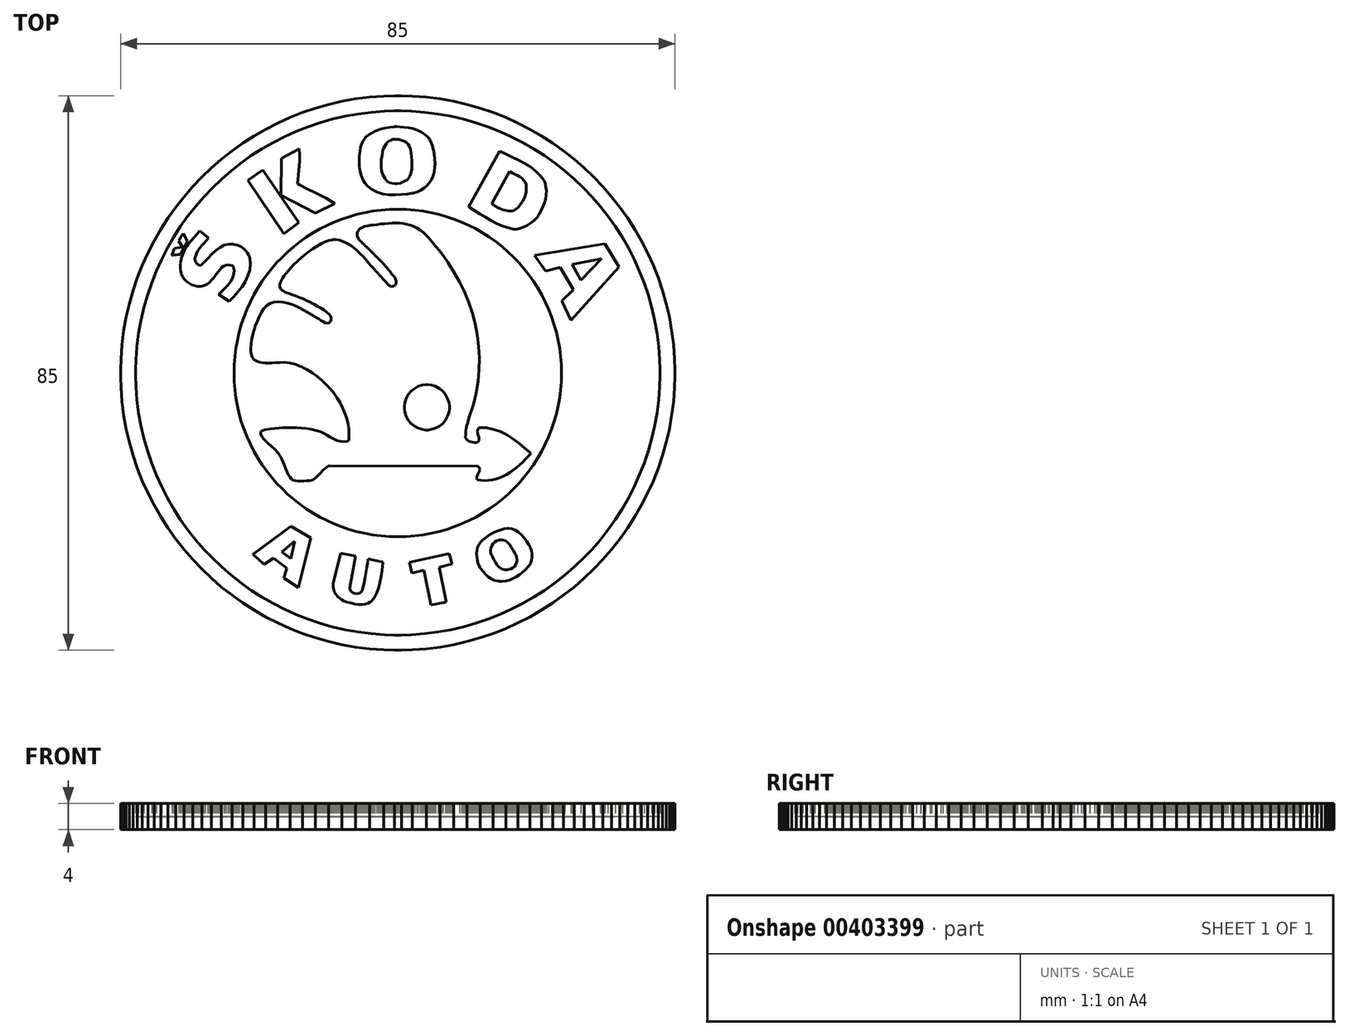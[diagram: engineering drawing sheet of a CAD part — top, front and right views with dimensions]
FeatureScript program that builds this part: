
annotation { "Feature Type Name" : "Feature", "Feature Type Description" : "" }
export const myFeature = defineFeature(function(context is Context, id is Id, definition is map)
    precondition{}
    {
        {
            var Q0;
            Q0=qCreatedBy(makeId("Top.planeOp"),FACE);
            var sketch = newSketch(context, id + "F0", { "sketchPlane" : qUnion([Q0])});
            skLineSegment(sketch, "E0", {"start": v(0.02, -42.5) * mm, "end": v(0.57, -42.5) * mm});
            skLineSegment(sketch, "E1", {"start": v(0.57, -42.5) * mm, "end": v(2.2, -42.44) * mm});
            skLineSegment(sketch, "E2", {"start": v(2.2, -42.44) * mm, "end": v(4.36, -42.28) * mm});
            skLineSegment(sketch, "E3", {"start": v(4.36, -42.28) * mm, "end": v(6.49, -42) * mm});
            skLineSegment(sketch, "E4", {"start": v(6.49, -42) * mm, "end": v(8.58, -41.63) * mm});
            skLineSegment(sketch, "E5", {"start": v(8.58, -41.63) * mm, "end": v(10.64, -41.16) * mm});
            skLineSegment(sketch, "E6", {"start": v(10.64, -41.16) * mm, "end": v(12.65, -40.59) * mm});
            skLineSegment(sketch, "E7", {"start": v(12.65, -40.59) * mm, "end": v(14.63, -39.92) * mm});
            skLineSegment(sketch, "E8", {"start": v(14.63, -39.92) * mm, "end": v(16.55, -39.16) * mm});
            skLineSegment(sketch, "E9", {"start": v(16.55, -39.16) * mm, "end": v(18.44, -38.3) * mm});
            skLineSegment(sketch, "E10", {"start": v(18.44, -38.3) * mm, "end": v(20.27, -37.37) * mm});
            skLineSegment(sketch, "E11", {"start": v(20.27, -37.37) * mm, "end": v(22.05, -36.35) * mm});
            skLineSegment(sketch, "E12", {"start": v(22.05, -36.35) * mm, "end": v(23.77, -35.24) * mm});
            skLineSegment(sketch, "E13", {"start": v(23.77, -35.24) * mm, "end": v(25.44, -34.06) * mm});
            skLineSegment(sketch, "E14", {"start": v(25.44, -34.06) * mm, "end": v(27.04, -32.8) * mm});
            skLineSegment(sketch, "E15", {"start": v(27.04, -32.8) * mm, "end": v(28.58, -31.46) * mm});
            skLineSegment(sketch, "E16", {"start": v(28.58, -31.46) * mm, "end": v(30.06, -30.06) * mm});
            skLineSegment(sketch, "E17", {"start": v(30.06, -30.06) * mm, "end": v(31.46, -28.58) * mm});
            skLineSegment(sketch, "E18", {"start": v(31.46, -28.58) * mm, "end": v(32.8, -27.04) * mm});
            skLineSegment(sketch, "E19", {"start": v(32.8, -27.04) * mm, "end": v(34.06, -25.44) * mm});
            skLineSegment(sketch, "E20", {"start": v(34.06, -25.44) * mm, "end": v(35.24, -23.77) * mm});
            skLineSegment(sketch, "E21", {"start": v(35.24, -23.77) * mm, "end": v(36.35, -22.05) * mm});
            skLineSegment(sketch, "E22", {"start": v(36.35, -22.05) * mm, "end": v(37.37, -20.27) * mm});
            skLineSegment(sketch, "E23", {"start": v(37.37, -20.27) * mm, "end": v(38.3, -18.44) * mm});
            skLineSegment(sketch, "E24", {"start": v(38.3, -18.44) * mm, "end": v(39.16, -16.55) * mm});
            skLineSegment(sketch, "E25", {"start": v(39.16, -16.55) * mm, "end": v(39.92, -14.63) * mm});
            skLineSegment(sketch, "E26", {"start": v(39.92, -14.63) * mm, "end": v(40.59, -12.65) * mm});
            skLineSegment(sketch, "E27", {"start": v(40.59, -12.65) * mm, "end": v(41.16, -10.64) * mm});
            skLineSegment(sketch, "E28", {"start": v(41.16, -10.64) * mm, "end": v(41.63, -8.58) * mm});
            skLineSegment(sketch, "E29", {"start": v(41.63, -8.58) * mm, "end": v(42, -6.49) * mm});
            skLineSegment(sketch, "E30", {"start": v(42, -6.49) * mm, "end": v(42.28, -4.36) * mm});
            skLineSegment(sketch, "E31", {"start": v(42.28, -4.36) * mm, "end": v(42.44, -2.2) * mm});
            skLineSegment(sketch, "E32", {"start": v(42.44, -2.2) * mm, "end": v(42.5, -0.57) * mm});
            skLineSegment(sketch, "E33", {"start": v(42.5, -0.57) * mm, "end": v(42.5, -0.02) * mm});
            skLineSegment(sketch, "E34", {"start": v(42.5, -0.02) * mm, "end": v(42.5, 0.53) * mm});
            skLineSegment(sketch, "E35", {"start": v(42.5, 0.53) * mm, "end": v(42.44, 2.17) * mm});
            skLineSegment(sketch, "E36", {"start": v(42.44, 2.17) * mm, "end": v(42.28, 4.33) * mm});
            skLineSegment(sketch, "E37", {"start": v(42.28, 4.33) * mm, "end": v(42, 6.45) * mm});
            skLineSegment(sketch, "E38", {"start": v(42, 6.45) * mm, "end": v(41.63, 8.55) * mm});
            skLineSegment(sketch, "E39", {"start": v(41.63, 8.55) * mm, "end": v(41.16, 10.6) * mm});
            skLineSegment(sketch, "E40", {"start": v(41.16, 10.6) * mm, "end": v(40.59, 12.62) * mm});
            skLineSegment(sketch, "E41", {"start": v(40.59, 12.62) * mm, "end": v(39.92, 14.6) * mm});
            skLineSegment(sketch, "E42", {"start": v(39.92, 14.6) * mm, "end": v(39.16, 16.52) * mm});
            skLineSegment(sketch, "E43", {"start": v(39.16, 16.52) * mm, "end": v(38.3, 18.4) * mm});
            skLineSegment(sketch, "E44", {"start": v(38.3, 18.4) * mm, "end": v(37.37, 20.24) * mm});
            skLineSegment(sketch, "E45", {"start": v(37.37, 20.24) * mm, "end": v(36.35, 22.02) * mm});
            skLineSegment(sketch, "E46", {"start": v(36.35, 22.02) * mm, "end": v(35.24, 23.75) * mm});
            skLineSegment(sketch, "E47", {"start": v(35.24, 23.75) * mm, "end": v(34.06, 25.41) * mm});
            skLineSegment(sketch, "E48", {"start": v(34.06, 25.41) * mm, "end": v(32.8, 27.02) * mm});
            skLineSegment(sketch, "E49", {"start": v(32.8, 27.02) * mm, "end": v(31.46, 28.56) * mm});
            skLineSegment(sketch, "E50", {"start": v(31.46, 28.56) * mm, "end": v(30.06, 30.04) * mm});
            skLineSegment(sketch, "E51", {"start": v(30.06, 30.04) * mm, "end": v(28.58, 31.45) * mm});
            skLineSegment(sketch, "E52", {"start": v(28.58, 31.45) * mm, "end": v(27.04, 32.78) * mm});
            skLineSegment(sketch, "E53", {"start": v(27.04, 32.78) * mm, "end": v(25.44, 34.05) * mm});
            skLineSegment(sketch, "E54", {"start": v(25.44, 34.05) * mm, "end": v(23.77, 35.23) * mm});
            skLineSegment(sketch, "E55", {"start": v(23.77, 35.23) * mm, "end": v(22.05, 36.34) * mm});
            skLineSegment(sketch, "E56", {"start": v(22.05, 36.34) * mm, "end": v(20.27, 37.36) * mm});
            skLineSegment(sketch, "E57", {"start": v(20.27, 37.36) * mm, "end": v(18.44, 38.3) * mm});
            skLineSegment(sketch, "E58", {"start": v(18.44, 38.3) * mm, "end": v(16.55, 39.15) * mm});
            skLineSegment(sketch, "E59", {"start": v(16.55, 39.15) * mm, "end": v(14.63, 39.92) * mm});
            skLineSegment(sketch, "E60", {"start": v(14.63, 39.92) * mm, "end": v(12.65, 40.58) * mm});
            skLineSegment(sketch, "E61", {"start": v(12.65, 40.58) * mm, "end": v(10.64, 41.16) * mm});
            skLineSegment(sketch, "E62", {"start": v(10.64, 41.16) * mm, "end": v(8.58, 41.63) * mm});
            skLineSegment(sketch, "E63", {"start": v(8.58, 41.63) * mm, "end": v(6.49, 42) * mm});
            skLineSegment(sketch, "E64", {"start": v(6.49, 42) * mm, "end": v(4.36, 42.28) * mm});
            skLineSegment(sketch, "E65", {"start": v(4.36, 42.28) * mm, "end": v(2.2, 42.44) * mm});
            skLineSegment(sketch, "E66", {"start": v(2.2, 42.44) * mm, "end": v(0.57, 42.5) * mm});
            skLineSegment(sketch, "E67", {"start": v(0.57, 42.5) * mm, "end": v(0.02, 42.5) * mm});
            skLineSegment(sketch, "E68", {"start": v(0.02, 42.5) * mm, "end": v(-0.53, 42.5) * mm});
            skLineSegment(sketch, "E69", {"start": v(-0.53, 42.5) * mm, "end": v(-2.17, 42.44) * mm});
            skLineSegment(sketch, "E70", {"start": v(-2.17, 42.44) * mm, "end": v(-4.33, 42.28) * mm});
            skLineSegment(sketch, "E71", {"start": v(-4.33, 42.28) * mm, "end": v(-6.45, 42) * mm});
            skLineSegment(sketch, "E72", {"start": v(-6.45, 42) * mm, "end": v(-8.55, 41.63) * mm});
            skLineSegment(sketch, "E73", {"start": v(-8.55, 41.63) * mm, "end": v(-10.6, 41.16) * mm});
            skLineSegment(sketch, "E74", {"start": v(-10.6, 41.16) * mm, "end": v(-12.62, 40.58) * mm});
            skLineSegment(sketch, "E75", {"start": v(-12.62, 40.58) * mm, "end": v(-14.6, 39.92) * mm});
            skLineSegment(sketch, "E76", {"start": v(-14.6, 39.92) * mm, "end": v(-16.52, 39.15) * mm});
            skLineSegment(sketch, "E77", {"start": v(-16.52, 39.15) * mm, "end": v(-18.4, 38.3) * mm});
            skLineSegment(sketch, "E78", {"start": v(-18.4, 38.3) * mm, "end": v(-20.24, 37.36) * mm});
            skLineSegment(sketch, "E79", {"start": v(-20.24, 37.36) * mm, "end": v(-22.02, 36.34) * mm});
            skLineSegment(sketch, "E80", {"start": v(-22.02, 36.34) * mm, "end": v(-23.74, 35.23) * mm});
            skLineSegment(sketch, "E81", {"start": v(-23.74, 35.23) * mm, "end": v(-25.41, 34.05) * mm});
            skLineSegment(sketch, "E82", {"start": v(-25.41, 34.05) * mm, "end": v(-27.02, 32.78) * mm});
            skLineSegment(sketch, "E83", {"start": v(-27.02, 32.78) * mm, "end": v(-28.56, 31.45) * mm});
            skLineSegment(sketch, "E84", {"start": v(-28.56, 31.45) * mm, "end": v(-30.04, 30.04) * mm});
            skLineSegment(sketch, "E85", {"start": v(-30.04, 30.04) * mm, "end": v(-31.45, 28.56) * mm});
            skLineSegment(sketch, "E86", {"start": v(-31.45, 28.56) * mm, "end": v(-32.78, 27.02) * mm});
            skLineSegment(sketch, "E87", {"start": v(-32.78, 27.02) * mm, "end": v(-34.05, 25.41) * mm});
            skLineSegment(sketch, "E88", {"start": v(-34.05, 25.41) * mm, "end": v(-35.23, 23.75) * mm});
            skLineSegment(sketch, "E89", {"start": v(-35.23, 23.75) * mm, "end": v(-36.34, 22.02) * mm});
            skLineSegment(sketch, "E90", {"start": v(-36.34, 22.02) * mm, "end": v(-37.36, 20.24) * mm});
            skLineSegment(sketch, "E91", {"start": v(-37.36, 20.24) * mm, "end": v(-38.3, 18.4) * mm});
            skLineSegment(sketch, "E92", {"start": v(-38.3, 18.4) * mm, "end": v(-39.15, 16.52) * mm});
            skLineSegment(sketch, "E93", {"start": v(-39.15, 16.52) * mm, "end": v(-39.91, 14.6) * mm});
            skLineSegment(sketch, "E94", {"start": v(-39.91, 14.6) * mm, "end": v(-40.58, 12.62) * mm});
            skLineSegment(sketch, "E95", {"start": v(-40.58, 12.62) * mm, "end": v(-41.16, 10.6) * mm});
            skLineSegment(sketch, "E96", {"start": v(-41.16, 10.6) * mm, "end": v(-41.63, 8.55) * mm});
            skLineSegment(sketch, "E97", {"start": v(-41.63, 8.55) * mm, "end": v(-42, 6.45) * mm});
            skLineSegment(sketch, "E98", {"start": v(-42, 6.45) * mm, "end": v(-42.28, 4.33) * mm});
            skLineSegment(sketch, "E99", {"start": v(-42.28, 4.33) * mm, "end": v(-42.44, 2.17) * mm});
            skLineSegment(sketch, "E100", {"start": v(-42.44, 2.17) * mm, "end": v(-42.5, 0.53) * mm});
            skLineSegment(sketch, "E101", {"start": v(-42.5, 0.53) * mm, "end": v(-42.5, -0.02) * mm});
            skLineSegment(sketch, "E102", {"start": v(-42.5, -0.02) * mm, "end": v(-42.5, -0.56) * mm});
            skLineSegment(sketch, "E103", {"start": v(-42.5, -0.56) * mm, "end": v(-42.44, -2.2) * mm});
            skLineSegment(sketch, "E104", {"start": v(-42.44, -2.2) * mm, "end": v(-42.28, -4.36) * mm});
            skLineSegment(sketch, "E105", {"start": v(-42.28, -4.36) * mm, "end": v(-42, -6.49) * mm});
            skLineSegment(sketch, "E106", {"start": v(-42, -6.49) * mm, "end": v(-41.63, -8.58) * mm});
            skLineSegment(sketch, "E107", {"start": v(-41.63, -8.58) * mm, "end": v(-41.16, -10.64) * mm});
            skLineSegment(sketch, "E108", {"start": v(-41.16, -10.64) * mm, "end": v(-40.58, -12.65) * mm});
            skLineSegment(sketch, "E109", {"start": v(-40.58, -12.65) * mm, "end": v(-39.91, -14.63) * mm});
            skLineSegment(sketch, "E110", {"start": v(-39.91, -14.63) * mm, "end": v(-39.15, -16.55) * mm});
            skLineSegment(sketch, "E111", {"start": v(-39.15, -16.55) * mm, "end": v(-38.3, -18.44) * mm});
            skLineSegment(sketch, "E112", {"start": v(-38.3, -18.44) * mm, "end": v(-37.36, -20.27) * mm});
            skLineSegment(sketch, "E113", {"start": v(-37.36, -20.27) * mm, "end": v(-36.34, -22.05) * mm});
            skLineSegment(sketch, "E114", {"start": v(-36.34, -22.05) * mm, "end": v(-35.23, -23.77) * mm});
            skLineSegment(sketch, "E115", {"start": v(-35.23, -23.77) * mm, "end": v(-34.05, -25.44) * mm});
            skLineSegment(sketch, "E116", {"start": v(-34.05, -25.44) * mm, "end": v(-32.78, -27.04) * mm});
            skLineSegment(sketch, "E117", {"start": v(-32.78, -27.04) * mm, "end": v(-31.45, -28.58) * mm});
            skLineSegment(sketch, "E118", {"start": v(-31.45, -28.58) * mm, "end": v(-30.04, -30.06) * mm});
            skLineSegment(sketch, "E119", {"start": v(-30.04, -30.06) * mm, "end": v(-28.56, -31.46) * mm});
            skLineSegment(sketch, "E120", {"start": v(-28.56, -31.46) * mm, "end": v(-27.02, -32.8) * mm});
            skLineSegment(sketch, "E121", {"start": v(-27.02, -32.8) * mm, "end": v(-25.41, -34.06) * mm});
            skLineSegment(sketch, "E122", {"start": v(-25.41, -34.06) * mm, "end": v(-23.74, -35.24) * mm});
            skLineSegment(sketch, "E123", {"start": v(-23.74, -35.24) * mm, "end": v(-22.02, -36.35) * mm});
            skLineSegment(sketch, "E124", {"start": v(-22.02, -36.35) * mm, "end": v(-20.24, -37.37) * mm});
            skLineSegment(sketch, "E125", {"start": v(-20.24, -37.37) * mm, "end": v(-18.4, -38.3) * mm});
            skLineSegment(sketch, "E126", {"start": v(-18.4, -38.3) * mm, "end": v(-16.52, -39.16) * mm});
            skLineSegment(sketch, "E127", {"start": v(-16.52, -39.16) * mm, "end": v(-14.6, -39.92) * mm});
            skLineSegment(sketch, "E128", {"start": v(-14.6, -39.92) * mm, "end": v(-12.62, -40.59) * mm});
            skLineSegment(sketch, "E129", {"start": v(-12.62, -40.59) * mm, "end": v(-10.6, -41.16) * mm});
            skLineSegment(sketch, "E130", {"start": v(-10.6, -41.16) * mm, "end": v(-8.55, -41.63) * mm});
            skLineSegment(sketch, "E131", {"start": v(-8.55, -41.63) * mm, "end": v(-6.45, -42) * mm});
            skLineSegment(sketch, "E132", {"start": v(-6.45, -42) * mm, "end": v(-4.33, -42.28) * mm});
            skLineSegment(sketch, "E133", {"start": v(-4.33, -42.28) * mm, "end": v(-2.17, -42.44) * mm});
            skLineSegment(sketch, "E134", {"start": v(-2.17, -42.44) * mm, "end": v(-0.53, -42.5) * mm});
            skLineSegment(sketch, "E135", {"start": v(-0.53, -42.5) * mm, "end": v(0.02, -42.5) * mm});
            skLineSegment(sketch, "E136", {"start": v(0.02, -41.43) * mm, "end": v(0.55, -41.43) * mm});
            skLineSegment(sketch, "E137", {"start": v(0.55, -41.43) * mm, "end": v(2.15, -41.38) * mm});
            skLineSegment(sketch, "E138", {"start": v(2.15, -41.38) * mm, "end": v(4.25, -41.22) * mm});
            skLineSegment(sketch, "E139", {"start": v(4.25, -41.22) * mm, "end": v(6.33, -40.95) * mm});
            skLineSegment(sketch, "E140", {"start": v(6.33, -40.95) * mm, "end": v(8.37, -40.59) * mm});
            skLineSegment(sketch, "E141", {"start": v(8.37, -40.59) * mm, "end": v(10.37, -40.13) * mm});
            skLineSegment(sketch, "E142", {"start": v(10.37, -40.13) * mm, "end": v(12.33, -39.57) * mm});
            skLineSegment(sketch, "E143", {"start": v(12.33, -39.57) * mm, "end": v(14.26, -38.92) * mm});
            skLineSegment(sketch, "E144", {"start": v(14.26, -38.92) * mm, "end": v(16.14, -38.18) * mm});
            skLineSegment(sketch, "E145", {"start": v(16.14, -38.18) * mm, "end": v(17.97, -37.35) * mm});
            skLineSegment(sketch, "E146", {"start": v(17.97, -37.35) * mm, "end": v(19.76, -36.43) * mm});
            skLineSegment(sketch, "E147", {"start": v(19.76, -36.43) * mm, "end": v(21.5, -35.44) * mm});
            skLineSegment(sketch, "E148", {"start": v(21.5, -35.44) * mm, "end": v(23.17, -34.36) * mm});
            skLineSegment(sketch, "E149", {"start": v(23.17, -34.36) * mm, "end": v(24.8, -33.2) * mm});
            skLineSegment(sketch, "E150", {"start": v(24.8, -33.2) * mm, "end": v(26.36, -31.98) * mm});
            skLineSegment(sketch, "E151", {"start": v(26.36, -31.98) * mm, "end": v(27.86, -30.67) * mm});
            skLineSegment(sketch, "E152", {"start": v(27.86, -30.67) * mm, "end": v(29.3, -29.3) * mm});
            skLineSegment(sketch, "E153", {"start": v(29.3, -29.3) * mm, "end": v(30.67, -27.86) * mm});
            skLineSegment(sketch, "E154", {"start": v(30.67, -27.86) * mm, "end": v(31.98, -26.36) * mm});
            skLineSegment(sketch, "E155", {"start": v(31.98, -26.36) * mm, "end": v(33.2, -24.8) * mm});
            skLineSegment(sketch, "E156", {"start": v(33.2, -24.8) * mm, "end": v(34.36, -23.17) * mm});
            skLineSegment(sketch, "E157", {"start": v(34.36, -23.17) * mm, "end": v(35.44, -21.5) * mm});
            skLineSegment(sketch, "E158", {"start": v(35.44, -21.5) * mm, "end": v(36.43, -19.76) * mm});
            skLineSegment(sketch, "E159", {"start": v(36.43, -19.76) * mm, "end": v(37.35, -17.97) * mm});
            skLineSegment(sketch, "E160", {"start": v(37.35, -17.97) * mm, "end": v(38.18, -16.14) * mm});
            skLineSegment(sketch, "E161", {"start": v(38.18, -16.14) * mm, "end": v(38.92, -14.26) * mm});
            skLineSegment(sketch, "E162", {"start": v(38.92, -14.26) * mm, "end": v(39.57, -12.33) * mm});
            skLineSegment(sketch, "E163", {"start": v(39.57, -12.33) * mm, "end": v(40.13, -10.37) * mm});
            skLineSegment(sketch, "E164", {"start": v(40.13, -10.37) * mm, "end": v(40.59, -8.37) * mm});
            skLineSegment(sketch, "E165", {"start": v(40.59, -8.37) * mm, "end": v(40.95, -6.33) * mm});
            skLineSegment(sketch, "E166", {"start": v(40.95, -6.33) * mm, "end": v(41.22, -4.25) * mm});
            skLineSegment(sketch, "E167", {"start": v(41.22, -4.25) * mm, "end": v(41.38, -2.15) * mm});
            skLineSegment(sketch, "E168", {"start": v(41.38, -2.15) * mm, "end": v(41.43, -0.55) * mm});
            skLineSegment(sketch, "E169", {"start": v(41.43, -0.55) * mm, "end": v(41.43, -0.02) * mm});
            skLineSegment(sketch, "E170", {"start": v(41.43, -0.02) * mm, "end": v(41.43, 0.51) * mm});
            skLineSegment(sketch, "E171", {"start": v(41.43, 0.51) * mm, "end": v(41.38, 2.11) * mm});
            skLineSegment(sketch, "E172", {"start": v(41.38, 2.11) * mm, "end": v(41.22, 4.22) * mm});
            skLineSegment(sketch, "E173", {"start": v(41.22, 4.22) * mm, "end": v(40.95, 6.3) * mm});
            skLineSegment(sketch, "E174", {"start": v(40.95, 6.3) * mm, "end": v(40.59, 8.33) * mm});
            skLineSegment(sketch, "E175", {"start": v(40.59, 8.33) * mm, "end": v(40.13, 10.34) * mm});
            skLineSegment(sketch, "E176", {"start": v(40.13, 10.34) * mm, "end": v(39.57, 12.3) * mm});
            skLineSegment(sketch, "E177", {"start": v(39.57, 12.3) * mm, "end": v(38.92, 14.23) * mm});
            skLineSegment(sketch, "E178", {"start": v(38.92, 14.23) * mm, "end": v(38.18, 16.1) * mm});
            skLineSegment(sketch, "E179", {"start": v(38.18, 16.1) * mm, "end": v(37.35, 17.94) * mm});
            skLineSegment(sketch, "E180", {"start": v(37.35, 17.94) * mm, "end": v(36.43, 19.73) * mm});
            skLineSegment(sketch, "E181", {"start": v(36.43, 19.73) * mm, "end": v(35.44, 21.47) * mm});
            skLineSegment(sketch, "E182", {"start": v(35.44, 21.47) * mm, "end": v(34.36, 23.15) * mm});
            skLineSegment(sketch, "E183", {"start": v(34.36, 23.15) * mm, "end": v(33.2, 24.77) * mm});
            skLineSegment(sketch, "E184", {"start": v(33.2, 24.77) * mm, "end": v(31.98, 26.34) * mm});
            skLineSegment(sketch, "E185", {"start": v(31.98, 26.34) * mm, "end": v(30.67, 27.84) * mm});
            skLineSegment(sketch, "E186", {"start": v(30.67, 27.84) * mm, "end": v(29.3, 29.28) * mm});
            skLineSegment(sketch, "E187", {"start": v(29.3, 29.28) * mm, "end": v(27.86, 30.66) * mm});
            skLineSegment(sketch, "E188", {"start": v(27.86, 30.66) * mm, "end": v(26.36, 31.96) * mm});
            skLineSegment(sketch, "E189", {"start": v(26.36, 31.96) * mm, "end": v(24.8, 33.2) * mm});
            skLineSegment(sketch, "E190", {"start": v(24.8, 33.2) * mm, "end": v(23.17, 34.35) * mm});
            skLineSegment(sketch, "E191", {"start": v(23.17, 34.35) * mm, "end": v(21.5, 35.43) * mm});
            skLineSegment(sketch, "E192", {"start": v(21.5, 35.43) * mm, "end": v(19.76, 36.42) * mm});
            skLineSegment(sketch, "E193", {"start": v(19.76, 36.42) * mm, "end": v(17.97, 37.34) * mm});
            skLineSegment(sketch, "E194", {"start": v(17.97, 37.34) * mm, "end": v(16.14, 38.17) * mm});
            skLineSegment(sketch, "E195", {"start": v(16.14, 38.17) * mm, "end": v(14.26, 38.91) * mm});
            skLineSegment(sketch, "E196", {"start": v(14.26, 38.91) * mm, "end": v(12.34, 39.57) * mm});
            skLineSegment(sketch, "E197", {"start": v(12.34, 39.57) * mm, "end": v(10.37, 40.12) * mm});
            skLineSegment(sketch, "E198", {"start": v(10.37, 40.12) * mm, "end": v(8.37, 40.59) * mm});
            skLineSegment(sketch, "E199", {"start": v(8.37, 40.59) * mm, "end": v(6.33, 40.95) * mm});
            skLineSegment(sketch, "E200", {"start": v(6.33, 40.95) * mm, "end": v(4.25, 41.22) * mm});
            skLineSegment(sketch, "E201", {"start": v(4.25, 41.22) * mm, "end": v(2.15, 41.38) * mm});
            skLineSegment(sketch, "E202", {"start": v(2.15, 41.38) * mm, "end": v(0.55, 41.43) * mm});
            skLineSegment(sketch, "E203", {"start": v(0.55, 41.43) * mm, "end": v(0.02, 41.43) * mm});
            skLineSegment(sketch, "E204", {"start": v(0.02, 41.43) * mm, "end": v(-0.51, 41.43) * mm});
            skLineSegment(sketch, "E205", {"start": v(-0.51, 41.43) * mm, "end": v(-2.11, 41.38) * mm});
            skLineSegment(sketch, "E206", {"start": v(-2.11, 41.38) * mm, "end": v(-4.22, 41.22) * mm});
            skLineSegment(sketch, "E207", {"start": v(-4.22, 41.22) * mm, "end": v(-6.29, 40.95) * mm});
            skLineSegment(sketch, "E208", {"start": v(-6.29, 40.95) * mm, "end": v(-8.33, 40.59) * mm});
            skLineSegment(sketch, "E209", {"start": v(-8.33, 40.59) * mm, "end": v(-10.33, 40.12) * mm});
            skLineSegment(sketch, "E210", {"start": v(-10.33, 40.12) * mm, "end": v(-12.3, 39.57) * mm});
            skLineSegment(sketch, "E211", {"start": v(-12.3, 39.57) * mm, "end": v(-14.22, 38.91) * mm});
            skLineSegment(sketch, "E212", {"start": v(-14.22, 38.91) * mm, "end": v(-16.1, 38.17) * mm});
            skLineSegment(sketch, "E213", {"start": v(-16.1, 38.17) * mm, "end": v(-17.94, 37.34) * mm});
            skLineSegment(sketch, "E214", {"start": v(-17.94, 37.34) * mm, "end": v(-19.72, 36.42) * mm});
            skLineSegment(sketch, "E215", {"start": v(-19.72, 36.42) * mm, "end": v(-21.46, 35.43) * mm});
            skLineSegment(sketch, "E216", {"start": v(-21.46, 35.43) * mm, "end": v(-23.14, 34.35) * mm});
            skLineSegment(sketch, "E217", {"start": v(-23.14, 34.35) * mm, "end": v(-24.76, 33.2) * mm});
            skLineSegment(sketch, "E218", {"start": v(-24.76, 33.2) * mm, "end": v(-26.33, 31.96) * mm});
            skLineSegment(sketch, "E219", {"start": v(-26.33, 31.96) * mm, "end": v(-27.83, 30.66) * mm});
            skLineSegment(sketch, "E220", {"start": v(-27.83, 30.66) * mm, "end": v(-29.27, 29.28) * mm});
            skLineSegment(sketch, "E221", {"start": v(-29.27, 29.28) * mm, "end": v(-30.64, 27.84) * mm});
            skLineSegment(sketch, "E222", {"start": v(-30.64, 27.84) * mm, "end": v(-31.94, 26.34) * mm});
            skLineSegment(sketch, "E223", {"start": v(-31.94, 26.34) * mm, "end": v(-33.17, 24.77) * mm});
            skLineSegment(sketch, "E224", {"start": v(-33.17, 24.77) * mm, "end": v(-34.32, 23.15) * mm});
            skLineSegment(sketch, "E225", {"start": v(-34.32, 23.15) * mm, "end": v(-35.4, 21.47) * mm});
            skLineSegment(sketch, "E226", {"start": v(-35.4, 21.47) * mm, "end": v(-36.4, 19.73) * mm});
            skLineSegment(sketch, "E227", {"start": v(-36.4, 19.73) * mm, "end": v(-37.31, 17.94) * mm});
            skLineSegment(sketch, "E228", {"start": v(-37.31, 17.94) * mm, "end": v(-38.14, 16.1) * mm});
            skLineSegment(sketch, "E229", {"start": v(-38.14, 16.1) * mm, "end": v(-38.88, 14.23) * mm});
            skLineSegment(sketch, "E230", {"start": v(-38.88, 14.23) * mm, "end": v(-39.53, 12.3) * mm});
            skLineSegment(sketch, "E231", {"start": v(-39.53, 12.3) * mm, "end": v(-40.09, 10.34) * mm});
            skLineSegment(sketch, "E232", {"start": v(-40.09, 10.34) * mm, "end": v(-40.55, 8.33) * mm});
            skLineSegment(sketch, "E233", {"start": v(-40.55, 8.33) * mm, "end": v(-40.92, 6.3) * mm});
            skLineSegment(sketch, "E234", {"start": v(-40.92, 6.3) * mm, "end": v(-41.18, 4.22) * mm});
            skLineSegment(sketch, "E235", {"start": v(-41.18, 4.22) * mm, "end": v(-41.34, 2.11) * mm});
            skLineSegment(sketch, "E236", {"start": v(-41.34, 2.11) * mm, "end": v(-41.4, 0.51) * mm});
            skLineSegment(sketch, "E237", {"start": v(-41.4, 0.51) * mm, "end": v(-41.4, -0.02) * mm});
            skLineSegment(sketch, "E238", {"start": v(-41.4, -0.02) * mm, "end": v(-41.4, -0.55) * mm});
            skLineSegment(sketch, "E239", {"start": v(-41.4, -0.55) * mm, "end": v(-41.34, -2.15) * mm});
            skLineSegment(sketch, "E240", {"start": v(-41.34, -2.15) * mm, "end": v(-41.18, -4.25) * mm});
            skLineSegment(sketch, "E241", {"start": v(-41.18, -4.25) * mm, "end": v(-40.92, -6.33) * mm});
            skLineSegment(sketch, "E242", {"start": v(-40.92, -6.33) * mm, "end": v(-40.55, -8.37) * mm});
            skLineSegment(sketch, "E243", {"start": v(-40.55, -8.37) * mm, "end": v(-40.09, -10.37) * mm});
            skLineSegment(sketch, "E244", {"start": v(-40.09, -10.37) * mm, "end": v(-39.53, -12.33) * mm});
            skLineSegment(sketch, "E245", {"start": v(-39.53, -12.33) * mm, "end": v(-38.88, -14.26) * mm});
            skLineSegment(sketch, "E246", {"start": v(-38.88, -14.26) * mm, "end": v(-38.14, -16.14) * mm});
            skLineSegment(sketch, "E247", {"start": v(-38.14, -16.14) * mm, "end": v(-37.31, -17.97) * mm});
            skLineSegment(sketch, "E248", {"start": v(-37.31, -17.97) * mm, "end": v(-36.4, -19.76) * mm});
            skLineSegment(sketch, "E249", {"start": v(-36.4, -19.76) * mm, "end": v(-35.4, -21.5) * mm});
            skLineSegment(sketch, "E250", {"start": v(-35.4, -21.5) * mm, "end": v(-34.32, -23.17) * mm});
            skLineSegment(sketch, "E251", {"start": v(-34.32, -23.17) * mm, "end": v(-33.17, -24.8) * mm});
            skLineSegment(sketch, "E252", {"start": v(-33.17, -24.8) * mm, "end": v(-31.94, -26.36) * mm});
            skLineSegment(sketch, "E253", {"start": v(-31.94, -26.36) * mm, "end": v(-30.64, -27.86) * mm});
            skLineSegment(sketch, "E254", {"start": v(-30.64, -27.86) * mm, "end": v(-29.27, -29.3) * mm});
            skLineSegment(sketch, "E255", {"start": v(-29.27, -29.3) * mm, "end": v(-27.83, -30.67) * mm});
            skLineSegment(sketch, "E256", {"start": v(-27.83, -30.67) * mm, "end": v(-26.33, -31.98) * mm});
            skLineSegment(sketch, "E257", {"start": v(-26.33, -31.98) * mm, "end": v(-24.76, -33.2) * mm});
            skLineSegment(sketch, "E258", {"start": v(-24.76, -33.2) * mm, "end": v(-23.14, -34.36) * mm});
            skLineSegment(sketch, "E259", {"start": v(-23.14, -34.36) * mm, "end": v(-21.46, -35.44) * mm});
            skLineSegment(sketch, "E260", {"start": v(-21.46, -35.44) * mm, "end": v(-19.72, -36.43) * mm});
            skLineSegment(sketch, "E261", {"start": v(-19.72, -36.43) * mm, "end": v(-17.94, -37.35) * mm});
            skLineSegment(sketch, "E262", {"start": v(-17.94, -37.35) * mm, "end": v(-16.1, -38.18) * mm});
            skLineSegment(sketch, "E263", {"start": v(-16.1, -38.18) * mm, "end": v(-14.22, -38.92) * mm});
            skLineSegment(sketch, "E264", {"start": v(-14.22, -38.92) * mm, "end": v(-12.3, -39.57) * mm});
            skLineSegment(sketch, "E265", {"start": v(-12.3, -39.57) * mm, "end": v(-10.33, -40.13) * mm});
            skLineSegment(sketch, "E266", {"start": v(-10.33, -40.13) * mm, "end": v(-8.33, -40.59) * mm});
            skLineSegment(sketch, "E267", {"start": v(-8.33, -40.59) * mm, "end": v(-6.29, -40.95) * mm});
            skLineSegment(sketch, "E268", {"start": v(-6.29, -40.95) * mm, "end": v(-4.22, -41.22) * mm});
            skLineSegment(sketch, "E269", {"start": v(-4.22, -41.22) * mm, "end": v(-2.11, -41.38) * mm});
            skLineSegment(sketch, "E270", {"start": v(-2.11, -41.38) * mm, "end": v(-0.51, -41.43) * mm});
            skLineSegment(sketch, "E271", {"start": v(-0.51, -41.43) * mm, "end": v(0.02, -41.43) * mm});
            skLineSegment(sketch, "E272", {"start": v(0.02, -40.18) * mm, "end": v(0.54, -40.18) * mm});
            skLineSegment(sketch, "E273", {"start": v(0.54, -40.18) * mm, "end": v(2.09, -40.13) * mm});
            skLineSegment(sketch, "E274", {"start": v(2.09, -40.13) * mm, "end": v(4.12, -39.97) * mm});
            skLineSegment(sketch, "E275", {"start": v(4.12, -39.97) * mm, "end": v(6.13, -39.72) * mm});
            skLineSegment(sketch, "E276", {"start": v(6.13, -39.72) * mm, "end": v(8.11, -39.36) * mm});
            skLineSegment(sketch, "E277", {"start": v(8.11, -39.36) * mm, "end": v(10.06, -38.91) * mm});
            skLineSegment(sketch, "E278", {"start": v(10.06, -38.91) * mm, "end": v(11.96, -38.37) * mm});
            skLineSegment(sketch, "E279", {"start": v(11.96, -38.37) * mm, "end": v(13.83, -37.74) * mm});
            skLineSegment(sketch, "E280", {"start": v(13.83, -37.74) * mm, "end": v(15.66, -37.02) * mm});
            skLineSegment(sketch, "E281", {"start": v(15.66, -37.02) * mm, "end": v(17.44, -36.22) * mm});
            skLineSegment(sketch, "E282", {"start": v(17.44, -36.22) * mm, "end": v(19.17, -35.33) * mm});
            skLineSegment(sketch, "E283", {"start": v(19.17, -35.33) * mm, "end": v(20.85, -34.36) * mm});
            skLineSegment(sketch, "E284", {"start": v(20.85, -34.36) * mm, "end": v(22.48, -33.32) * mm});
            skLineSegment(sketch, "E285", {"start": v(22.48, -33.32) * mm, "end": v(24.06, -32.2) * mm});
            skLineSegment(sketch, "E286", {"start": v(24.06, -32.2) * mm, "end": v(25.58, -31) * mm});
            skLineSegment(sketch, "E287", {"start": v(25.58, -31) * mm, "end": v(27.04, -29.74) * mm});
            skLineSegment(sketch, "E288", {"start": v(27.04, -29.74) * mm, "end": v(28.43, -28.42) * mm});
            skLineSegment(sketch, "E289", {"start": v(28.43, -28.42) * mm, "end": v(29.77, -27.02) * mm});
            skLineSegment(sketch, "E290", {"start": v(29.77, -27.02) * mm, "end": v(31.03, -25.56) * mm});
            skLineSegment(sketch, "E291", {"start": v(31.03, -25.56) * mm, "end": v(32.22, -24.05) * mm});
            skLineSegment(sketch, "E292", {"start": v(32.22, -24.05) * mm, "end": v(33.35, -22.47) * mm});
            skLineSegment(sketch, "E293", {"start": v(33.35, -22.47) * mm, "end": v(34.4, -20.84) * mm});
            skLineSegment(sketch, "E294", {"start": v(34.4, -20.84) * mm, "end": v(35.36, -19.16) * mm});
            skLineSegment(sketch, "E295", {"start": v(35.36, -19.16) * mm, "end": v(36.25, -17.43) * mm});
            skLineSegment(sketch, "E296", {"start": v(36.25, -17.43) * mm, "end": v(37.05, -15.65) * mm});
            skLineSegment(sketch, "E297", {"start": v(37.05, -15.65) * mm, "end": v(37.77, -13.83) * mm});
            skLineSegment(sketch, "E298", {"start": v(37.77, -13.83) * mm, "end": v(38.4, -11.96) * mm});
            skLineSegment(sketch, "E299", {"start": v(38.4, -11.96) * mm, "end": v(38.95, -10.05) * mm});
            skLineSegment(sketch, "E300", {"start": v(38.95, -10.05) * mm, "end": v(39.4, -8.11) * mm});
            skLineSegment(sketch, "E301", {"start": v(39.4, -8.11) * mm, "end": v(39.75, -6.13) * mm});
            skLineSegment(sketch, "E302", {"start": v(39.75, -6.13) * mm, "end": v(40, -4.12) * mm});
            skLineSegment(sketch, "E303", {"start": v(40, -4.12) * mm, "end": v(40.16, -2.08) * mm});
            skLineSegment(sketch, "E304", {"start": v(40.16, -2.08) * mm, "end": v(40.22, -0.54) * mm});
            skLineSegment(sketch, "E305", {"start": v(40.22, -0.54) * mm, "end": v(40.22, -0.02) * mm});
            skLineSegment(sketch, "E306", {"start": v(40.22, -0.02) * mm, "end": v(40.22, 0.5) * mm});
            skLineSegment(sketch, "E307", {"start": v(40.22, 0.5) * mm, "end": v(40.16, 2.05) * mm});
            skLineSegment(sketch, "E308", {"start": v(40.16, 2.05) * mm, "end": v(40, 4.1) * mm});
            skLineSegment(sketch, "E309", {"start": v(40, 4.1) * mm, "end": v(39.75, 6.1) * mm});
            skLineSegment(sketch, "E310", {"start": v(39.75, 6.1) * mm, "end": v(39.4, 8.09) * mm});
            skLineSegment(sketch, "E311", {"start": v(39.4, 8.09) * mm, "end": v(38.95, 10.03) * mm});
            skLineSegment(sketch, "E312", {"start": v(38.95, 10.03) * mm, "end": v(38.4, 11.94) * mm});
            skLineSegment(sketch, "E313", {"start": v(38.4, 11.94) * mm, "end": v(37.77, 13.8) * mm});
            skLineSegment(sketch, "E314", {"start": v(37.77, 13.8) * mm, "end": v(37.05, 15.63) * mm});
            skLineSegment(sketch, "E315", {"start": v(37.05, 15.63) * mm, "end": v(36.25, 17.41) * mm});
            skLineSegment(sketch, "E316", {"start": v(36.25, 17.41) * mm, "end": v(35.36, 19.15) * mm});
            skLineSegment(sketch, "E317", {"start": v(35.36, 19.15) * mm, "end": v(34.4, 20.83) * mm});
            skLineSegment(sketch, "E318", {"start": v(34.4, 20.83) * mm, "end": v(33.35, 22.46) * mm});
            skLineSegment(sketch, "E319", {"start": v(33.35, 22.46) * mm, "end": v(32.22, 24.04) * mm});
            skLineSegment(sketch, "E320", {"start": v(32.22, 24.04) * mm, "end": v(31.03, 25.56) * mm});
            skLineSegment(sketch, "E321", {"start": v(31.03, 25.56) * mm, "end": v(29.77, 27.02) * mm});
            skLineSegment(sketch, "E322", {"start": v(29.77, 27.02) * mm, "end": v(28.43, 28.41) * mm});
            skLineSegment(sketch, "E323", {"start": v(28.43, 28.41) * mm, "end": v(27.04, 29.74) * mm});
            skLineSegment(sketch, "E324", {"start": v(27.04, 29.74) * mm, "end": v(25.58, 31) * mm});
            skLineSegment(sketch, "E325", {"start": v(25.58, 31) * mm, "end": v(24.06, 32.2) * mm});
            skLineSegment(sketch, "E326", {"start": v(24.06, 32.2) * mm, "end": v(22.48, 33.32) * mm});
            skLineSegment(sketch, "E327", {"start": v(22.48, 33.32) * mm, "end": v(20.85, 34.36) * mm});
            skLineSegment(sketch, "E328", {"start": v(20.85, 34.36) * mm, "end": v(19.17, 35.33) * mm});
            skLineSegment(sketch, "E329", {"start": v(19.17, 35.33) * mm, "end": v(17.44, 36.22) * mm});
            skLineSegment(sketch, "E330", {"start": v(17.44, 36.22) * mm, "end": v(15.66, 37.02) * mm});
            skLineSegment(sketch, "E331", {"start": v(15.66, 37.02) * mm, "end": v(13.83, 37.74) * mm});
            skLineSegment(sketch, "E332", {"start": v(13.83, 37.74) * mm, "end": v(11.96, 38.37) * mm});
            skLineSegment(sketch, "E333", {"start": v(11.96, 38.37) * mm, "end": v(10.06, 38.92) * mm});
            skLineSegment(sketch, "E334", {"start": v(10.06, 38.92) * mm, "end": v(8.11, 39.36) * mm});
            skLineSegment(sketch, "E335", {"start": v(8.11, 39.36) * mm, "end": v(6.13, 39.72) * mm});
            skLineSegment(sketch, "E336", {"start": v(6.13, 39.72) * mm, "end": v(4.12, 39.97) * mm});
            skLineSegment(sketch, "E337", {"start": v(4.12, 39.97) * mm, "end": v(2.09, 40.13) * mm});
            skLineSegment(sketch, "E338", {"start": v(2.09, 40.13) * mm, "end": v(0.54, 40.18) * mm});
            skLineSegment(sketch, "E339", {"start": v(0.54, 40.18) * mm, "end": v(0.02, 40.18) * mm});
            skLineSegment(sketch, "E340", {"start": v(0.02, 40.18) * mm, "end": v(-0.5, 40.18) * mm});
            skLineSegment(sketch, "E341", {"start": v(-0.5, 40.18) * mm, "end": v(-2.05, 40.13) * mm});
            skLineSegment(sketch, "E342", {"start": v(-2.05, 40.13) * mm, "end": v(-4.09, 39.97) * mm});
            skLineSegment(sketch, "E343", {"start": v(-4.09, 39.97) * mm, "end": v(-6.1, 39.72) * mm});
            skLineSegment(sketch, "E344", {"start": v(-6.1, 39.72) * mm, "end": v(-8.08, 39.36) * mm});
            skLineSegment(sketch, "E345", {"start": v(-8.08, 39.36) * mm, "end": v(-10.02, 38.92) * mm});
            skLineSegment(sketch, "E346", {"start": v(-10.02, 38.92) * mm, "end": v(-11.93, 38.37) * mm});
            skLineSegment(sketch, "E347", {"start": v(-11.93, 38.37) * mm, "end": v(-13.8, 37.74) * mm});
            skLineSegment(sketch, "E348", {"start": v(-13.8, 37.74) * mm, "end": v(-15.62, 37.02) * mm});
            skLineSegment(sketch, "E349", {"start": v(-15.62, 37.02) * mm, "end": v(-17.4, 36.22) * mm});
            skLineSegment(sketch, "E350", {"start": v(-17.4, 36.22) * mm, "end": v(-19.13, 35.33) * mm});
            skLineSegment(sketch, "E351", {"start": v(-19.13, 35.33) * mm, "end": v(-20.82, 34.36) * mm});
            skLineSegment(sketch, "E352", {"start": v(-20.82, 34.36) * mm, "end": v(-22.45, 33.32) * mm});
            skLineSegment(sketch, "E353", {"start": v(-22.45, 33.32) * mm, "end": v(-24.02, 32.2) * mm});
            skLineSegment(sketch, "E354", {"start": v(-24.02, 32.2) * mm, "end": v(-25.54, 31) * mm});
            skLineSegment(sketch, "E355", {"start": v(-25.54, 31) * mm, "end": v(-27, 29.74) * mm});
            skLineSegment(sketch, "E356", {"start": v(-27, 29.74) * mm, "end": v(-28.4, 28.41) * mm});
            skLineSegment(sketch, "E357", {"start": v(-28.4, 28.41) * mm, "end": v(-29.73, 27.02) * mm});
            skLineSegment(sketch, "E358", {"start": v(-29.73, 27.02) * mm, "end": v(-31, 25.56) * mm});
            skLineSegment(sketch, "E359", {"start": v(-31, 25.56) * mm, "end": v(-32.19, 24.04) * mm});
            skLineSegment(sketch, "E360", {"start": v(-32.19, 24.04) * mm, "end": v(-33.3, 22.46) * mm});
            skLineSegment(sketch, "E361", {"start": v(-33.3, 22.46) * mm, "end": v(-34.35, 20.83) * mm});
            skLineSegment(sketch, "E362", {"start": v(-34.35, 20.83) * mm, "end": v(-35.32, 19.15) * mm});
            skLineSegment(sketch, "E363", {"start": v(-35.32, 19.15) * mm, "end": v(-36.21, 17.41) * mm});
            skLineSegment(sketch, "E364", {"start": v(-36.21, 17.41) * mm, "end": v(-37.02, 15.63) * mm});
            skLineSegment(sketch, "E365", {"start": v(-37.02, 15.63) * mm, "end": v(-37.74, 13.8) * mm});
            skLineSegment(sketch, "E366", {"start": v(-37.74, 13.8) * mm, "end": v(-38.37, 11.94) * mm});
            skLineSegment(sketch, "E367", {"start": v(-38.37, 11.94) * mm, "end": v(-38.91, 10.03) * mm});
            skLineSegment(sketch, "E368", {"start": v(-38.91, 10.03) * mm, "end": v(-39.36, 8.09) * mm});
            skLineSegment(sketch, "E369", {"start": v(-39.36, 8.09) * mm, "end": v(-39.72, 6.1) * mm});
            skLineSegment(sketch, "E370", {"start": v(-39.72, 6.1) * mm, "end": v(-39.97, 4.1) * mm});
            skLineSegment(sketch, "E371", {"start": v(-39.97, 4.1) * mm, "end": v(-40.13, 2.05) * mm});
            skLineSegment(sketch, "E372", {"start": v(-40.13, 2.05) * mm, "end": v(-40.18, 0.5) * mm});
            skLineSegment(sketch, "E373", {"start": v(-40.18, 0.5) * mm, "end": v(-40.18, -0.02) * mm});
            skLineSegment(sketch, "E374", {"start": v(-40.18, -0.02) * mm, "end": v(-40.18, -0.54) * mm});
            skLineSegment(sketch, "E375", {"start": v(-40.18, -0.54) * mm, "end": v(-40.13, -2.08) * mm});
            skLineSegment(sketch, "E376", {"start": v(-40.13, -2.08) * mm, "end": v(-39.97, -4.12) * mm});
            skLineSegment(sketch, "E377", {"start": v(-39.97, -4.12) * mm, "end": v(-39.72, -6.13) * mm});
            skLineSegment(sketch, "E378", {"start": v(-39.72, -6.13) * mm, "end": v(-39.36, -8.11) * mm});
            skLineSegment(sketch, "E379", {"start": v(-39.36, -8.11) * mm, "end": v(-38.91, -10.05) * mm});
            skLineSegment(sketch, "E380", {"start": v(-38.91, -10.05) * mm, "end": v(-38.37, -11.96) * mm});
            skLineSegment(sketch, "E381", {"start": v(-38.37, -11.96) * mm, "end": v(-37.74, -13.83) * mm});
            skLineSegment(sketch, "E382", {"start": v(-37.74, -13.83) * mm, "end": v(-37.02, -15.65) * mm});
            skLineSegment(sketch, "E383", {"start": v(-37.02, -15.65) * mm, "end": v(-36.21, -17.43) * mm});
            skLineSegment(sketch, "E384", {"start": v(-36.21, -17.43) * mm, "end": v(-35.32, -19.16) * mm});
            skLineSegment(sketch, "E385", {"start": v(-35.32, -19.16) * mm, "end": v(-34.35, -20.84) * mm});
            skLineSegment(sketch, "E386", {"start": v(-34.35, -20.84) * mm, "end": v(-33.3, -22.47) * mm});
            skLineSegment(sketch, "E387", {"start": v(-33.3, -22.47) * mm, "end": v(-32.19, -24.05) * mm});
            skLineSegment(sketch, "E388", {"start": v(-32.19, -24.05) * mm, "end": v(-31, -25.56) * mm});
            skLineSegment(sketch, "E389", {"start": v(-31, -25.56) * mm, "end": v(-29.73, -27.02) * mm});
            skLineSegment(sketch, "E390", {"start": v(-29.73, -27.02) * mm, "end": v(-28.4, -28.42) * mm});
            skLineSegment(sketch, "E391", {"start": v(-28.4, -28.42) * mm, "end": v(-27, -29.74) * mm});
            skLineSegment(sketch, "E392", {"start": v(-27, -29.74) * mm, "end": v(-25.54, -31) * mm});
            skLineSegment(sketch, "E393", {"start": v(-25.54, -31) * mm, "end": v(-24.02, -32.2) * mm});
            skLineSegment(sketch, "E394", {"start": v(-24.02, -32.2) * mm, "end": v(-22.45, -33.32) * mm});
            skLineSegment(sketch, "E395", {"start": v(-22.45, -33.32) * mm, "end": v(-20.82, -34.36) * mm});
            skLineSegment(sketch, "E396", {"start": v(-20.82, -34.36) * mm, "end": v(-19.13, -35.33) * mm});
            skLineSegment(sketch, "E397", {"start": v(-19.13, -35.33) * mm, "end": v(-17.4, -36.22) * mm});
            skLineSegment(sketch, "E398", {"start": v(-17.4, -36.22) * mm, "end": v(-15.62, -37.02) * mm});
            skLineSegment(sketch, "E399", {"start": v(-15.62, -37.02) * mm, "end": v(-13.8, -37.74) * mm});
            skLineSegment(sketch, "E400", {"start": v(-13.8, -37.74) * mm, "end": v(-11.93, -38.37) * mm});
            skLineSegment(sketch, "E401", {"start": v(-11.93, -38.37) * mm, "end": v(-10.02, -38.91) * mm});
            skLineSegment(sketch, "E402", {"start": v(-10.02, -38.91) * mm, "end": v(-8.08, -39.36) * mm});
            skLineSegment(sketch, "E403", {"start": v(-8.08, -39.36) * mm, "end": v(-6.1, -39.72) * mm});
            skLineSegment(sketch, "E404", {"start": v(-6.1, -39.72) * mm, "end": v(-4.09, -39.97) * mm});
            skLineSegment(sketch, "E405", {"start": v(-4.09, -39.97) * mm, "end": v(-2.05, -40.13) * mm});
            skLineSegment(sketch, "E406", {"start": v(-2.05, -40.13) * mm, "end": v(-0.5, -40.18) * mm});
            skLineSegment(sketch, "E407", {"start": v(-0.5, -40.18) * mm, "end": v(0.02, -40.18) * mm});
            skLineSegment(sketch, "E408", {"start": v(0.02, -25.1) * mm, "end": v(0.34, -25.1) * mm});
            skLineSegment(sketch, "E409", {"start": v(0.34, -25.1) * mm, "end": v(1.31, -25.07) * mm});
            skLineSegment(sketch, "E410", {"start": v(1.31, -25.07) * mm, "end": v(2.59, -24.97) * mm});
            skLineSegment(sketch, "E411", {"start": v(2.59, -24.97) * mm, "end": v(3.84, -24.81) * mm});
            skLineSegment(sketch, "E412", {"start": v(3.84, -24.81) * mm, "end": v(5.08, -24.59) * mm});
            skLineSegment(sketch, "E413", {"start": v(5.08, -24.59) * mm, "end": v(6.3, -24.3) * mm});
            skLineSegment(sketch, "E414", {"start": v(6.3, -24.3) * mm, "end": v(7.48, -23.97) * mm});
            skLineSegment(sketch, "E415", {"start": v(7.48, -23.97) * mm, "end": v(8.65, -23.58) * mm});
            skLineSegment(sketch, "E416", {"start": v(8.65, -23.58) * mm, "end": v(9.79, -23.13) * mm});
            skLineSegment(sketch, "E417", {"start": v(9.79, -23.13) * mm, "end": v(10.9, -22.62) * mm});
            skLineSegment(sketch, "E418", {"start": v(10.9, -22.62) * mm, "end": v(11.98, -22.07) * mm});
            skLineSegment(sketch, "E419", {"start": v(11.98, -22.07) * mm, "end": v(13.03, -21.46) * mm});
            skLineSegment(sketch, "E420", {"start": v(13.03, -21.46) * mm, "end": v(14.05, -20.81) * mm});
            skLineSegment(sketch, "E421", {"start": v(14.05, -20.81) * mm, "end": v(15.03, -20.11) * mm});
            skLineSegment(sketch, "E422", {"start": v(15.03, -20.11) * mm, "end": v(15.98, -19.37) * mm});
            skLineSegment(sketch, "E423", {"start": v(15.98, -19.37) * mm, "end": v(16.89, -18.58) * mm});
            skLineSegment(sketch, "E424", {"start": v(16.89, -18.58) * mm, "end": v(17.76, -17.75) * mm});
            skLineSegment(sketch, "E425", {"start": v(17.76, -17.75) * mm, "end": v(18.59, -16.87) * mm});
            skLineSegment(sketch, "E426", {"start": v(18.59, -16.87) * mm, "end": v(19.38, -15.96) * mm});
            skLineSegment(sketch, "E427", {"start": v(19.38, -15.96) * mm, "end": v(20.12, -15.02) * mm});
            skLineSegment(sketch, "E428", {"start": v(20.12, -15.02) * mm, "end": v(20.82, -14.03) * mm});
            skLineSegment(sketch, "E429", {"start": v(20.82, -14.03) * mm, "end": v(21.47, -13.01) * mm});
            skLineSegment(sketch, "E430", {"start": v(21.47, -13.01) * mm, "end": v(22.08, -11.96) * mm});
            skLineSegment(sketch, "E431", {"start": v(22.08, -11.96) * mm, "end": v(22.63, -10.88) * mm});
            skLineSegment(sketch, "E432", {"start": v(22.63, -10.88) * mm, "end": v(23.13, -9.77) * mm});
            skLineSegment(sketch, "E433", {"start": v(23.13, -9.77) * mm, "end": v(23.58, -8.63) * mm});
            skLineSegment(sketch, "E434", {"start": v(23.58, -8.63) * mm, "end": v(23.97, -7.47) * mm});
            skLineSegment(sketch, "E435", {"start": v(23.97, -7.47) * mm, "end": v(24.31, -6.28) * mm});
            skLineSegment(sketch, "E436", {"start": v(24.31, -6.28) * mm, "end": v(24.6, -5.07) * mm});
            skLineSegment(sketch, "E437", {"start": v(24.6, -5.07) * mm, "end": v(24.81, -3.83) * mm});
            skLineSegment(sketch, "E438", {"start": v(24.81, -3.83) * mm, "end": v(24.97, -2.58) * mm});
            skLineSegment(sketch, "E439", {"start": v(24.97, -2.58) * mm, "end": v(25.07, -1.3) * mm});
            skLineSegment(sketch, "E440", {"start": v(25.07, -1.3) * mm, "end": v(25.1, -0.34) * mm});
            skLineSegment(sketch, "E441", {"start": v(25.1, -0.34) * mm, "end": v(25.1, -0.02) * mm});
            skLineSegment(sketch, "E442", {"start": v(25.1, -0.02) * mm, "end": v(25.1, 0.3) * mm});
            skLineSegment(sketch, "E443", {"start": v(25.1, 0.3) * mm, "end": v(25.07, 1.27) * mm});
            skLineSegment(sketch, "E444", {"start": v(25.07, 1.27) * mm, "end": v(24.97, 2.55) * mm});
            skLineSegment(sketch, "E445", {"start": v(24.97, 2.55) * mm, "end": v(24.81, 3.8) * mm});
            skLineSegment(sketch, "E446", {"start": v(24.81, 3.8) * mm, "end": v(24.6, 5.04) * mm});
            skLineSegment(sketch, "E447", {"start": v(24.6, 5.04) * mm, "end": v(24.31, 6.26) * mm});
            skLineSegment(sketch, "E448", {"start": v(24.31, 6.26) * mm, "end": v(23.97, 7.45) * mm});
            skLineSegment(sketch, "E449", {"start": v(23.97, 7.45) * mm, "end": v(23.58, 8.62) * mm});
            skLineSegment(sketch, "E450", {"start": v(23.58, 8.62) * mm, "end": v(23.13, 9.76) * mm});
            skLineSegment(sketch, "E451", {"start": v(23.13, 9.76) * mm, "end": v(22.63, 10.87) * mm});
            skLineSegment(sketch, "E452", {"start": v(22.63, 10.87) * mm, "end": v(22.08, 11.95) * mm});
            skLineSegment(sketch, "E453", {"start": v(22.08, 11.95) * mm, "end": v(21.47, 13) * mm});
            skLineSegment(sketch, "E454", {"start": v(21.47, 13) * mm, "end": v(20.82, 14.02) * mm});
            skLineSegment(sketch, "E455", {"start": v(20.82, 14.02) * mm, "end": v(20.12, 15) * mm});
            skLineSegment(sketch, "E456", {"start": v(20.12, 15) * mm, "end": v(19.38, 15.96) * mm});
            skLineSegment(sketch, "E457", {"start": v(19.38, 15.96) * mm, "end": v(18.59, 16.87) * mm});
            skLineSegment(sketch, "E458", {"start": v(18.59, 16.87) * mm, "end": v(17.76, 17.74) * mm});
            skLineSegment(sketch, "E459", {"start": v(17.76, 17.74) * mm, "end": v(16.89, 18.57) * mm});
            skLineSegment(sketch, "E460", {"start": v(16.89, 18.57) * mm, "end": v(15.98, 19.36) * mm});
            skLineSegment(sketch, "E461", {"start": v(15.98, 19.36) * mm, "end": v(15.03, 20.1) * mm});
            skLineSegment(sketch, "E462", {"start": v(15.03, 20.1) * mm, "end": v(14.05, 20.8) * mm});
            skLineSegment(sketch, "E463", {"start": v(14.05, 20.8) * mm, "end": v(13.03, 21.46) * mm});
            skLineSegment(sketch, "E464", {"start": v(13.03, 21.46) * mm, "end": v(11.98, 22.07) * mm});
            skLineSegment(sketch, "E465", {"start": v(11.98, 22.07) * mm, "end": v(10.9, 22.62) * mm});
            skLineSegment(sketch, "E466", {"start": v(10.9, 22.62) * mm, "end": v(9.79, 23.13) * mm});
            skLineSegment(sketch, "E467", {"start": v(9.79, 23.13) * mm, "end": v(8.65, 23.58) * mm});
            skLineSegment(sketch, "E468", {"start": v(8.65, 23.58) * mm, "end": v(7.48, 23.97) * mm});
            skLineSegment(sketch, "E469", {"start": v(7.48, 23.97) * mm, "end": v(6.3, 24.3) * mm});
            skLineSegment(sketch, "E470", {"start": v(6.3, 24.3) * mm, "end": v(5.08, 24.6) * mm});
            skLineSegment(sketch, "E471", {"start": v(5.08, 24.6) * mm, "end": v(3.84, 24.81) * mm});
            skLineSegment(sketch, "E472", {"start": v(3.84, 24.81) * mm, "end": v(2.59, 24.97) * mm});
            skLineSegment(sketch, "E473", {"start": v(2.59, 24.97) * mm, "end": v(1.31, 25.07) * mm});
            skLineSegment(sketch, "E474", {"start": v(1.31, 25.07) * mm, "end": v(0.34, 25.1) * mm});
            skLineSegment(sketch, "E475", {"start": v(0.34, 25.1) * mm, "end": v(0.02, 25.1) * mm});
            skLineSegment(sketch, "E476", {"start": v(0.02, 25.1) * mm, "end": v(-0.3, 25.1) * mm});
            skLineSegment(sketch, "E477", {"start": v(-0.3, 25.1) * mm, "end": v(-1.27, 25.07) * mm});
            skLineSegment(sketch, "E478", {"start": v(-1.27, 25.07) * mm, "end": v(-2.55, 24.97) * mm});
            skLineSegment(sketch, "E479", {"start": v(-2.55, 24.97) * mm, "end": v(-3.8, 24.81) * mm});
            skLineSegment(sketch, "E480", {"start": v(-3.8, 24.81) * mm, "end": v(-5.04, 24.6) * mm});
            skLineSegment(sketch, "E481", {"start": v(-5.04, 24.6) * mm, "end": v(-6.26, 24.3) * mm});
            skLineSegment(sketch, "E482", {"start": v(-6.26, 24.3) * mm, "end": v(-7.45, 23.97) * mm});
            skLineSegment(sketch, "E483", {"start": v(-7.45, 23.97) * mm, "end": v(-8.62, 23.58) * mm});
            skLineSegment(sketch, "E484", {"start": v(-8.62, 23.58) * mm, "end": v(-9.76, 23.13) * mm});
            skLineSegment(sketch, "E485", {"start": v(-9.76, 23.13) * mm, "end": v(-10.87, 22.62) * mm});
            skLineSegment(sketch, "E486", {"start": v(-10.87, 22.62) * mm, "end": v(-11.95, 22.07) * mm});
            skLineSegment(sketch, "E487", {"start": v(-11.95, 22.07) * mm, "end": v(-13, 21.46) * mm});
            skLineSegment(sketch, "E488", {"start": v(-13, 21.46) * mm, "end": v(-14.02, 20.8) * mm});
            skLineSegment(sketch, "E489", {"start": v(-14.02, 20.8) * mm, "end": v(-15, 20.1) * mm});
            skLineSegment(sketch, "E490", {"start": v(-15, 20.1) * mm, "end": v(-15.96, 19.36) * mm});
            skLineSegment(sketch, "E491", {"start": v(-15.96, 19.36) * mm, "end": v(-16.87, 18.57) * mm});
            skLineSegment(sketch, "E492", {"start": v(-16.87, 18.57) * mm, "end": v(-17.74, 17.74) * mm});
            skLineSegment(sketch, "E493", {"start": v(-17.74, 17.74) * mm, "end": v(-18.57, 16.87) * mm});
            skLineSegment(sketch, "E494", {"start": v(-18.57, 16.87) * mm, "end": v(-19.36, 15.96) * mm});
            skLineSegment(sketch, "E495", {"start": v(-19.36, 15.96) * mm, "end": v(-20.1, 15) * mm});
            skLineSegment(sketch, "E496", {"start": v(-20.1, 15) * mm, "end": v(-20.8, 14.02) * mm});
            skLineSegment(sketch, "E497", {"start": v(-20.8, 14.02) * mm, "end": v(-21.46, 13) * mm});
            skLineSegment(sketch, "E498", {"start": v(-21.46, 13) * mm, "end": v(-22.07, 11.95) * mm});
            skLineSegment(sketch, "E499", {"start": v(-22.07, 11.95) * mm, "end": v(-22.62, 10.87) * mm});
            skLineSegment(sketch, "E500", {"start": v(-22.62, 10.87) * mm, "end": v(-23.13, 9.76) * mm});
            skLineSegment(sketch, "E501", {"start": v(-23.13, 9.76) * mm, "end": v(-23.58, 8.62) * mm});
            skLineSegment(sketch, "E502", {"start": v(-23.58, 8.62) * mm, "end": v(-23.97, 7.45) * mm});
            skLineSegment(sketch, "E503", {"start": v(-23.97, 7.45) * mm, "end": v(-24.3, 6.26) * mm});
            skLineSegment(sketch, "E504", {"start": v(-24.3, 6.26) * mm, "end": v(-24.6, 5.04) * mm});
            skLineSegment(sketch, "E505", {"start": v(-24.6, 5.04) * mm, "end": v(-24.81, 3.8) * mm});
            skLineSegment(sketch, "E506", {"start": v(-24.81, 3.8) * mm, "end": v(-24.97, 2.55) * mm});
            skLineSegment(sketch, "E507", {"start": v(-24.97, 2.55) * mm, "end": v(-25.07, 1.27) * mm});
            skLineSegment(sketch, "E508", {"start": v(-25.07, 1.27) * mm, "end": v(-25.1, 0.3) * mm});
            skLineSegment(sketch, "E509", {"start": v(-25.1, 0.3) * mm, "end": v(-25.1, -0.02) * mm});
            skLineSegment(sketch, "E510", {"start": v(-25.1, -0.02) * mm, "end": v(-25.1, -0.34) * mm});
            skLineSegment(sketch, "E511", {"start": v(-25.1, -0.34) * mm, "end": v(-25.07, -1.3) * mm});
            skLineSegment(sketch, "E512", {"start": v(-25.07, -1.3) * mm, "end": v(-24.97, -2.58) * mm});
            skLineSegment(sketch, "E513", {"start": v(-24.97, -2.58) * mm, "end": v(-24.81, -3.83) * mm});
            skLineSegment(sketch, "E514", {"start": v(-24.81, -3.83) * mm, "end": v(-24.6, -5.07) * mm});
            skLineSegment(sketch, "E515", {"start": v(-24.6, -5.07) * mm, "end": v(-24.3, -6.28) * mm});
            skLineSegment(sketch, "E516", {"start": v(-24.3, -6.28) * mm, "end": v(-23.97, -7.47) * mm});
            skLineSegment(sketch, "E517", {"start": v(-23.97, -7.47) * mm, "end": v(-23.58, -8.63) * mm});
            skLineSegment(sketch, "E518", {"start": v(-23.58, -8.63) * mm, "end": v(-23.13, -9.77) * mm});
            skLineSegment(sketch, "E519", {"start": v(-23.13, -9.77) * mm, "end": v(-22.62, -10.88) * mm});
            skLineSegment(sketch, "E520", {"start": v(-22.62, -10.88) * mm, "end": v(-22.07, -11.96) * mm});
            skLineSegment(sketch, "E521", {"start": v(-22.07, -11.96) * mm, "end": v(-21.46, -13.01) * mm});
            skLineSegment(sketch, "E522", {"start": v(-21.46, -13.01) * mm, "end": v(-20.8, -14.03) * mm});
            skLineSegment(sketch, "E523", {"start": v(-20.8, -14.03) * mm, "end": v(-20.1, -15.02) * mm});
            skLineSegment(sketch, "E524", {"start": v(-20.1, -15.02) * mm, "end": v(-19.36, -15.96) * mm});
            skLineSegment(sketch, "E525", {"start": v(-19.36, -15.96) * mm, "end": v(-18.57, -16.87) * mm});
            skLineSegment(sketch, "E526", {"start": v(-18.57, -16.87) * mm, "end": v(-17.74, -17.75) * mm});
            skLineSegment(sketch, "E527", {"start": v(-17.74, -17.75) * mm, "end": v(-16.87, -18.58) * mm});
            skLineSegment(sketch, "E528", {"start": v(-16.87, -18.58) * mm, "end": v(-15.96, -19.37) * mm});
            skLineSegment(sketch, "E529", {"start": v(-15.96, -19.37) * mm, "end": v(-15, -20.11) * mm});
            skLineSegment(sketch, "E530", {"start": v(-15, -20.11) * mm, "end": v(-14.02, -20.81) * mm});
            skLineSegment(sketch, "E531", {"start": v(-14.02, -20.81) * mm, "end": v(-13, -21.46) * mm});
            skLineSegment(sketch, "E532", {"start": v(-13, -21.46) * mm, "end": v(-11.95, -22.07) * mm});
            skLineSegment(sketch, "E533", {"start": v(-11.95, -22.07) * mm, "end": v(-10.87, -22.62) * mm});
            skLineSegment(sketch, "E534", {"start": v(-10.87, -22.62) * mm, "end": v(-9.76, -23.13) * mm});
            skLineSegment(sketch, "E535", {"start": v(-9.76, -23.13) * mm, "end": v(-8.62, -23.58) * mm});
            skLineSegment(sketch, "E536", {"start": v(-8.62, -23.58) * mm, "end": v(-7.45, -23.97) * mm});
            skLineSegment(sketch, "E537", {"start": v(-7.45, -23.97) * mm, "end": v(-6.26, -24.3) * mm});
            skLineSegment(sketch, "E538", {"start": v(-6.26, -24.3) * mm, "end": v(-5.04, -24.59) * mm});
            skLineSegment(sketch, "E539", {"start": v(-5.04, -24.59) * mm, "end": v(-3.8, -24.81) * mm});
            skLineSegment(sketch, "E540", {"start": v(-3.8, -24.81) * mm, "end": v(-2.55, -24.97) * mm});
            skLineSegment(sketch, "E541", {"start": v(-2.55, -24.97) * mm, "end": v(-1.27, -25.07) * mm});
            skLineSegment(sketch, "E542", {"start": v(-1.27, -25.07) * mm, "end": v(-0.3, -25.1) * mm});
            skLineSegment(sketch, "E543", {"start": v(-0.3, -25.1) * mm, "end": v(0.02, -25.1) * mm});
            skLineSegment(sketch, "E544", {"start": v(4.65, 36.13) * mm, "end": v(4.75, 36) * mm});
            skLineSegment(sketch, "E545", {"start": v(4.75, 36) * mm, "end": v(5.01, 35.54) * mm});
            skLineSegment(sketch, "E546", {"start": v(5.01, 35.54) * mm, "end": v(5.29, 34.9) * mm});
            skLineSegment(sketch, "E547", {"start": v(5.29, 34.9) * mm, "end": v(5.49, 34.24) * mm});
            skLineSegment(sketch, "E548", {"start": v(5.49, 34.24) * mm, "end": v(5.62, 33.54) * mm});
            skLineSegment(sketch, "E549", {"start": v(5.62, 33.54) * mm, "end": v(5.7, 32.83) * mm});
            skLineSegment(sketch, "E550", {"start": v(5.7, 32.83) * mm, "end": v(5.7, 32.12) * mm});
            skLineSegment(sketch, "E551", {"start": v(5.7, 32.12) * mm, "end": v(5.66, 31.42) * mm});
            skLineSegment(sketch, "E552", {"start": v(5.66, 31.42) * mm, "end": v(5.6, 30.9) * mm});
            skLineSegment(sketch, "E553", {"start": v(5.6, 30.9) * mm, "end": v(5.57, 30.73) * mm});
            skLineSegment(sketch, "E554", {"start": v(5.57, 30.73) * mm, "end": v(5.54, 30.58) * mm});
            skLineSegment(sketch, "E555", {"start": v(5.54, 30.58) * mm, "end": v(5.4, 30.14) * mm});
            skLineSegment(sketch, "E556", {"start": v(5.4, 30.14) * mm, "end": v(5.15, 29.6) * mm});
            skLineSegment(sketch, "E557", {"start": v(5.15, 29.6) * mm, "end": v(4.82, 29.13) * mm});
            skLineSegment(sketch, "E558", {"start": v(4.82, 29.13) * mm, "end": v(4.43, 28.7) * mm});
            skLineSegment(sketch, "E559", {"start": v(4.43, 28.7) * mm, "end": v(3.99, 28.34) * mm});
            skLineSegment(sketch, "E560", {"start": v(3.99, 28.34) * mm, "end": v(3.5, 28.03) * mm});
            skLineSegment(sketch, "E561", {"start": v(3.5, 28.03) * mm, "end": v(2.96, 27.77) * mm});
            skLineSegment(sketch, "E562", {"start": v(2.96, 27.77) * mm, "end": v(2.55, 27.6) * mm});
            skLineSegment(sketch, "E563", {"start": v(2.55, 27.6) * mm, "end": v(2.4, 27.56) * mm});
            skLineSegment(sketch, "E564", {"start": v(2.4, 27.56) * mm, "end": v(2.18, 27.54) * mm});
            skLineSegment(sketch, "E565", {"start": v(2.18, 27.54) * mm, "end": v(1.5, 27.45) * mm});
            skLineSegment(sketch, "E566", {"start": v(1.5, 27.45) * mm, "end": v(0.57, 27.34) * mm});
            skLineSegment(sketch, "E567", {"start": v(0.57, 27.34) * mm, "end": v(-0.39, 27.27) * mm});
            skLineSegment(sketch, "E568", {"start": v(-0.39, 27.27) * mm, "end": v(-1.35, 27.3) * mm});
            skLineSegment(sketch, "E569", {"start": v(-1.35, 27.3) * mm, "end": v(-2.3, 27.43) * mm});
            skLineSegment(sketch, "E570", {"start": v(-2.3, 27.43) * mm, "end": v(-3.21, 27.73) * mm});
            skLineSegment(sketch, "E571", {"start": v(-3.21, 27.73) * mm, "end": v(-4.09, 28.21) * mm});
            skLineSegment(sketch, "E572", {"start": v(-4.09, 28.21) * mm, "end": v(-4.72, 28.73) * mm});
            skLineSegment(sketch, "E573", {"start": v(-4.72, 28.73) * mm, "end": v(-4.9, 28.93) * mm});
            skLineSegment(sketch, "E574", {"start": v(-4.9, 28.93) * mm, "end": v(-5.02, 29.08) * mm});
            skLineSegment(sketch, "E575", {"start": v(-5.02, 29.08) * mm, "end": v(-5.3, 29.57) * mm});
            skLineSegment(sketch, "E576", {"start": v(-5.3, 29.57) * mm, "end": v(-5.58, 30.24) * mm});
            skLineSegment(sketch, "E577", {"start": v(-5.58, 30.24) * mm, "end": v(-5.78, 30.95) * mm});
            skLineSegment(sketch, "E578", {"start": v(-5.78, 30.95) * mm, "end": v(-5.88, 31.68) * mm});
            skLineSegment(sketch, "E579", {"start": v(-5.88, 31.68) * mm, "end": v(-5.92, 32.44) * mm});
            skLineSegment(sketch, "E580", {"start": v(-5.92, 32.44) * mm, "end": v(-5.88, 33.2) * mm});
            skLineSegment(sketch, "E581", {"start": v(-5.88, 33.2) * mm, "end": v(-5.79, 33.99) * mm});
            skLineSegment(sketch, "E582", {"start": v(-5.79, 33.99) * mm, "end": v(-5.69, 34.58) * mm});
            skLineSegment(sketch, "E583", {"start": v(-5.69, 34.58) * mm, "end": v(-5.65, 34.77) * mm});
            skLineSegment(sketch, "E584", {"start": v(-5.65, 34.77) * mm, "end": v(-5.6, 34.97) * mm});
            skLineSegment(sketch, "E585", {"start": v(-5.6, 34.97) * mm, "end": v(-5.34, 35.54) * mm});
            skLineSegment(sketch, "E586", {"start": v(-5.34, 35.54) * mm, "end": v(-4.87, 36.16) * mm});
            skLineSegment(sketch, "E587", {"start": v(-4.87, 36.16) * mm, "end": v(-4.28, 36.66) * mm});
            skLineSegment(sketch, "E588", {"start": v(-4.28, 36.66) * mm, "end": v(-3.58, 37.05) * mm});
            skLineSegment(sketch, "E589", {"start": v(-3.58, 37.05) * mm, "end": v(-2.82, 37.34) * mm});
            skLineSegment(sketch, "E590", {"start": v(-2.82, 37.34) * mm, "end": v(-2, 37.54) * mm});
            skLineSegment(sketch, "E591", {"start": v(-2, 37.54) * mm, "end": v(-1.19, 37.67) * mm});
            skLineSegment(sketch, "E592", {"start": v(-1.19, 37.67) * mm, "end": v(-0.59, 37.74) * mm});
            skLineSegment(sketch, "E593", {"start": v(-0.59, 37.74) * mm, "end": v(-0.39, 37.75) * mm});
            skLineSegment(sketch, "E594", {"start": v(-0.39, 37.75) * mm, "end": v(-0.21, 37.75) * mm});
            skLineSegment(sketch, "E595", {"start": v(-0.21, 37.75) * mm, "end": v(0.3, 37.74) * mm});
            skLineSegment(sketch, "E596", {"start": v(0.3, 37.74) * mm, "end": v(1, 37.69) * mm});
            skLineSegment(sketch, "E597", {"start": v(1, 37.69) * mm, "end": v(1.67, 37.6) * mm});
            skLineSegment(sketch, "E598", {"start": v(1.67, 37.6) * mm, "end": v(2.33, 37.44) * mm});
            skLineSegment(sketch, "E599", {"start": v(2.33, 37.44) * mm, "end": v(2.96, 37.23) * mm});
            skLineSegment(sketch, "E600", {"start": v(2.96, 37.23) * mm, "end": v(3.57, 36.95) * mm});
            skLineSegment(sketch, "E601", {"start": v(3.57, 36.95) * mm, "end": v(4.13, 36.58) * mm});
            skLineSegment(sketch, "E602", {"start": v(4.13, 36.58) * mm, "end": v(4.53, 36.26) * mm});
            skLineSegment(sketch, "E603", {"start": v(4.53, 36.26) * mm, "end": v(4.65, 36.13) * mm});
            skLineSegment(sketch, "E604", {"start": v(1.97, 34.3) * mm, "end": v(1.98, 34.16) * mm});
            skLineSegment(sketch, "E605", {"start": v(1.98, 34.16) * mm, "end": v(2.03, 33.75) * mm});
            skLineSegment(sketch, "E606", {"start": v(2.03, 33.75) * mm, "end": v(2.1, 33.16) * mm});
            skLineSegment(sketch, "E607", {"start": v(2.1, 33.16) * mm, "end": v(2.16, 32.54) * mm});
            skLineSegment(sketch, "E608", {"start": v(2.16, 32.54) * mm, "end": v(2.19, 31.9) * mm});
            skLineSegment(sketch, "E609", {"start": v(2.19, 31.9) * mm, "end": v(2.16, 31.29) * mm});
            skLineSegment(sketch, "E610", {"start": v(2.16, 31.29) * mm, "end": v(2.05, 30.7) * mm});
            skLineSegment(sketch, "E611", {"start": v(2.05, 30.7) * mm, "end": v(1.85, 30.14) * mm});
            skLineSegment(sketch, "E612", {"start": v(1.85, 30.14) * mm, "end": v(1.62, 29.77) * mm});
            skLineSegment(sketch, "E613", {"start": v(1.62, 29.77) * mm, "end": v(1.53, 29.66) * mm});
            skLineSegment(sketch, "E614", {"start": v(1.53, 29.66) * mm, "end": v(1.44, 29.6) * mm});
            skLineSegment(sketch, "E615", {"start": v(1.44, 29.6) * mm, "end": v(1.17, 29.43) * mm});
            skLineSegment(sketch, "E616", {"start": v(1.17, 29.43) * mm, "end": v(0.78, 29.25) * mm});
            skLineSegment(sketch, "E617", {"start": v(0.78, 29.25) * mm, "end": v(0.38, 29.11) * mm});
            skLineSegment(sketch, "E618", {"start": v(0.38, 29.11) * mm, "end": v(-0.04, 29.03) * mm});
            skLineSegment(sketch, "E619", {"start": v(-0.04, 29.03) * mm, "end": v(-0.45, 29.01) * mm});
            skLineSegment(sketch, "E620", {"start": v(-0.45, 29.01) * mm, "end": v(-0.85, 29.06) * mm});
            skLineSegment(sketch, "E621", {"start": v(-0.85, 29.06) * mm, "end": v(-1.24, 29.17) * mm});
            skLineSegment(sketch, "E622", {"start": v(-1.24, 29.17) * mm, "end": v(-1.52, 29.3) * mm});
            skLineSegment(sketch, "E623", {"start": v(-1.52, 29.3) * mm, "end": v(-1.6, 29.37) * mm});
            skLineSegment(sketch, "E624", {"start": v(-1.6, 29.37) * mm, "end": v(-1.7, 29.47) * mm});
            skLineSegment(sketch, "E625", {"start": v(-1.7, 29.47) * mm, "end": v(-2, 29.84) * mm});
            skLineSegment(sketch, "E626", {"start": v(-2, 29.84) * mm, "end": v(-2.27, 30.35) * mm});
            skLineSegment(sketch, "E627", {"start": v(-2.27, 30.35) * mm, "end": v(-2.44, 30.9) * mm});
            skLineSegment(sketch, "E628", {"start": v(-2.44, 30.9) * mm, "end": v(-2.53, 31.49) * mm});
            skLineSegment(sketch, "E629", {"start": v(-2.53, 31.49) * mm, "end": v(-2.55, 32.08) * mm});
            skLineSegment(sketch, "E630", {"start": v(-2.55, 32.08) * mm, "end": v(-2.51, 32.68) * mm});
            skLineSegment(sketch, "E631", {"start": v(-2.51, 32.68) * mm, "end": v(-2.44, 33.28) * mm});
            skLineSegment(sketch, "E632", {"start": v(-2.44, 33.28) * mm, "end": v(-2.36, 33.71) * mm});
            skLineSegment(sketch, "E633", {"start": v(-2.36, 33.71) * mm, "end": v(-2.34, 33.85) * mm});
            skLineSegment(sketch, "E634", {"start": v(-2.34, 33.85) * mm, "end": v(-2.32, 33.94) * mm});
            skLineSegment(sketch, "E635", {"start": v(-2.32, 33.94) * mm, "end": v(-2.26, 34.19) * mm});
            skLineSegment(sketch, "E636", {"start": v(-2.26, 34.19) * mm, "end": v(-2.14, 34.51) * mm});
            skLineSegment(sketch, "E637", {"start": v(-2.14, 34.51) * mm, "end": v(-1.99, 34.82) * mm});
            skLineSegment(sketch, "E638", {"start": v(-1.99, 34.82) * mm, "end": v(-1.8, 35.1) * mm});
            skLineSegment(sketch, "E639", {"start": v(-1.8, 35.1) * mm, "end": v(-1.57, 35.35) * mm});
            skLineSegment(sketch, "E640", {"start": v(-1.57, 35.35) * mm, "end": v(-1.3, 35.56) * mm});
            skLineSegment(sketch, "E641", {"start": v(-1.3, 35.56) * mm, "end": v(-1, 35.71) * mm});
            skLineSegment(sketch, "E642", {"start": v(-1, 35.71) * mm, "end": v(-0.76, 35.79) * mm});
            skLineSegment(sketch, "E643", {"start": v(-0.76, 35.79) * mm, "end": v(-0.68, 35.8) * mm});
            skLineSegment(sketch, "E644", {"start": v(-0.68, 35.8) * mm, "end": v(-0.58, 35.82) * mm});
            skLineSegment(sketch, "E645", {"start": v(-0.58, 35.82) * mm, "end": v(-0.3, 35.83) * mm});
            skLineSegment(sketch, "E646", {"start": v(-0.3, 35.83) * mm, "end": v(0.11, 35.8) * mm});
            skLineSegment(sketch, "E647", {"start": v(0.11, 35.8) * mm, "end": v(0.52, 35.71) * mm});
            skLineSegment(sketch, "E648", {"start": v(0.52, 35.71) * mm, "end": v(0.9, 35.56) * mm});
            skLineSegment(sketch, "E649", {"start": v(0.9, 35.56) * mm, "end": v(1.26, 35.35) * mm});
            skLineSegment(sketch, "E650", {"start": v(1.26, 35.35) * mm, "end": v(1.57, 35.06) * mm});
            skLineSegment(sketch, "E651", {"start": v(1.57, 35.06) * mm, "end": v(1.81, 34.72) * mm});
            skLineSegment(sketch, "E652", {"start": v(1.81, 34.72) * mm, "end": v(1.94, 34.4) * mm});
            skLineSegment(sketch, "E653", {"start": v(1.94, 34.4) * mm, "end": v(1.97, 34.3) * mm});
            skLineSegment(sketch, "E654", {"start": v(22.53, 29.26) * mm, "end": v(22.58, 29.1) * mm});
            skLineSegment(sketch, "E655", {"start": v(22.58, 29.1) * mm, "end": v(22.7, 28.59) * mm});
            skLineSegment(sketch, "E656", {"start": v(22.7, 28.59) * mm, "end": v(22.78, 27.93) * mm});
            skLineSegment(sketch, "E657", {"start": v(22.78, 27.93) * mm, "end": v(22.76, 27.3) * mm});
            skLineSegment(sketch, "E658", {"start": v(22.76, 27.3) * mm, "end": v(22.65, 26.67) * mm});
            skLineSegment(sketch, "E659", {"start": v(22.65, 26.67) * mm, "end": v(22.48, 26.06) * mm});
            skLineSegment(sketch, "E660", {"start": v(22.48, 26.06) * mm, "end": v(22.24, 25.47) * mm});
            skLineSegment(sketch, "E661", {"start": v(22.24, 25.47) * mm, "end": v(21.96, 24.89) * mm});
            skLineSegment(sketch, "E662", {"start": v(21.96, 24.89) * mm, "end": v(21.73, 24.47) * mm});
            skLineSegment(sketch, "E663", {"start": v(21.73, 24.47) * mm, "end": v(21.64, 24.33) * mm});
            skLineSegment(sketch, "E664", {"start": v(21.64, 24.33) * mm, "end": v(21.57, 24.2) * mm});
            skLineSegment(sketch, "E665", {"start": v(21.57, 24.2) * mm, "end": v(21.31, 23.83) * mm});
            skLineSegment(sketch, "E666", {"start": v(21.31, 23.83) * mm, "end": v(20.88, 23.37) * mm});
            skLineSegment(sketch, "E667", {"start": v(20.88, 23.37) * mm, "end": v(20.38, 22.96) * mm});
            skLineSegment(sketch, "E668", {"start": v(20.38, 22.96) * mm, "end": v(19.83, 22.6) * mm});
            skLineSegment(sketch, "E669", {"start": v(19.83, 22.6) * mm, "end": v(19.27, 22.33) * mm});
            skLineSegment(sketch, "E670", {"start": v(19.27, 22.33) * mm, "end": v(18.72, 22.14) * mm});
            skLineSegment(sketch, "E671", {"start": v(18.72, 22.14) * mm, "end": v(18.2, 22.04) * mm});
            skLineSegment(sketch, "E672", {"start": v(18.2, 22.04) * mm, "end": v(17.86, 22.03) * mm});
            skLineSegment(sketch, "E673", {"start": v(17.86, 22.03) * mm, "end": v(17.75, 22.05) * mm});
            skLineSegment(sketch, "E674", {"start": v(17.75, 22.05) * mm, "end": v(17.52, 22.09) * mm});
            skLineSegment(sketch, "E675", {"start": v(17.52, 22.09) * mm, "end": v(16.85, 22.26) * mm});
            skLineSegment(sketch, "E676", {"start": v(16.85, 22.26) * mm, "end": v(15.98, 22.56) * mm});
            skLineSegment(sketch, "E677", {"start": v(15.98, 22.56) * mm, "end": v(15.13, 22.94) * mm});
            skLineSegment(sketch, "E678", {"start": v(15.13, 22.94) * mm, "end": v(14.3, 23.37) * mm});
            skLineSegment(sketch, "E679", {"start": v(14.3, 23.37) * mm, "end": v(13.45, 23.86) * mm});
            skLineSegment(sketch, "E680", {"start": v(13.45, 23.86) * mm, "end": v(12.6, 24.38) * mm});
            skLineSegment(sketch, "E681", {"start": v(12.6, 24.38) * mm, "end": v(11.75, 24.92) * mm});
            skLineSegment(sketch, "E682", {"start": v(11.75, 24.92) * mm, "end": v(11.09, 25.33) * mm});
            skLineSegment(sketch, "E683", {"start": v(11.09, 25.33) * mm, "end": v(10.87, 25.47) * mm});
            skLineSegment(sketch, "E684", {"start": v(10.87, 25.47) * mm, "end": v(15.61, 34.04) * mm});
            skLineSegment(sketch, "E685", {"start": v(15.61, 34.04) * mm, "end": v(15.84, 33.91) * mm});
            skLineSegment(sketch, "E686", {"start": v(15.84, 33.91) * mm, "end": v(16.54, 33.56) * mm});
            skLineSegment(sketch, "E687", {"start": v(16.54, 33.56) * mm, "end": v(17.5, 33.11) * mm});
            skLineSegment(sketch, "E688", {"start": v(17.5, 33.11) * mm, "end": v(18.47, 32.65) * mm});
            skLineSegment(sketch, "E689", {"start": v(18.47, 32.65) * mm, "end": v(19.41, 32.16) * mm});
            skLineSegment(sketch, "E690", {"start": v(19.41, 32.16) * mm, "end": v(20.32, 31.6) * mm});
            skLineSegment(sketch, "E691", {"start": v(20.32, 31.6) * mm, "end": v(21.15, 30.95) * mm});
            skLineSegment(sketch, "E692", {"start": v(21.15, 30.95) * mm, "end": v(21.9, 30.18) * mm});
            skLineSegment(sketch, "E693", {"start": v(21.9, 30.18) * mm, "end": v(22.4, 29.5) * mm});
            skLineSegment(sketch, "E694", {"start": v(22.4, 29.5) * mm, "end": v(22.53, 29.26) * mm});
            skLineSegment(sketch, "E695", {"start": v(19.7, 28.82) * mm, "end": v(19.7, 28.69) * mm});
            skLineSegment(sketch, "E696", {"start": v(19.7, 28.69) * mm, "end": v(19.72, 28.3) * mm});
            skLineSegment(sketch, "E697", {"start": v(19.72, 28.3) * mm, "end": v(19.67, 27.78) * mm});
            skLineSegment(sketch, "E698", {"start": v(19.67, 27.78) * mm, "end": v(19.56, 27.26) * mm});
            skLineSegment(sketch, "E699", {"start": v(19.56, 27.26) * mm, "end": v(19.38, 26.76) * mm});
            skLineSegment(sketch, "E700", {"start": v(19.38, 26.76) * mm, "end": v(19.14, 26.28) * mm});
            skLineSegment(sketch, "E701", {"start": v(19.14, 26.28) * mm, "end": v(18.83, 25.83) * mm});
            skLineSegment(sketch, "E702", {"start": v(18.83, 25.83) * mm, "end": v(18.47, 25.42) * mm});
            skLineSegment(sketch, "E703", {"start": v(18.47, 25.42) * mm, "end": v(18.15, 25.15) * mm});
            skLineSegment(sketch, "E704", {"start": v(18.15, 25.15) * mm, "end": v(18.04, 25.06) * mm});
            skLineSegment(sketch, "E705", {"start": v(18.04, 25.06) * mm, "end": v(17.99, 25.02) * mm});
            skLineSegment(sketch, "E706", {"start": v(17.99, 25.02) * mm, "end": v(17.8, 24.92) * mm});
            skLineSegment(sketch, "E707", {"start": v(17.8, 24.92) * mm, "end": v(17.55, 24.84) * mm});
            skLineSegment(sketch, "E708", {"start": v(17.55, 24.84) * mm, "end": v(17.27, 24.8) * mm});
            skLineSegment(sketch, "E709", {"start": v(17.27, 24.8) * mm, "end": v(16.98, 24.81) * mm});
            skLineSegment(sketch, "E710", {"start": v(16.98, 24.81) * mm, "end": v(16.68, 24.86) * mm});
            skLineSegment(sketch, "E711", {"start": v(16.68, 24.86) * mm, "end": v(16.38, 24.94) * mm});
            skLineSegment(sketch, "E712", {"start": v(16.38, 24.94) * mm, "end": v(16.08, 25.04) * mm});
            skLineSegment(sketch, "E713", {"start": v(16.08, 25.04) * mm, "end": v(15.8, 25.16) * mm});
            skLineSegment(sketch, "E714", {"start": v(15.8, 25.16) * mm, "end": v(15.52, 25.3) * mm});
            skLineSegment(sketch, "E715", {"start": v(15.52, 25.3) * mm, "end": v(15.27, 25.43) * mm});
            skLineSegment(sketch, "E716", {"start": v(15.27, 25.43) * mm, "end": v(15.03, 25.56) * mm});
            skLineSegment(sketch, "E717", {"start": v(15.03, 25.56) * mm, "end": v(14.83, 25.68) * mm});
            skLineSegment(sketch, "E718", {"start": v(14.83, 25.68) * mm, "end": v(14.67, 25.79) * mm});
            skLineSegment(sketch, "E719", {"start": v(14.67, 25.79) * mm, "end": v(14.54, 25.87) * mm});
            skLineSegment(sketch, "E720", {"start": v(14.54, 25.87) * mm, "end": v(14.46, 25.93) * mm});
            skLineSegment(sketch, "E721", {"start": v(14.46, 25.93) * mm, "end": v(14.44, 25.95) * mm});
            skLineSegment(sketch, "E722", {"start": v(14.44, 25.95) * mm, "end": v(17.12, 30.91) * mm});
            skLineSegment(sketch, "E723", {"start": v(17.12, 30.91) * mm, "end": v(17.22, 30.85) * mm});
            skLineSegment(sketch, "E724", {"start": v(17.22, 30.85) * mm, "end": v(17.52, 30.7) * mm});
            skLineSegment(sketch, "E725", {"start": v(17.52, 30.7) * mm, "end": v(17.93, 30.49) * mm});
            skLineSegment(sketch, "E726", {"start": v(17.93, 30.49) * mm, "end": v(18.33, 30.28) * mm});
            skLineSegment(sketch, "E727", {"start": v(18.33, 30.28) * mm, "end": v(18.7, 30.07) * mm});
            skLineSegment(sketch, "E728", {"start": v(18.7, 30.07) * mm, "end": v(19.03, 29.83) * mm});
            skLineSegment(sketch, "E729", {"start": v(19.03, 29.83) * mm, "end": v(19.32, 29.55) * mm});
            skLineSegment(sketch, "E730", {"start": v(19.32, 29.55) * mm, "end": v(19.54, 29.22) * mm});
            skLineSegment(sketch, "E731", {"start": v(19.54, 29.22) * mm, "end": v(19.67, 28.92) * mm});
            skLineSegment(sketch, "E732", {"start": v(19.67, 28.92) * mm, "end": v(19.7, 28.82) * mm});
            skLineSegment(sketch, "E733", {"start": v(-29, 20.72) * mm, "end": v(-29.08, 20.63) * mm});
            skLineSegment(sketch, "E734", {"start": v(-29.08, 20.63) * mm, "end": v(-29.34, 20.34) * mm});
            skLineSegment(sketch, "E735", {"start": v(-29.34, 20.34) * mm, "end": v(-29.68, 19.97) * mm});
            skLineSegment(sketch, "E736", {"start": v(-29.68, 19.97) * mm, "end": v(-30.01, 19.59) * mm});
            skLineSegment(sketch, "E737", {"start": v(-30.01, 19.59) * mm, "end": v(-30.32, 19.2) * mm});
            skLineSegment(sketch, "E738", {"start": v(-30.32, 19.2) * mm, "end": v(-30.6, 18.8) * mm});
            skLineSegment(sketch, "E739", {"start": v(-30.6, 18.8) * mm, "end": v(-30.83, 18.38) * mm});
            skLineSegment(sketch, "E740", {"start": v(-30.83, 18.38) * mm, "end": v(-31, 17.93) * mm});
            skLineSegment(sketch, "E741", {"start": v(-31, 17.93) * mm, "end": v(-31.08, 17.57) * mm});
            skLineSegment(sketch, "E742", {"start": v(-31.08, 17.57) * mm, "end": v(-31.1, 17.45) * mm});
            skLineSegment(sketch, "E743", {"start": v(-31.1, 17.45) * mm, "end": v(-31.1, 17.4) * mm});
            skLineSegment(sketch, "E744", {"start": v(-31.1, 17.4) * mm, "end": v(-31.08, 17.28) * mm});
            skLineSegment(sketch, "E745", {"start": v(-31.08, 17.28) * mm, "end": v(-31.02, 17.11) * mm});
            skLineSegment(sketch, "E746", {"start": v(-31.02, 17.11) * mm, "end": v(-30.94, 16.95) * mm});
            skLineSegment(sketch, "E747", {"start": v(-30.94, 16.95) * mm, "end": v(-30.83, 16.8) * mm});
            skLineSegment(sketch, "E748", {"start": v(-30.83, 16.8) * mm, "end": v(-30.7, 16.67) * mm});
            skLineSegment(sketch, "E749", {"start": v(-30.7, 16.67) * mm, "end": v(-30.54, 16.58) * mm});
            skLineSegment(sketch, "E750", {"start": v(-30.54, 16.58) * mm, "end": v(-30.36, 16.53) * mm});
            skLineSegment(sketch, "E751", {"start": v(-30.36, 16.53) * mm, "end": v(-30.22, 16.53) * mm});
            skLineSegment(sketch, "E752", {"start": v(-30.22, 16.53) * mm, "end": v(-30.18, 16.53) * mm});
            skLineSegment(sketch, "E753", {"start": v(-30.18, 16.53) * mm, "end": v(-30.03, 16.65) * mm});
            skLineSegment(sketch, "E754", {"start": v(-30.03, 16.65) * mm, "end": v(-29.62, 17.04) * mm});
            skLineSegment(sketch, "E755", {"start": v(-29.62, 17.04) * mm, "end": v(-29.06, 17.62) * mm});
            skLineSegment(sketch, "E756", {"start": v(-29.06, 17.62) * mm, "end": v(-28.48, 18.22) * mm});
            skLineSegment(sketch, "E757", {"start": v(-28.48, 18.22) * mm, "end": v(-27.87, 18.79) * mm});
            skLineSegment(sketch, "E758", {"start": v(-27.87, 18.79) * mm, "end": v(-27.24, 19.27) * mm});
            skLineSegment(sketch, "E759", {"start": v(-27.24, 19.27) * mm, "end": v(-26.57, 19.62) * mm});
            skLineSegment(sketch, "E760", {"start": v(-26.57, 19.62) * mm, "end": v(-25.86, 19.78) * mm});
            skLineSegment(sketch, "E761", {"start": v(-25.86, 19.78) * mm, "end": v(-25.28, 19.75) * mm});
            skLineSegment(sketch, "E762", {"start": v(-25.28, 19.75) * mm, "end": v(-25.1, 19.7) * mm});
            skLineSegment(sketch, "E763", {"start": v(-25.1, 19.7) * mm, "end": v(-25, 19.7) * mm});
            skLineSegment(sketch, "E764", {"start": v(-25, 19.7) * mm, "end": v(-24.7, 19.65) * mm});
            skLineSegment(sketch, "E765", {"start": v(-24.7, 19.65) * mm, "end": v(-24.32, 19.51) * mm});
            skLineSegment(sketch, "E766", {"start": v(-24.32, 19.51) * mm, "end": v(-23.95, 19.31) * mm});
            skLineSegment(sketch, "E767", {"start": v(-23.95, 19.31) * mm, "end": v(-23.62, 19.05) * mm});
            skLineSegment(sketch, "E768", {"start": v(-23.62, 19.05) * mm, "end": v(-23.31, 18.75) * mm});
            skLineSegment(sketch, "E769", {"start": v(-23.31, 18.75) * mm, "end": v(-23.06, 18.42) * mm});
            skLineSegment(sketch, "E770", {"start": v(-23.06, 18.42) * mm, "end": v(-22.85, 18.08) * mm});
            skLineSegment(sketch, "E771", {"start": v(-22.85, 18.08) * mm, "end": v(-22.74, 17.83) * mm});
            skLineSegment(sketch, "E772", {"start": v(-22.74, 17.83) * mm, "end": v(-22.71, 17.75) * mm});
            skLineSegment(sketch, "E773", {"start": v(-22.71, 17.75) * mm, "end": v(-22.65, 17.5) * mm});
            skLineSegment(sketch, "E774", {"start": v(-22.65, 17.5) * mm, "end": v(-22.6, 16.76) * mm});
            skLineSegment(sketch, "E775", {"start": v(-22.6, 16.76) * mm, "end": v(-22.68, 15.8) * mm});
            skLineSegment(sketch, "E776", {"start": v(-22.68, 15.8) * mm, "end": v(-22.95, 14.9) * mm});
            skLineSegment(sketch, "E777", {"start": v(-22.95, 14.9) * mm, "end": v(-23.36, 14.04) * mm});
            skLineSegment(sketch, "E778", {"start": v(-23.36, 14.04) * mm, "end": v(-23.9, 13.21) * mm});
            skLineSegment(sketch, "E779", {"start": v(-23.9, 13.21) * mm, "end": v(-24.5, 12.43) * mm});
            skLineSegment(sketch, "E780", {"start": v(-24.5, 12.43) * mm, "end": v(-25.16, 11.7) * mm});
            skLineSegment(sketch, "E781", {"start": v(-25.16, 11.7) * mm, "end": v(-25.66, 11.18) * mm});
            skLineSegment(sketch, "E782", {"start": v(-25.66, 11.18) * mm, "end": v(-25.84, 11.02) * mm});
            skLineSegment(sketch, "E783", {"start": v(-25.84, 11.02) * mm, "end": v(-27.5, 12.05) * mm});
            skLineSegment(sketch, "E784", {"start": v(-27.5, 12.05) * mm, "end": v(-27.37, 12.15) * mm});
            skLineSegment(sketch, "E785", {"start": v(-27.37, 12.15) * mm, "end": v(-27.02, 12.47) * mm});
            skLineSegment(sketch, "E786", {"start": v(-27.02, 12.47) * mm, "end": v(-26.53, 12.94) * mm});
            skLineSegment(sketch, "E787", {"start": v(-26.53, 12.94) * mm, "end": v(-26.05, 13.45) * mm});
            skLineSegment(sketch, "E788", {"start": v(-26.05, 13.45) * mm, "end": v(-25.64, 14) * mm});
            skLineSegment(sketch, "E789", {"start": v(-25.64, 14) * mm, "end": v(-25.31, 14.57) * mm});
            skLineSegment(sketch, "E790", {"start": v(-25.31, 14.57) * mm, "end": v(-25.12, 15.16) * mm});
            skLineSegment(sketch, "E791", {"start": v(-25.12, 15.16) * mm, "end": v(-25.08, 15.77) * mm});
            skLineSegment(sketch, "E792", {"start": v(-25.08, 15.77) * mm, "end": v(-25.18, 16.24) * mm});
            skLineSegment(sketch, "E793", {"start": v(-25.18, 16.24) * mm, "end": v(-25.25, 16.38) * mm});
            skLineSegment(sketch, "E794", {"start": v(-25.25, 16.38) * mm, "end": v(-25.35, 16.43) * mm});
            skLineSegment(sketch, "E795", {"start": v(-25.35, 16.43) * mm, "end": v(-25.66, 16.54) * mm});
            skLineSegment(sketch, "E796", {"start": v(-25.66, 16.54) * mm, "end": v(-26.03, 16.58) * mm});
            skLineSegment(sketch, "E797", {"start": v(-26.03, 16.58) * mm, "end": v(-26.37, 16.52) * mm});
            skLineSegment(sketch, "E798", {"start": v(-26.37, 16.52) * mm, "end": v(-26.68, 16.38) * mm});
            skLineSegment(sketch, "E799", {"start": v(-26.68, 16.38) * mm, "end": v(-26.97, 16.16) * mm});
            skLineSegment(sketch, "E800", {"start": v(-26.97, 16.16) * mm, "end": v(-27.24, 15.9) * mm});
            skLineSegment(sketch, "E801", {"start": v(-27.24, 15.9) * mm, "end": v(-27.5, 15.59) * mm});
            skLineSegment(sketch, "E802", {"start": v(-27.5, 15.59) * mm, "end": v(-27.76, 15.25) * mm});
            skLineSegment(sketch, "E803", {"start": v(-27.76, 15.25) * mm, "end": v(-28.01, 14.9) * mm});
            skLineSegment(sketch, "E804", {"start": v(-28.01, 14.9) * mm, "end": v(-28.28, 14.55) * mm});
            skLineSegment(sketch, "E805", {"start": v(-28.28, 14.55) * mm, "end": v(-28.55, 14.21) * mm});
            skLineSegment(sketch, "E806", {"start": v(-28.55, 14.21) * mm, "end": v(-28.85, 13.9) * mm});
            skLineSegment(sketch, "E807", {"start": v(-28.85, 13.9) * mm, "end": v(-29.17, 13.64) * mm});
            skLineSegment(sketch, "E808", {"start": v(-29.17, 13.64) * mm, "end": v(-29.51, 13.44) * mm});
            skLineSegment(sketch, "E809", {"start": v(-29.51, 13.44) * mm, "end": v(-29.9, 13.3) * mm});
            skLineSegment(sketch, "E810", {"start": v(-29.9, 13.3) * mm, "end": v(-30.22, 13.26) * mm});
            skLineSegment(sketch, "E811", {"start": v(-30.22, 13.26) * mm, "end": v(-30.32, 13.26) * mm});
            skLineSegment(sketch, "E812", {"start": v(-30.32, 13.26) * mm, "end": v(-30.43, 13.26) * mm});
            skLineSegment(sketch, "E813", {"start": v(-30.43, 13.26) * mm, "end": v(-30.74, 13.3) * mm});
            skLineSegment(sketch, "E814", {"start": v(-30.74, 13.3) * mm, "end": v(-31.17, 13.4) * mm});
            skLineSegment(sketch, "E815", {"start": v(-31.17, 13.4) * mm, "end": v(-31.6, 13.56) * mm});
            skLineSegment(sketch, "E816", {"start": v(-31.6, 13.56) * mm, "end": v(-32.02, 13.78) * mm});
            skLineSegment(sketch, "E817", {"start": v(-32.02, 13.78) * mm, "end": v(-32.4, 14.06) * mm});
            skLineSegment(sketch, "E818", {"start": v(-32.4, 14.06) * mm, "end": v(-32.74, 14.4) * mm});
            skLineSegment(sketch, "E819", {"start": v(-32.74, 14.4) * mm, "end": v(-33, 14.78) * mm});
            skLineSegment(sketch, "E820", {"start": v(-33, 14.78) * mm, "end": v(-33.16, 15.1) * mm});
            skLineSegment(sketch, "E821", {"start": v(-33.16, 15.1) * mm, "end": v(-33.2, 15.2) * mm});
            skLineSegment(sketch, "E822", {"start": v(-33.2, 15.2) * mm, "end": v(-33.21, 15.33) * mm});
            skLineSegment(sketch, "E823", {"start": v(-33.21, 15.33) * mm, "end": v(-33.27, 15.64) * mm});
            skLineSegment(sketch, "E824", {"start": v(-33.27, 15.64) * mm, "end": v(-33.32, 16.03) * mm});
            skLineSegment(sketch, "E825", {"start": v(-33.32, 16.03) * mm, "end": v(-33.34, 16.32) * mm});
            skLineSegment(sketch, "E826", {"start": v(-33.34, 16.32) * mm, "end": v(-33.34, 16.42) * mm});
            skLineSegment(sketch, "E827", {"start": v(-33.34, 16.42) * mm, "end": v(-33.35, 16.58) * mm});
            skLineSegment(sketch, "E828", {"start": v(-33.35, 16.58) * mm, "end": v(-33.3, 17.07) * mm});
            skLineSegment(sketch, "E829", {"start": v(-33.3, 17.07) * mm, "end": v(-33.14, 17.72) * mm});
            skLineSegment(sketch, "E830", {"start": v(-33.14, 17.72) * mm, "end": v(-32.9, 18.36) * mm});
            skLineSegment(sketch, "E831", {"start": v(-32.9, 18.36) * mm, "end": v(-32.68, 18.81) * mm});
            skLineSegment(sketch, "E832", {"start": v(-32.68, 18.81) * mm, "end": v(-32.6, 18.96) * mm});
            skLineSegment(sketch, "E833", {"start": v(-32.6, 18.96) * mm, "end": v(-32.56, 19.03) * mm});
            skLineSegment(sketch, "E834", {"start": v(-32.56, 19.03) * mm, "end": v(-32.44, 19.23) * mm});
            skLineSegment(sketch, "E835", {"start": v(-32.44, 19.23) * mm, "end": v(-32.27, 19.48) * mm});
            skLineSegment(sketch, "E836", {"start": v(-32.27, 19.48) * mm, "end": v(-32.12, 19.7) * mm});
            skLineSegment(sketch, "E837", {"start": v(-32.12, 19.7) * mm, "end": v(-31.98, 19.9) * mm});
            skLineSegment(sketch, "E838", {"start": v(-31.98, 19.9) * mm, "end": v(-31.86, 20.06) * mm});
            skLineSegment(sketch, "E839", {"start": v(-31.86, 20.06) * mm, "end": v(-31.77, 20.18) * mm});
            skLineSegment(sketch, "E840", {"start": v(-31.77, 20.18) * mm, "end": v(-31.7, 20.26) * mm});
            skLineSegment(sketch, "E841", {"start": v(-31.7, 20.26) * mm, "end": v(-31.68, 20.28) * mm});
            skLineSegment(sketch, "E842", {"start": v(-31.68, 20.28) * mm, "end": v(-30.32, 21.8) * mm});
            skLineSegment(sketch, "E843", {"start": v(-30.32, 21.8) * mm, "end": v(-29, 20.72) * mm});
            skLineSegment(sketch, "E844", {"start": v(-33.34, 18.19) * mm, "end": v(-33.41, 18.18) * mm});
            skLineSegment(sketch, "E845", {"start": v(-33.41, 18.18) * mm, "end": v(-33.63, 18.15) * mm});
            skLineSegment(sketch, "E846", {"start": v(-33.63, 18.15) * mm, "end": v(-33.97, 18.11) * mm});
            skLineSegment(sketch, "E847", {"start": v(-33.97, 18.11) * mm, "end": v(-34.32, 18.07) * mm});
            skLineSegment(sketch, "E848", {"start": v(-34.32, 18.07) * mm, "end": v(-34.55, 18.05) * mm});
            skLineSegment(sketch, "E849", {"start": v(-34.55, 18.05) * mm, "end": v(-34.63, 18.04) * mm});
            skLineSegment(sketch, "E850", {"start": v(-34.63, 18.04) * mm, "end": v(-34.62, 18.07) * mm});
            skLineSegment(sketch, "E851", {"start": v(-34.62, 18.07) * mm, "end": v(-34.59, 18.16) * mm});
            skLineSegment(sketch, "E852", {"start": v(-34.59, 18.16) * mm, "end": v(-34.53, 18.31) * mm});
            skLineSegment(sketch, "E853", {"start": v(-34.53, 18.31) * mm, "end": v(-34.47, 18.5) * mm});
            skLineSegment(sketch, "E854", {"start": v(-34.47, 18.5) * mm, "end": v(-34.4, 18.67) * mm});
            skLineSegment(sketch, "E855", {"start": v(-34.4, 18.67) * mm, "end": v(-34.33, 18.84) * mm});
            skLineSegment(sketch, "E856", {"start": v(-34.33, 18.84) * mm, "end": v(-34.27, 18.98) * mm});
            skLineSegment(sketch, "E857", {"start": v(-34.27, 18.98) * mm, "end": v(-34.24, 19.07) * mm});
            skLineSegment(sketch, "E858", {"start": v(-34.24, 19.07) * mm, "end": v(-34.22, 19.1) * mm});
            skLineSegment(sketch, "E859", {"start": v(-34.22, 19.1) * mm, "end": v(-33.04, 19.29) * mm});
            skLineSegment(sketch, "E860", {"start": v(-33.04, 19.29) * mm, "end": v(-33.6, 20.25) * mm});
            skLineSegment(sketch, "E861", {"start": v(-33.6, 20.25) * mm, "end": v(-33.53, 20.34) * mm});
            skLineSegment(sketch, "E862", {"start": v(-33.53, 20.34) * mm, "end": v(-33.25, 20.82) * mm});
            skLineSegment(sketch, "E863", {"start": v(-33.25, 20.82) * mm, "end": v(-32.96, 21.3) * mm});
            skLineSegment(sketch, "E864", {"start": v(-32.96, 21.3) * mm, "end": v(-32.9, 21.39) * mm});
            skLineSegment(sketch, "E865", {"start": v(-32.9, 21.39) * mm, "end": v(-32.24, 20.17) * mm});
            skLineSegment(sketch, "E866", {"start": v(-32.24, 20.17) * mm, "end": v(-33.34, 18.19) * mm});
            skLineSegment(sketch, "E867", {"start": v(33.9, 16.27) * mm, "end": v(26.54, 8.07) * mm});
            skLineSegment(sketch, "E868", {"start": v(26.54, 8.07) * mm, "end": v(25.14, 11.05) * mm});
            skLineSegment(sketch, "E869", {"start": v(25.14, 11.05) * mm, "end": v(26.9, 12.74) * mm});
            skLineSegment(sketch, "E870", {"start": v(26.9, 12.74) * mm, "end": v(24.92, 16.16) * mm});
            skLineSegment(sketch, "E871", {"start": v(24.92, 16.16) * mm, "end": v(22.67, 15.65) * mm});
            skLineSegment(sketch, "E872", {"start": v(22.67, 15.65) * mm, "end": v(20.98, 18.04) * mm});
            skLineSegment(sketch, "E873", {"start": v(20.98, 18.04) * mm, "end": v(31.76, 19.84) * mm});
            skLineSegment(sketch, "E874", {"start": v(31.76, 19.84) * mm, "end": v(33.9, 16.27) * mm});
            skLineSegment(sketch, "E875", {"start": v(28.08, 14.25) * mm, "end": v(26.76, 16.64) * mm});
            skLineSegment(sketch, "E876", {"start": v(26.76, 16.64) * mm, "end": v(31.28, 17.52) * mm});
            skLineSegment(sketch, "E877", {"start": v(31.28, 17.52) * mm, "end": v(28.08, 14.25) * mm});
            skLineSegment(sketch, "E878", {"start": v(-15.24, -32.9) * mm, "end": v(-17.49, -31.46) * mm});
            skLineSegment(sketch, "E879", {"start": v(-17.49, -31.46) * mm, "end": v(-17, -29.88) * mm});
            skLineSegment(sketch, "E880", {"start": v(-17, -29.88) * mm, "end": v(-19.03, -28.37) * mm});
            skLineSegment(sketch, "E881", {"start": v(-19.03, -28.37) * mm, "end": v(-20.5, -29.37) * mm});
            skLineSegment(sketch, "E882", {"start": v(-20.5, -29.37) * mm, "end": v(-20.65, -29.24) * mm});
            skLineSegment(sketch, "E883", {"start": v(-20.65, -29.24) * mm, "end": v(-22.06, -27.95) * mm});
            skLineSegment(sketch, "E884", {"start": v(-22.06, -27.95) * mm, "end": v(-22.2, -27.82) * mm});
            skLineSegment(sketch, "E885", {"start": v(-22.2, -27.82) * mm, "end": v(-16.35, -23.48) * mm});
            skLineSegment(sketch, "E886", {"start": v(-16.35, -23.48) * mm, "end": v(-13.33, -25.28) * mm});
            skLineSegment(sketch, "E887", {"start": v(-13.33, -25.28) * mm, "end": v(-15.24, -32.9) * mm});
            skLineSegment(sketch, "E888", {"start": v(20.36, -26.8) * mm, "end": v(20.4, -26.9) * mm});
            skLineSegment(sketch, "E889", {"start": v(20.4, -26.9) * mm, "end": v(20.52, -27.26) * mm});
            skLineSegment(sketch, "E890", {"start": v(20.52, -27.26) * mm, "end": v(20.6, -27.73) * mm});
            skLineSegment(sketch, "E891", {"start": v(20.6, -27.73) * mm, "end": v(20.6, -28.2) * mm});
            skLineSegment(sketch, "E892", {"start": v(20.6, -28.2) * mm, "end": v(20.52, -28.64) * mm});
            skLineSegment(sketch, "E893", {"start": v(20.52, -28.64) * mm, "end": v(20.38, -29.06) * mm});
            skLineSegment(sketch, "E894", {"start": v(20.38, -29.06) * mm, "end": v(20.17, -29.45) * mm});
            skLineSegment(sketch, "E895", {"start": v(20.17, -29.45) * mm, "end": v(19.9, -29.8) * mm});
            skLineSegment(sketch, "E896", {"start": v(19.9, -29.8) * mm, "end": v(19.67, -30.03) * mm});
            skLineSegment(sketch, "E897", {"start": v(19.67, -30.03) * mm, "end": v(19.58, -30.1) * mm});
            skLineSegment(sketch, "E898", {"start": v(19.58, -30.1) * mm, "end": v(19.48, -30.21) * mm});
            skLineSegment(sketch, "E899", {"start": v(19.48, -30.21) * mm, "end": v(19.13, -30.53) * mm});
            skLineSegment(sketch, "E900", {"start": v(19.13, -30.53) * mm, "end": v(18.67, -30.92) * mm});
            skLineSegment(sketch, "E901", {"start": v(18.67, -30.92) * mm, "end": v(18.18, -31.24) * mm});
            skLineSegment(sketch, "E902", {"start": v(18.18, -31.24) * mm, "end": v(17.67, -31.51) * mm});
            skLineSegment(sketch, "E903", {"start": v(17.67, -31.51) * mm, "end": v(17.14, -31.72) * mm});
            skLineSegment(sketch, "E904", {"start": v(17.14, -31.72) * mm, "end": v(16.58, -31.86) * mm});
            skLineSegment(sketch, "E905", {"start": v(16.58, -31.86) * mm, "end": v(16, -31.92) * mm});
            skLineSegment(sketch, "E906", {"start": v(16, -31.92) * mm, "end": v(15.54, -31.92) * mm});
            skLineSegment(sketch, "E907", {"start": v(15.54, -31.92) * mm, "end": v(15.4, -31.9) * mm});
            skLineSegment(sketch, "E908", {"start": v(15.4, -31.9) * mm, "end": v(15.26, -31.9) * mm});
            skLineSegment(sketch, "E909", {"start": v(15.26, -31.9) * mm, "end": v(14.85, -31.79) * mm});
            skLineSegment(sketch, "E910", {"start": v(14.85, -31.79) * mm, "end": v(14.34, -31.57) * mm});
            skLineSegment(sketch, "E911", {"start": v(14.34, -31.57) * mm, "end": v(13.87, -31.25) * mm});
            skLineSegment(sketch, "E912", {"start": v(13.87, -31.25) * mm, "end": v(13.44, -30.87) * mm});
            skLineSegment(sketch, "E913", {"start": v(13.44, -30.87) * mm, "end": v(13.06, -30.45) * mm});
            skLineSegment(sketch, "E914", {"start": v(13.06, -30.45) * mm, "end": v(12.73, -30) * mm});
            skLineSegment(sketch, "E915", {"start": v(12.73, -30) * mm, "end": v(12.47, -29.53) * mm});
            skLineSegment(sketch, "E916", {"start": v(12.47, -29.53) * mm, "end": v(12.3, -29.19) * mm});
            skLineSegment(sketch, "E917", {"start": v(12.3, -29.19) * mm, "end": v(12.27, -29.07) * mm});
            skLineSegment(sketch, "E918", {"start": v(12.27, -29.07) * mm, "end": v(12.24, -28.96) * mm});
            skLineSegment(sketch, "E919", {"start": v(12.24, -28.96) * mm, "end": v(12.17, -28.61) * mm});
            skLineSegment(sketch, "E920", {"start": v(12.17, -28.61) * mm, "end": v(12.1, -28.16) * mm});
            skLineSegment(sketch, "E921", {"start": v(12.1, -28.16) * mm, "end": v(12.09, -27.7) * mm});
            skLineSegment(sketch, "E922", {"start": v(12.09, -27.7) * mm, "end": v(12.12, -27.27) * mm});
            skLineSegment(sketch, "E923", {"start": v(12.12, -27.27) * mm, "end": v(12.2, -26.85) * mm});
            skLineSegment(sketch, "E924", {"start": v(12.2, -26.85) * mm, "end": v(12.35, -26.45) * mm});
            skLineSegment(sketch, "E925", {"start": v(12.35, -26.45) * mm, "end": v(12.56, -26.09) * mm});
            skLineSegment(sketch, "E926", {"start": v(12.56, -26.09) * mm, "end": v(12.77, -25.84) * mm});
            skLineSegment(sketch, "E927", {"start": v(12.77, -25.84) * mm, "end": v(12.85, -25.76) * mm});
            skLineSegment(sketch, "E928", {"start": v(12.85, -25.76) * mm, "end": v(12.97, -25.67) * mm});
            skLineSegment(sketch, "E929", {"start": v(12.97, -25.67) * mm, "end": v(13.3, -25.38) * mm});
            skLineSegment(sketch, "E930", {"start": v(13.3, -25.38) * mm, "end": v(13.76, -25.03) * mm});
            skLineSegment(sketch, "E931", {"start": v(13.76, -25.03) * mm, "end": v(14.23, -24.73) * mm});
            skLineSegment(sketch, "E932", {"start": v(14.23, -24.73) * mm, "end": v(14.71, -24.46) * mm});
            skLineSegment(sketch, "E933", {"start": v(14.71, -24.46) * mm, "end": v(15.21, -24.23) * mm});
            skLineSegment(sketch, "E934", {"start": v(15.21, -24.23) * mm, "end": v(15.74, -24.05) * mm});
            skLineSegment(sketch, "E935", {"start": v(15.74, -24.05) * mm, "end": v(16.3, -23.9) * mm});
            skLineSegment(sketch, "E936", {"start": v(16.3, -23.9) * mm, "end": v(16.75, -23.83) * mm});
            skLineSegment(sketch, "E937", {"start": v(16.75, -23.83) * mm, "end": v(16.9, -23.81) * mm});
            skLineSegment(sketch, "E938", {"start": v(16.9, -23.81) * mm, "end": v(17.04, -23.81) * mm});
            skLineSegment(sketch, "E939", {"start": v(17.04, -23.81) * mm, "end": v(17.46, -23.89) * mm});
            skLineSegment(sketch, "E940", {"start": v(17.46, -23.89) * mm, "end": v(18, -24.1) * mm});
            skLineSegment(sketch, "E941", {"start": v(18, -24.1) * mm, "end": v(18.5, -24.4) * mm});
            skLineSegment(sketch, "E942", {"start": v(18.5, -24.4) * mm, "end": v(18.97, -24.8) * mm});
            skLineSegment(sketch, "E943", {"start": v(18.97, -24.8) * mm, "end": v(19.4, -25.27) * mm});
            skLineSegment(sketch, "E944", {"start": v(19.4, -25.27) * mm, "end": v(19.78, -25.77) * mm});
            skLineSegment(sketch, "E945", {"start": v(19.78, -25.77) * mm, "end": v(20.1, -26.28) * mm});
            skLineSegment(sketch, "E946", {"start": v(20.1, -26.28) * mm, "end": v(20.3, -26.66) * mm});
            skLineSegment(sketch, "E947", {"start": v(20.3, -26.66) * mm, "end": v(20.36, -26.8) * mm});
            skLineSegment(sketch, "E948", {"start": v(-16.38, -28.45) * mm, "end": v(-17.78, -27.45) * mm});
            skLineSegment(sketch, "E949", {"start": v(-17.78, -27.45) * mm, "end": v(-15.8, -25.8) * mm});
            skLineSegment(sketch, "E950", {"start": v(-15.8, -25.8) * mm, "end": v(-16.38, -28.45) * mm});
            skLineSegment(sketch, "E951", {"start": v(18.11, -27.9) * mm, "end": v(18.16, -28) * mm});
            skLineSegment(sketch, "E952", {"start": v(18.16, -28) * mm, "end": v(18.25, -28.3) * mm});
            skLineSegment(sketch, "E953", {"start": v(18.25, -28.3) * mm, "end": v(18.3, -28.67) * mm});
            skLineSegment(sketch, "E954", {"start": v(18.3, -28.67) * mm, "end": v(18.25, -29.03) * mm});
            skLineSegment(sketch, "E955", {"start": v(18.25, -29.03) * mm, "end": v(18.13, -29.35) * mm});
            skLineSegment(sketch, "E956", {"start": v(18.13, -29.35) * mm, "end": v(17.94, -29.63) * mm});
            skLineSegment(sketch, "E957", {"start": v(17.94, -29.63) * mm, "end": v(17.67, -29.86) * mm});
            skLineSegment(sketch, "E958", {"start": v(17.67, -29.86) * mm, "end": v(17.33, -30.03) * mm});
            skLineSegment(sketch, "E959", {"start": v(17.33, -30.03) * mm, "end": v(17.04, -30.12) * mm});
            skLineSegment(sketch, "E960", {"start": v(17.04, -30.12) * mm, "end": v(16.94, -30.14) * mm});
            skLineSegment(sketch, "E961", {"start": v(16.94, -30.14) * mm, "end": v(16.8, -30.16) * mm});
            skLineSegment(sketch, "E962", {"start": v(16.8, -30.16) * mm, "end": v(16.4, -30.16) * mm});
            skLineSegment(sketch, "E963", {"start": v(16.4, -30.16) * mm, "end": v(15.95, -30.03) * mm});
            skLineSegment(sketch, "E964", {"start": v(15.95, -30.03) * mm, "end": v(15.58, -29.78) * mm});
            skLineSegment(sketch, "E965", {"start": v(15.58, -29.78) * mm, "end": v(15.26, -29.44) * mm});
            skLineSegment(sketch, "E966", {"start": v(15.26, -29.44) * mm, "end": v(15, -29.05) * mm});
            skLineSegment(sketch, "E967", {"start": v(15, -29.05) * mm, "end": v(14.76, -28.63) * mm});
            skLineSegment(sketch, "E968", {"start": v(14.76, -28.63) * mm, "end": v(14.56, -28.22) * mm});
            skLineSegment(sketch, "E969", {"start": v(14.56, -28.22) * mm, "end": v(14.41, -27.95) * mm});
            skLineSegment(sketch, "E970", {"start": v(14.41, -27.95) * mm, "end": v(14.36, -27.86) * mm});
            skLineSegment(sketch, "E971", {"start": v(14.36, -27.86) * mm, "end": v(14.32, -27.78) * mm});
            skLineSegment(sketch, "E972", {"start": v(14.32, -27.78) * mm, "end": v(14.24, -27.51) * mm});
            skLineSegment(sketch, "E973", {"start": v(14.24, -27.51) * mm, "end": v(14.21, -27.16) * mm});
            skLineSegment(sketch, "E974", {"start": v(14.21, -27.16) * mm, "end": v(14.27, -26.8) * mm});
            skLineSegment(sketch, "E975", {"start": v(14.27, -26.8) * mm, "end": v(14.4, -26.46) * mm});
            skLineSegment(sketch, "E976", {"start": v(14.4, -26.46) * mm, "end": v(14.6, -26.16) * mm});
            skLineSegment(sketch, "E977", {"start": v(14.6, -26.16) * mm, "end": v(14.86, -25.9) * mm});
            skLineSegment(sketch, "E978", {"start": v(14.86, -25.9) * mm, "end": v(15.17, -25.72) * mm});
            skLineSegment(sketch, "E979", {"start": v(15.17, -25.72) * mm, "end": v(15.45, -25.63) * mm});
            skLineSegment(sketch, "E980", {"start": v(15.45, -25.63) * mm, "end": v(15.54, -25.62) * mm});
            skLineSegment(sketch, "E981", {"start": v(15.54, -25.62) * mm, "end": v(15.67, -25.6) * mm});
            skLineSegment(sketch, "E982", {"start": v(15.67, -25.6) * mm, "end": v(16.06, -25.6) * mm});
            skLineSegment(sketch, "E983", {"start": v(16.06, -25.6) * mm, "end": v(16.5, -25.72) * mm});
            skLineSegment(sketch, "E984", {"start": v(16.5, -25.72) * mm, "end": v(16.86, -25.97) * mm});
            skLineSegment(sketch, "E985", {"start": v(16.86, -25.97) * mm, "end": v(17.17, -26.31) * mm});
            skLineSegment(sketch, "E986", {"start": v(17.17, -26.31) * mm, "end": v(17.44, -26.7) * mm});
            skLineSegment(sketch, "E987", {"start": v(17.44, -26.7) * mm, "end": v(17.67, -27.13) * mm});
            skLineSegment(sketch, "E988", {"start": v(17.67, -27.13) * mm, "end": v(17.9, -27.53) * mm});
            skLineSegment(sketch, "E989", {"start": v(17.9, -27.53) * mm, "end": v(18.05, -27.8) * mm});
            skLineSegment(sketch, "E990", {"start": v(18.05, -27.8) * mm, "end": v(18.11, -27.9) * mm});
            skLineSegment(sketch, "E991", {"start": v(-7.37, -32.93) * mm, "end": v(-7.38, -33) * mm});
            skLineSegment(sketch, "E992", {"start": v(-7.38, -33) * mm, "end": v(-7.32, -33.2) * mm});
            skLineSegment(sketch, "E993", {"start": v(-7.32, -33.2) * mm, "end": v(-7.16, -33.45) * mm});
            skLineSegment(sketch, "E994", {"start": v(-7.16, -33.45) * mm, "end": v(-6.92, -33.64) * mm});
            skLineSegment(sketch, "E995", {"start": v(-6.92, -33.64) * mm, "end": v(-6.62, -33.77) * mm});
            skLineSegment(sketch, "E996", {"start": v(-6.62, -33.77) * mm, "end": v(-6.3, -33.82) * mm});
            skLineSegment(sketch, "E997", {"start": v(-6.3, -33.82) * mm, "end": v(-5.98, -33.79) * mm});
            skLineSegment(sketch, "E998", {"start": v(-5.98, -33.79) * mm, "end": v(-5.7, -33.66) * mm});
            skLineSegment(sketch, "E999", {"start": v(-5.7, -33.66) * mm, "end": v(-5.5, -33.48) * mm});
            skLineSegment(sketch, "E1000", {"start": v(-5.5, -33.48) * mm, "end": v(-5.46, -33.41) * mm});
            skLineSegment(sketch, "E1001", {"start": v(-5.46, -33.41) * mm, "end": v(-5.44, -33.34) * mm});
            skLineSegment(sketch, "E1002", {"start": v(-5.44, -33.34) * mm, "end": v(-5.38, -33.1) * mm});
            skLineSegment(sketch, "E1003", {"start": v(-5.38, -33.1) * mm, "end": v(-5.28, -32.64) * mm});
            skLineSegment(sketch, "E1004", {"start": v(-5.28, -32.64) * mm, "end": v(-5.16, -32.05) * mm});
            skLineSegment(sketch, "E1005", {"start": v(-5.16, -32.05) * mm, "end": v(-5.02, -31.36) * mm});
            skLineSegment(sketch, "E1006", {"start": v(-5.02, -31.36) * mm, "end": v(-4.89, -30.62) * mm});
            skLineSegment(sketch, "E1007", {"start": v(-4.89, -30.62) * mm, "end": v(-4.75, -29.87) * mm});
            skLineSegment(sketch, "E1008", {"start": v(-4.75, -29.87) * mm, "end": v(-4.62, -29.15) * mm});
            skLineSegment(sketch, "E1009", {"start": v(-4.62, -29.15) * mm, "end": v(-4.53, -28.65) * mm});
            skLineSegment(sketch, "E1010", {"start": v(-4.53, -28.65) * mm, "end": v(-4.5, -28.48) * mm});
            skLineSegment(sketch, "E1011", {"start": v(-4.5, -28.48) * mm, "end": v(-4.36, -28.52) * mm});
            skLineSegment(sketch, "E1012", {"start": v(-4.36, -28.52) * mm, "end": v(-3.91, -28.62) * mm});
            skLineSegment(sketch, "E1013", {"start": v(-3.91, -28.62) * mm, "end": v(-3.31, -28.76) * mm});
            skLineSegment(sketch, "E1014", {"start": v(-3.31, -28.76) * mm, "end": v(-2.75, -28.88) * mm});
            skLineSegment(sketch, "E1015", {"start": v(-2.75, -28.88) * mm, "end": v(-2.38, -28.97) * mm});
            skLineSegment(sketch, "E1016", {"start": v(-2.38, -28.97) * mm, "end": v(-2.26, -29) * mm});
            skLineSegment(sketch, "E1017", {"start": v(-2.26, -29) * mm, "end": v(-2.28, -29.14) * mm});
            skLineSegment(sketch, "E1018", {"start": v(-2.28, -29.14) * mm, "end": v(-2.33, -29.56) * mm});
            skLineSegment(sketch, "E1019", {"start": v(-2.33, -29.56) * mm, "end": v(-2.42, -30.29) * mm});
            skLineSegment(sketch, "E1020", {"start": v(-2.42, -30.29) * mm, "end": v(-2.54, -31.12) * mm});
            skLineSegment(sketch, "E1021", {"start": v(-2.54, -31.12) * mm, "end": v(-2.7, -32) * mm});
            skLineSegment(sketch, "E1022", {"start": v(-2.7, -32) * mm, "end": v(-2.93, -32.9) * mm});
            skLineSegment(sketch, "E1023", {"start": v(-2.93, -32.9) * mm, "end": v(-3.23, -33.74) * mm});
            skLineSegment(sketch, "E1024", {"start": v(-3.23, -33.74) * mm, "end": v(-3.63, -34.48) * mm});
            skLineSegment(sketch, "E1025", {"start": v(-3.63, -34.48) * mm, "end": v(-4, -34.94) * mm});
            skLineSegment(sketch, "E1026", {"start": v(-4, -34.94) * mm, "end": v(-4.14, -35.07) * mm});
            skLineSegment(sketch, "E1027", {"start": v(-4.14, -35.07) * mm, "end": v(-4.23, -35.14) * mm});
            skLineSegment(sketch, "E1028", {"start": v(-4.23, -35.14) * mm, "end": v(-4.55, -35.3) * mm});
            skLineSegment(sketch, "E1029", {"start": v(-4.55, -35.3) * mm, "end": v(-5, -35.44) * mm});
            skLineSegment(sketch, "E1030", {"start": v(-5, -35.44) * mm, "end": v(-5.5, -35.5) * mm});
            skLineSegment(sketch, "E1031", {"start": v(-5.5, -35.5) * mm, "end": v(-6, -35.48) * mm});
            skLineSegment(sketch, "E1032", {"start": v(-6, -35.48) * mm, "end": v(-6.5, -35.42) * mm});
            skLineSegment(sketch, "E1033", {"start": v(-6.5, -35.42) * mm, "end": v(-7, -35.32) * mm});
            skLineSegment(sketch, "E1034", {"start": v(-7, -35.32) * mm, "end": v(-7.46, -35.2) * mm});
            skLineSegment(sketch, "E1035", {"start": v(-7.46, -35.2) * mm, "end": v(-7.78, -35.1) * mm});
            skLineSegment(sketch, "E1036", {"start": v(-7.78, -35.1) * mm, "end": v(-7.89, -35.07) * mm});
            skLineSegment(sketch, "E1037", {"start": v(-7.89, -35.07) * mm, "end": v(-8, -35.03) * mm});
            skLineSegment(sketch, "E1038", {"start": v(-8, -35.03) * mm, "end": v(-8.3, -34.9) * mm});
            skLineSegment(sketch, "E1039", {"start": v(-8.3, -34.9) * mm, "end": v(-8.66, -34.7) * mm});
            skLineSegment(sketch, "E1040", {"start": v(-8.66, -34.7) * mm, "end": v(-8.96, -34.5) * mm});
            skLineSegment(sketch, "E1041", {"start": v(-8.96, -34.5) * mm, "end": v(-9.2, -34.27) * mm});
            skLineSegment(sketch, "E1042", {"start": v(-9.2, -34.27) * mm, "end": v(-9.4, -34.04) * mm});
            skLineSegment(sketch, "E1043", {"start": v(-9.4, -34.04) * mm, "end": v(-9.57, -33.8) * mm});
            skLineSegment(sketch, "E1044", {"start": v(-9.57, -33.8) * mm, "end": v(-9.69, -33.56) * mm});
            skLineSegment(sketch, "E1045", {"start": v(-9.69, -33.56) * mm, "end": v(-9.78, -33.33) * mm});
            skLineSegment(sketch, "E1046", {"start": v(-9.78, -33.33) * mm, "end": v(-9.84, -33.11) * mm});
            skLineSegment(sketch, "E1047", {"start": v(-9.84, -33.11) * mm, "end": v(-9.88, -32.9) * mm});
            skLineSegment(sketch, "E1048", {"start": v(-9.88, -32.9) * mm, "end": v(-9.9, -32.72) * mm});
            skLineSegment(sketch, "E1049", {"start": v(-9.9, -32.72) * mm, "end": v(-9.9, -32.56) * mm});
            skLineSegment(sketch, "E1050", {"start": v(-9.9, -32.56) * mm, "end": v(-9.9, -32.42) * mm});
            skLineSegment(sketch, "E1051", {"start": v(-9.9, -32.42) * mm, "end": v(-9.89, -32.32) * mm});
            skLineSegment(sketch, "E1052", {"start": v(-9.89, -32.32) * mm, "end": v(-9.88, -32.26) * mm});
            skLineSegment(sketch, "E1053", {"start": v(-9.88, -32.26) * mm, "end": v(-9.87, -32.24) * mm});
            skLineSegment(sketch, "E1054", {"start": v(-9.87, -32.24) * mm, "end": v(-8.77, -27.6) * mm});
            skLineSegment(sketch, "E1055", {"start": v(-8.77, -27.6) * mm, "end": v(-6.5, -28.08) * mm});
            skLineSegment(sketch, "E1056", {"start": v(-6.5, -28.08) * mm, "end": v(-7.37, -32.93) * mm});
            skLineSegment(sketch, "E1057", {"start": v(6.34, -29.77) * mm, "end": v(7.41, -35.1) * mm});
            skLineSegment(sketch, "E1058", {"start": v(7.41, -35.1) * mm, "end": v(5.06, -35.58) * mm});
            skLineSegment(sketch, "E1059", {"start": v(5.06, -35.58) * mm, "end": v(4, -30.21) * mm});
            skLineSegment(sketch, "E1060", {"start": v(4, -30.21) * mm, "end": v(2.15, -30.65) * mm});
            skLineSegment(sketch, "E1061", {"start": v(2.15, -30.65) * mm, "end": v(1.78, -29.04) * mm});
            skLineSegment(sketch, "E1062", {"start": v(1.78, -29.04) * mm, "end": v(7.89, -27.67) * mm});
            skLineSegment(sketch, "E1063", {"start": v(7.89, -27.67) * mm, "end": v(8.33, -29.3) * mm});
            skLineSegment(sketch, "E1064", {"start": v(8.33, -29.3) * mm, "end": v(6.34, -29.77) * mm});
            skLineSegment(sketch, "E1065", {"start": v(4.4, 21.1) * mm, "end": v(4.7, 20.77) * mm});
            skLineSegment(sketch, "E1066", {"start": v(4.7, 20.77) * mm, "end": v(5.56, 19.77) * mm});
            skLineSegment(sketch, "E1067", {"start": v(5.56, 19.77) * mm, "end": v(6.65, 18.4) * mm});
            skLineSegment(sketch, "E1068", {"start": v(6.65, 18.4) * mm, "end": v(7.67, 16.98) * mm});
            skLineSegment(sketch, "E1069", {"start": v(7.67, 16.98) * mm, "end": v(8.6, 15.5) * mm});
            skLineSegment(sketch, "E1070", {"start": v(8.6, 15.5) * mm, "end": v(9.45, 14) * mm});
            skLineSegment(sketch, "E1071", {"start": v(9.45, 14) * mm, "end": v(10.2, 12.43) * mm});
            skLineSegment(sketch, "E1072", {"start": v(10.2, 12.43) * mm, "end": v(10.86, 10.83) * mm});
            skLineSegment(sketch, "E1073", {"start": v(10.86, 10.83) * mm, "end": v(11.42, 9.19) * mm});
            skLineSegment(sketch, "E1074", {"start": v(11.42, 9.19) * mm, "end": v(11.86, 7.52) * mm});
            skLineSegment(sketch, "E1075", {"start": v(11.86, 7.52) * mm, "end": v(12.2, 5.81) * mm});
            skLineSegment(sketch, "E1076", {"start": v(12.2, 5.81) * mm, "end": v(12.41, 4.08) * mm});
            skLineSegment(sketch, "E1077", {"start": v(12.41, 4.08) * mm, "end": v(12.51, 2.31) * mm});
            skLineSegment(sketch, "E1078", {"start": v(12.51, 2.31) * mm, "end": v(12.48, 0.53) * mm});
            skLineSegment(sketch, "E1079", {"start": v(12.48, 0.53) * mm, "end": v(12.31, -1.28) * mm});
            skLineSegment(sketch, "E1080", {"start": v(12.31, -1.28) * mm, "end": v(12.01, -3.1) * mm});
            skLineSegment(sketch, "E1081", {"start": v(12.01, -3.1) * mm, "end": v(11.7, -4.5) * mm});
            skLineSegment(sketch, "E1082", {"start": v(11.7, -4.5) * mm, "end": v(11.57, -4.95) * mm});
            skLineSegment(sketch, "E1083", {"start": v(11.57, -4.95) * mm, "end": v(11.53, -5.05) * mm});
            skLineSegment(sketch, "E1084", {"start": v(11.53, -5.05) * mm, "end": v(11.44, -5.33) * mm});
            skLineSegment(sketch, "E1085", {"start": v(11.44, -5.33) * mm, "end": v(11.3, -5.74) * mm});
            skLineSegment(sketch, "E1086", {"start": v(11.3, -5.74) * mm, "end": v(11.13, -6.24) * mm});
            skLineSegment(sketch, "E1087", {"start": v(11.13, -6.24) * mm, "end": v(10.96, -6.79) * mm});
            skLineSegment(sketch, "E1088", {"start": v(10.96, -6.79) * mm, "end": v(10.8, -7.34) * mm});
            skLineSegment(sketch, "E1089", {"start": v(10.8, -7.34) * mm, "end": v(10.64, -7.84) * mm});
            skLineSegment(sketch, "E1090", {"start": v(10.64, -7.84) * mm, "end": v(10.56, -8.15) * mm});
            skLineSegment(sketch, "E1091", {"start": v(10.56, -8.15) * mm, "end": v(10.54, -8.26) * mm});
            skLineSegment(sketch, "E1092", {"start": v(10.54, -8.26) * mm, "end": v(10.5, -8.42) * mm});
            skLineSegment(sketch, "E1093", {"start": v(10.5, -8.42) * mm, "end": v(10.44, -8.92) * mm});
            skLineSegment(sketch, "E1094", {"start": v(10.44, -8.92) * mm, "end": v(10.4, -9.46) * mm});
            skLineSegment(sketch, "E1095", {"start": v(10.4, -9.46) * mm, "end": v(10.39, -9.82) * mm});
            skLineSegment(sketch, "E1096", {"start": v(10.39, -9.82) * mm, "end": v(10.39, -9.95) * mm});
            skLineSegment(sketch, "E1097", {"start": v(10.39, -9.95) * mm, "end": v(10.42, -10) * mm});
            skLineSegment(sketch, "E1098", {"start": v(10.42, -10) * mm, "end": v(10.53, -10.16) * mm});
            skLineSegment(sketch, "E1099", {"start": v(10.53, -10.16) * mm, "end": v(10.72, -10.34) * mm});
            skLineSegment(sketch, "E1100", {"start": v(10.72, -10.34) * mm, "end": v(10.95, -10.47) * mm});
            skLineSegment(sketch, "E1101", {"start": v(10.95, -10.47) * mm, "end": v(11.2, -10.57) * mm});
            skLineSegment(sketch, "E1102", {"start": v(11.2, -10.57) * mm, "end": v(11.47, -10.63) * mm});
            skLineSegment(sketch, "E1103", {"start": v(11.47, -10.63) * mm, "end": v(11.75, -10.66) * mm});
            skLineSegment(sketch, "E1104", {"start": v(11.75, -10.66) * mm, "end": v(12.02, -10.65) * mm});
            skLineSegment(sketch, "E1105", {"start": v(12.02, -10.65) * mm, "end": v(12.2, -10.62) * mm});
            skLineSegment(sketch, "E1106", {"start": v(12.2, -10.62) * mm, "end": v(12.27, -10.61) * mm});
            skLineSegment(sketch, "E1107", {"start": v(12.27, -10.61) * mm, "end": v(12.32, -10.56) * mm});
            skLineSegment(sketch, "E1108", {"start": v(12.32, -10.56) * mm, "end": v(12.43, -10.37) * mm});
            skLineSegment(sketch, "E1109", {"start": v(12.43, -10.37) * mm, "end": v(12.46, -10.11) * mm});
            skLineSegment(sketch, "E1110", {"start": v(12.46, -10.11) * mm, "end": v(12.42, -9.84) * mm});
            skLineSegment(sketch, "E1111", {"start": v(12.42, -9.84) * mm, "end": v(12.34, -9.56) * mm});
            skLineSegment(sketch, "E1112", {"start": v(12.34, -9.56) * mm, "end": v(12.26, -9.28) * mm});
            skLineSegment(sketch, "E1113", {"start": v(12.26, -9.28) * mm, "end": v(12.21, -8.99) * mm});
            skLineSegment(sketch, "E1114", {"start": v(12.21, -8.99) * mm, "end": v(12.25, -8.7) * mm});
            skLineSegment(sketch, "E1115", {"start": v(12.25, -8.7) * mm, "end": v(12.36, -8.47) * mm});
            skLineSegment(sketch, "E1116", {"start": v(12.36, -8.47) * mm, "end": v(12.41, -8.4) * mm});
            skLineSegment(sketch, "E1117", {"start": v(12.41, -8.4) * mm, "end": v(12.7, -8.38) * mm});
            skLineSegment(sketch, "E1118", {"start": v(12.7, -8.38) * mm, "end": v(13.55, -8.4) * mm});
            skLineSegment(sketch, "E1119", {"start": v(13.55, -8.4) * mm, "end": v(14.64, -8.6) * mm});
            skLineSegment(sketch, "E1120", {"start": v(14.64, -8.6) * mm, "end": v(15.68, -8.97) * mm});
            skLineSegment(sketch, "E1121", {"start": v(15.68, -8.97) * mm, "end": v(16.7, -9.48) * mm});
            skLineSegment(sketch, "E1122", {"start": v(16.7, -9.48) * mm, "end": v(17.66, -10.1) * mm});
            skLineSegment(sketch, "E1123", {"start": v(17.66, -10.1) * mm, "end": v(18.6, -10.8) * mm});
            skLineSegment(sketch, "E1124", {"start": v(18.6, -10.8) * mm, "end": v(19.51, -11.54) * mm});
            skLineSegment(sketch, "E1125", {"start": v(19.51, -11.54) * mm, "end": v(20.17, -12.11) * mm});
            skLineSegment(sketch, "E1126", {"start": v(20.17, -12.11) * mm, "end": v(20.4, -12.3) * mm});
            skLineSegment(sketch, "E1127", {"start": v(20.4, -12.3) * mm, "end": v(20.3, -12.42) * mm});
            skLineSegment(sketch, "E1128", {"start": v(20.3, -12.42) * mm, "end": v(20, -12.76) * mm});
            skLineSegment(sketch, "E1129", {"start": v(20, -12.76) * mm, "end": v(19.59, -13.22) * mm});
            skLineSegment(sketch, "E1130", {"start": v(19.59, -13.22) * mm, "end": v(19.15, -13.66) * mm});
            skLineSegment(sketch, "E1131", {"start": v(19.15, -13.66) * mm, "end": v(18.7, -14.08) * mm});
            skLineSegment(sketch, "E1132", {"start": v(18.7, -14.08) * mm, "end": v(18.22, -14.49) * mm});
            skLineSegment(sketch, "E1133", {"start": v(18.22, -14.49) * mm, "end": v(17.73, -14.87) * mm});
            skLineSegment(sketch, "E1134", {"start": v(17.73, -14.87) * mm, "end": v(17.23, -15.22) * mm});
            skLineSegment(sketch, "E1135", {"start": v(17.23, -15.22) * mm, "end": v(16.7, -15.54) * mm});
            skLineSegment(sketch, "E1136", {"start": v(16.7, -15.54) * mm, "end": v(16.17, -15.82) * mm});
            skLineSegment(sketch, "E1137", {"start": v(16.17, -15.82) * mm, "end": v(15.63, -16.06) * mm});
            skLineSegment(sketch, "E1138", {"start": v(15.63, -16.06) * mm, "end": v(15.07, -16.25) * mm});
            skLineSegment(sketch, "E1139", {"start": v(15.07, -16.25) * mm, "end": v(14.5, -16.39) * mm});
            skLineSegment(sketch, "E1140", {"start": v(14.5, -16.39) * mm, "end": v(13.94, -16.47) * mm});
            skLineSegment(sketch, "E1141", {"start": v(13.94, -16.47) * mm, "end": v(13.36, -16.5) * mm});
            skLineSegment(sketch, "E1142", {"start": v(13.36, -16.5) * mm, "end": v(12.78, -16.46) * mm});
            skLineSegment(sketch, "E1143", {"start": v(12.78, -16.46) * mm, "end": v(12.34, -16.38) * mm});
            skLineSegment(sketch, "E1144", {"start": v(12.34, -16.38) * mm, "end": v(12.2, -16.35) * mm});
            skLineSegment(sketch, "E1145", {"start": v(12.2, -16.35) * mm, "end": v(12.16, -16.3) * mm});
            skLineSegment(sketch, "E1146", {"start": v(12.16, -16.3) * mm, "end": v(12.1, -16.1) * mm});
            skLineSegment(sketch, "E1147", {"start": v(12.1, -16.1) * mm, "end": v(12.15, -15.85) * mm});
            skLineSegment(sketch, "E1148", {"start": v(12.15, -15.85) * mm, "end": v(12.26, -15.59) * mm});
            skLineSegment(sketch, "E1149", {"start": v(12.26, -15.59) * mm, "end": v(12.4, -15.32) * mm});
            skLineSegment(sketch, "E1150", {"start": v(12.4, -15.32) * mm, "end": v(12.52, -15.05) * mm});
            skLineSegment(sketch, "E1151", {"start": v(12.52, -15.05) * mm, "end": v(12.56, -14.79) * mm});
            skLineSegment(sketch, "E1152", {"start": v(12.56, -14.79) * mm, "end": v(12.48, -14.53) * mm});
            skLineSegment(sketch, "E1153", {"start": v(12.48, -14.53) * mm, "end": v(12.3, -14.34) * mm});
            skLineSegment(sketch, "E1154", {"start": v(12.3, -14.34) * mm, "end": v(12.23, -14.29) * mm});
            skLineSegment(sketch, "E1155", {"start": v(12.23, -14.29) * mm, "end": v(-10.54, -14.25) * mm});
            skLineSegment(sketch, "E1156", {"start": v(-10.54, -14.25) * mm, "end": v(-10.6, -14.25) * mm});
            skLineSegment(sketch, "E1157", {"start": v(-10.6, -14.25) * mm, "end": v(-10.8, -14.35) * mm});
            skLineSegment(sketch, "E1158", {"start": v(-10.8, -14.35) * mm, "end": v(-11.12, -14.58) * mm});
            skLineSegment(sketch, "E1159", {"start": v(-11.12, -14.58) * mm, "end": v(-11.46, -14.9) * mm});
            skLineSegment(sketch, "E1160", {"start": v(-11.46, -14.9) * mm, "end": v(-11.8, -15.28) * mm});
            skLineSegment(sketch, "E1161", {"start": v(-11.8, -15.28) * mm, "end": v(-12.16, -15.66) * mm});
            skLineSegment(sketch, "E1162", {"start": v(-12.16, -15.66) * mm, "end": v(-12.5, -16.01) * mm});
            skLineSegment(sketch, "E1163", {"start": v(-12.5, -16.01) * mm, "end": v(-12.83, -16.28) * mm});
            skLineSegment(sketch, "E1164", {"start": v(-12.83, -16.28) * mm, "end": v(-13.04, -16.4) * mm});
            skLineSegment(sketch, "E1165", {"start": v(-13.04, -16.4) * mm, "end": v(-13.11, -16.42) * mm});
            skLineSegment(sketch, "E1166", {"start": v(-13.11, -16.42) * mm, "end": v(-13.2, -16.44) * mm});
            skLineSegment(sketch, "E1167", {"start": v(-13.2, -16.44) * mm, "end": v(-13.51, -16.5) * mm});
            skLineSegment(sketch, "E1168", {"start": v(-13.51, -16.5) * mm, "end": v(-13.95, -16.54) * mm});
            skLineSegment(sketch, "E1169", {"start": v(-13.95, -16.54) * mm, "end": v(-14.4, -16.56) * mm});
            skLineSegment(sketch, "E1170", {"start": v(-14.4, -16.56) * mm, "end": v(-14.86, -16.56) * mm});
            skLineSegment(sketch, "E1171", {"start": v(-14.86, -16.56) * mm, "end": v(-15.3, -16.54) * mm});
            skLineSegment(sketch, "E1172", {"start": v(-15.3, -16.54) * mm, "end": v(-15.67, -16.5) * mm});
            skLineSegment(sketch, "E1173", {"start": v(-15.67, -16.5) * mm, "end": v(-15.98, -16.43) * mm});
            skLineSegment(sketch, "E1174", {"start": v(-15.98, -16.43) * mm, "end": v(-16.15, -16.38) * mm});
            skLineSegment(sketch, "E1175", {"start": v(-16.15, -16.38) * mm, "end": v(-16.2, -16.35) * mm});
            skLineSegment(sketch, "E1176", {"start": v(-16.2, -16.35) * mm, "end": v(-16.29, -16.26) * mm});
            skLineSegment(sketch, "E1177", {"start": v(-16.29, -16.26) * mm, "end": v(-16.53, -15.96) * mm});
            skLineSegment(sketch, "E1178", {"start": v(-16.53, -15.96) * mm, "end": v(-16.8, -15.54) * mm});
            skLineSegment(sketch, "E1179", {"start": v(-16.8, -15.54) * mm, "end": v(-17.03, -15.08) * mm});
            skLineSegment(sketch, "E1180", {"start": v(-17.03, -15.08) * mm, "end": v(-17.23, -14.6) * mm});
            skLineSegment(sketch, "E1181", {"start": v(-17.23, -14.6) * mm, "end": v(-17.4, -14.12) * mm});
            skLineSegment(sketch, "E1182", {"start": v(-17.4, -14.12) * mm, "end": v(-17.6, -13.64) * mm});
            skLineSegment(sketch, "E1183", {"start": v(-17.6, -13.64) * mm, "end": v(-17.78, -13.18) * mm});
            skLineSegment(sketch, "E1184", {"start": v(-17.78, -13.18) * mm, "end": v(-17.94, -12.85) * mm});
            skLineSegment(sketch, "E1185", {"start": v(-17.94, -12.85) * mm, "end": v(-18, -12.74) * mm});
            skLineSegment(sketch, "E1186", {"start": v(-18, -12.74) * mm, "end": v(-18.07, -12.6) * mm});
            skLineSegment(sketch, "E1187", {"start": v(-18.07, -12.6) * mm, "end": v(-18.33, -12.23) * mm});
            skLineSegment(sketch, "E1188", {"start": v(-18.33, -12.23) * mm, "end": v(-18.8, -11.72) * mm});
            skLineSegment(sketch, "E1189", {"start": v(-18.8, -11.72) * mm, "end": v(-19.35, -11.22) * mm});
            skLineSegment(sketch, "E1190", {"start": v(-19.35, -11.22) * mm, "end": v(-19.9, -10.73) * mm});
            skLineSegment(sketch, "E1191", {"start": v(-19.9, -10.73) * mm, "end": v(-20.41, -10.25) * mm});
            skLineSegment(sketch, "E1192", {"start": v(-20.41, -10.25) * mm, "end": v(-20.8, -9.8) * mm});
            skLineSegment(sketch, "E1193", {"start": v(-20.8, -9.8) * mm, "end": v(-21.02, -9.36) * mm});
            skLineSegment(sketch, "E1194", {"start": v(-21.02, -9.36) * mm, "end": v(-21.02, -9.04) * mm});
            skLineSegment(sketch, "E1195", {"start": v(-21.02, -9.04) * mm, "end": v(-20.98, -8.96) * mm});
            skLineSegment(sketch, "E1196", {"start": v(-20.98, -8.96) * mm, "end": v(-20.97, -8.93) * mm});
            skLineSegment(sketch, "E1197", {"start": v(-20.97, -8.93) * mm, "end": v(-20.88, -8.88) * mm});
            skLineSegment(sketch, "E1198", {"start": v(-20.88, -8.88) * mm, "end": v(-20.67, -8.8) * mm});
            skLineSegment(sketch, "E1199", {"start": v(-20.67, -8.8) * mm, "end": v(-20.35, -8.72) * mm});
            skLineSegment(sketch, "E1200", {"start": v(-20.35, -8.72) * mm, "end": v(-19.95, -8.64) * mm});
            skLineSegment(sketch, "E1201", {"start": v(-19.95, -8.64) * mm, "end": v(-19.46, -8.56) * mm});
            skLineSegment(sketch, "E1202", {"start": v(-19.46, -8.56) * mm, "end": v(-18.9, -8.49) * mm});
            skLineSegment(sketch, "E1203", {"start": v(-18.9, -8.49) * mm, "end": v(-18.3, -8.43) * mm});
            skLineSegment(sketch, "E1204", {"start": v(-18.3, -8.43) * mm, "end": v(-17.63, -8.39) * mm});
            skLineSegment(sketch, "E1205", {"start": v(-17.63, -8.39) * mm, "end": v(-16.93, -8.36) * mm});
            skLineSegment(sketch, "E1206", {"start": v(-16.93, -8.36) * mm, "end": v(-16.2, -8.36) * mm});
            skLineSegment(sketch, "E1207", {"start": v(-16.2, -8.36) * mm, "end": v(-15.45, -8.38) * mm});
            skLineSegment(sketch, "E1208", {"start": v(-15.45, -8.38) * mm, "end": v(-14.7, -8.44) * mm});
            skLineSegment(sketch, "E1209", {"start": v(-14.7, -8.44) * mm, "end": v(-13.95, -8.53) * mm});
            skLineSegment(sketch, "E1210", {"start": v(-13.95, -8.53) * mm, "end": v(-13.21, -8.65) * mm});
            skLineSegment(sketch, "E1211", {"start": v(-13.21, -8.65) * mm, "end": v(-12.5, -8.82) * mm});
            skLineSegment(sketch, "E1212", {"start": v(-12.5, -8.82) * mm, "end": v(-12, -8.97) * mm});
            skLineSegment(sketch, "E1213", {"start": v(-12, -8.97) * mm, "end": v(-11.82, -9.03) * mm});
            skLineSegment(sketch, "E1214", {"start": v(-11.82, -9.03) * mm, "end": v(-11.7, -9.08) * mm});
            skLineSegment(sketch, "E1215", {"start": v(-11.7, -9.08) * mm, "end": v(-11.33, -9.27) * mm});
            skLineSegment(sketch, "E1216", {"start": v(-11.33, -9.27) * mm, "end": v(-10.82, -9.55) * mm});
            skLineSegment(sketch, "E1217", {"start": v(-10.82, -9.55) * mm, "end": v(-10.32, -9.84) * mm});
            skLineSegment(sketch, "E1218", {"start": v(-10.32, -9.84) * mm, "end": v(-9.81, -10.1) * mm});
            skLineSegment(sketch, "E1219", {"start": v(-9.81, -10.1) * mm, "end": v(-9.3, -10.33) * mm});
            skLineSegment(sketch, "E1220", {"start": v(-9.3, -10.33) * mm, "end": v(-8.78, -10.48) * mm});
            skLineSegment(sketch, "E1221", {"start": v(-8.78, -10.48) * mm, "end": v(-8.26, -10.53) * mm});
            skLineSegment(sketch, "E1222", {"start": v(-8.26, -10.53) * mm, "end": v(-7.87, -10.5) * mm});
            skLineSegment(sketch, "E1223", {"start": v(-7.87, -10.5) * mm, "end": v(-7.74, -10.46) * mm});
            skLineSegment(sketch, "E1224", {"start": v(-7.74, -10.46) * mm, "end": v(-7.73, -10.46) * mm});
            skLineSegment(sketch, "E1225", {"start": v(-7.73, -10.46) * mm, "end": v(-7.68, -10.43) * mm});
            skLineSegment(sketch, "E1226", {"start": v(-7.68, -10.43) * mm, "end": v(-7.61, -10.39) * mm});
            skLineSegment(sketch, "E1227", {"start": v(-7.61, -10.39) * mm, "end": v(-7.55, -10.32) * mm});
            skLineSegment(sketch, "E1228", {"start": v(-7.55, -10.32) * mm, "end": v(-7.5, -10.24) * mm});
            skLineSegment(sketch, "E1229", {"start": v(-7.5, -10.24) * mm, "end": v(-7.48, -10.2) * mm});
            skLineSegment(sketch, "E1230", {"start": v(-7.48, -10.2) * mm, "end": v(-7.47, -10) * mm});
            skLineSegment(sketch, "E1231", {"start": v(-7.47, -10) * mm, "end": v(-7.45, -9.4) * mm});
            skLineSegment(sketch, "E1232", {"start": v(-7.45, -9.4) * mm, "end": v(-7.5, -8.6) * mm});
            skLineSegment(sketch, "E1233", {"start": v(-7.5, -8.6) * mm, "end": v(-7.63, -7.78) * mm});
            skLineSegment(sketch, "E1234", {"start": v(-7.63, -7.78) * mm, "end": v(-7.83, -6.97) * mm});
            skLineSegment(sketch, "E1235", {"start": v(-7.83, -6.97) * mm, "end": v(-8.1, -6.17) * mm});
            skLineSegment(sketch, "E1236", {"start": v(-8.1, -6.17) * mm, "end": v(-8.42, -5.38) * mm});
            skLineSegment(sketch, "E1237", {"start": v(-8.42, -5.38) * mm, "end": v(-8.82, -4.6) * mm});
            skLineSegment(sketch, "E1238", {"start": v(-8.82, -4.6) * mm, "end": v(-9.27, -3.85) * mm});
            skLineSegment(sketch, "E1239", {"start": v(-9.27, -3.85) * mm, "end": v(-9.78, -3.12) * mm});
            skLineSegment(sketch, "E1240", {"start": v(-9.78, -3.12) * mm, "end": v(-10.35, -2.42) * mm});
            skLineSegment(sketch, "E1241", {"start": v(-10.35, -2.42) * mm, "end": v(-10.97, -1.75) * mm});
            skLineSegment(sketch, "E1242", {"start": v(-10.97, -1.75) * mm, "end": v(-11.64, -1.12) * mm});
            skLineSegment(sketch, "E1243", {"start": v(-11.64, -1.12) * mm, "end": v(-12.35, -0.53) * mm});
            skLineSegment(sketch, "E1244", {"start": v(-12.35, -0.53) * mm, "end": v(-13.1, 0.01) * mm});
            skLineSegment(sketch, "E1245", {"start": v(-13.1, 0.01) * mm, "end": v(-13.9, 0.5) * mm});
            skLineSegment(sketch, "E1246", {"start": v(-13.9, 0.5) * mm, "end": v(-14.52, 0.84) * mm});
            skLineSegment(sketch, "E1247", {"start": v(-14.52, 0.84) * mm, "end": v(-14.73, 0.94) * mm});
            skLineSegment(sketch, "E1248", {"start": v(-14.73, 0.94) * mm, "end": v(-14.96, 1.05) * mm});
            skLineSegment(sketch, "E1249", {"start": v(-14.96, 1.05) * mm, "end": v(-15.66, 1.32) * mm});
            skLineSegment(sketch, "E1250", {"start": v(-15.66, 1.32) * mm, "end": v(-16.53, 1.54) * mm});
            skLineSegment(sketch, "E1251", {"start": v(-16.53, 1.54) * mm, "end": v(-17.38, 1.63) * mm});
            skLineSegment(sketch, "E1252", {"start": v(-17.38, 1.63) * mm, "end": v(-18.07, 1.62) * mm});
            skLineSegment(sketch, "E1253", {"start": v(-18.07, 1.62) * mm, "end": v(-18.3, 1.6) * mm});
            skLineSegment(sketch, "E1254", {"start": v(-18.3, 1.6) * mm, "end": v(-18.42, 1.6) * mm});
            skLineSegment(sketch, "E1255", {"start": v(-18.42, 1.6) * mm, "end": v(-18.8, 1.57) * mm});
            skLineSegment(sketch, "E1256", {"start": v(-18.8, 1.57) * mm, "end": v(-19.32, 1.55) * mm});
            skLineSegment(sketch, "E1257", {"start": v(-19.32, 1.55) * mm, "end": v(-19.83, 1.53) * mm});
            skLineSegment(sketch, "E1258", {"start": v(-19.83, 1.53) * mm, "end": v(-20.32, 1.55) * mm});
            skLineSegment(sketch, "E1259", {"start": v(-20.32, 1.55) * mm, "end": v(-20.8, 1.6) * mm});
            skLineSegment(sketch, "E1260", {"start": v(-20.8, 1.6) * mm, "end": v(-21.23, 1.68) * mm});
            skLineSegment(sketch, "E1261", {"start": v(-21.23, 1.68) * mm, "end": v(-21.64, 1.83) * mm});
            skLineSegment(sketch, "E1262", {"start": v(-21.64, 1.83) * mm, "end": v(-21.93, 1.98) * mm});
            skLineSegment(sketch, "E1263", {"start": v(-21.93, 1.98) * mm, "end": v(-22.01, 2.04) * mm});
            skLineSegment(sketch, "E1264", {"start": v(-22.01, 2.04) * mm, "end": v(-22.08, 2.1) * mm});
            skLineSegment(sketch, "E1265", {"start": v(-22.08, 2.1) * mm, "end": v(-22.26, 2.32) * mm});
            skLineSegment(sketch, "E1266", {"start": v(-22.26, 2.32) * mm, "end": v(-22.43, 2.72) * mm});
            skLineSegment(sketch, "E1267", {"start": v(-22.43, 2.72) * mm, "end": v(-22.52, 3.22) * mm});
            skLineSegment(sketch, "E1268", {"start": v(-22.52, 3.22) * mm, "end": v(-22.54, 3.8) * mm});
            skLineSegment(sketch, "E1269", {"start": v(-22.54, 3.8) * mm, "end": v(-22.5, 4.43) * mm});
            skLineSegment(sketch, "E1270", {"start": v(-22.5, 4.43) * mm, "end": v(-22.4, 5.12) * mm});
            skLineSegment(sketch, "E1271", {"start": v(-22.4, 5.12) * mm, "end": v(-22.25, 5.84) * mm});
            skLineSegment(sketch, "E1272", {"start": v(-22.25, 5.84) * mm, "end": v(-22.1, 6.38) * mm});
            skLineSegment(sketch, "E1273", {"start": v(-22.1, 6.38) * mm, "end": v(-22.05, 6.56) * mm});
            skLineSegment(sketch, "E1274", {"start": v(-22.05, 6.56) * mm, "end": v(-22, 6.73) * mm});
            skLineSegment(sketch, "E1275", {"start": v(-22, 6.73) * mm, "end": v(-21.8, 7.24) * mm});
            skLineSegment(sketch, "E1276", {"start": v(-21.8, 7.24) * mm, "end": v(-21.54, 7.91) * mm});
            skLineSegment(sketch, "E1277", {"start": v(-21.54, 7.91) * mm, "end": v(-21.25, 8.57) * mm});
            skLineSegment(sketch, "E1278", {"start": v(-21.25, 8.57) * mm, "end": v(-21.02, 9.03) * mm});
            skLineSegment(sketch, "E1279", {"start": v(-21.02, 9.03) * mm, "end": v(-20.94, 9.18) * mm});
            skLineSegment(sketch, "E1280", {"start": v(-20.94, 9.18) * mm, "end": v(-20.87, 9.35) * mm});
            skLineSegment(sketch, "E1281", {"start": v(-20.87, 9.35) * mm, "end": v(-20.56, 9.84) * mm});
            skLineSegment(sketch, "E1282", {"start": v(-20.56, 9.84) * mm, "end": v(-20.09, 10.33) * mm});
            skLineSegment(sketch, "E1283", {"start": v(-20.09, 10.33) * mm, "end": v(-19.55, 10.65) * mm});
            skLineSegment(sketch, "E1284", {"start": v(-19.55, 10.65) * mm, "end": v(-18.96, 10.84) * mm});
            skLineSegment(sketch, "E1285", {"start": v(-18.96, 10.84) * mm, "end": v(-18.33, 10.9) * mm});
            skLineSegment(sketch, "E1286", {"start": v(-18.33, 10.9) * mm, "end": v(-17.68, 10.85) * mm});
            skLineSegment(sketch, "E1287", {"start": v(-17.68, 10.85) * mm, "end": v(-17, 10.72) * mm});
            skLineSegment(sketch, "E1288", {"start": v(-17, 10.72) * mm, "end": v(-16.33, 10.51) * mm});
            skLineSegment(sketch, "E1289", {"start": v(-16.33, 10.51) * mm, "end": v(-15.67, 10.26) * mm});
            skLineSegment(sketch, "E1290", {"start": v(-15.67, 10.26) * mm, "end": v(-15.04, 9.97) * mm});
            skLineSegment(sketch, "E1291", {"start": v(-15.04, 9.97) * mm, "end": v(-14.45, 9.66) * mm});
            skLineSegment(sketch, "E1292", {"start": v(-14.45, 9.66) * mm, "end": v(-13.9, 9.36) * mm});
            skLineSegment(sketch, "E1293", {"start": v(-13.9, 9.36) * mm, "end": v(-13.43, 9.07) * mm});
            skLineSegment(sketch, "E1294", {"start": v(-13.43, 9.07) * mm, "end": v(-13.03, 8.82) * mm});
            skLineSegment(sketch, "E1295", {"start": v(-13.03, 8.82) * mm, "end": v(-12.72, 8.63) * mm});
            skLineSegment(sketch, "E1296", {"start": v(-12.72, 8.63) * mm, "end": v(-12.57, 8.54) * mm});
            skLineSegment(sketch, "E1297", {"start": v(-12.57, 8.54) * mm, "end": v(-12.52, 8.51) * mm});
            skLineSegment(sketch, "E1298", {"start": v(-12.52, 8.51) * mm, "end": v(-12.43, 8.46) * mm});
            skLineSegment(sketch, "E1299", {"start": v(-12.43, 8.46) * mm, "end": v(-12.15, 8.3) * mm});
            skLineSegment(sketch, "E1300", {"start": v(-12.15, 8.3) * mm, "end": v(-11.78, 8.07) * mm});
            skLineSegment(sketch, "E1301", {"start": v(-11.78, 8.07) * mm, "end": v(-11.43, 7.85) * mm});
            skLineSegment(sketch, "E1302", {"start": v(-11.43, 7.85) * mm, "end": v(-11.1, 7.7) * mm});
            skLineSegment(sketch, "E1303", {"start": v(-11.1, 7.7) * mm, "end": v(-10.8, 7.62) * mm});
            skLineSegment(sketch, "E1304", {"start": v(-10.8, 7.62) * mm, "end": v(-10.55, 7.68) * mm});
            skLineSegment(sketch, "E1305", {"start": v(-10.55, 7.68) * mm, "end": v(-10.35, 7.9) * mm});
            skLineSegment(sketch, "E1306", {"start": v(-10.35, 7.9) * mm, "end": v(-10.23, 8.22) * mm});
            skLineSegment(sketch, "E1307", {"start": v(-10.23, 8.22) * mm, "end": v(-10.2, 8.33) * mm});
            skLineSegment(sketch, "E1308", {"start": v(-10.2, 8.33) * mm, "end": v(-10.21, 8.42) * mm});
            skLineSegment(sketch, "E1309", {"start": v(-10.21, 8.42) * mm, "end": v(-10.3, 8.67) * mm});
            skLineSegment(sketch, "E1310", {"start": v(-10.3, 8.67) * mm, "end": v(-10.55, 9) * mm});
            skLineSegment(sketch, "E1311", {"start": v(-10.55, 9) * mm, "end": v(-10.9, 9.34) * mm});
            skLineSegment(sketch, "E1312", {"start": v(-10.9, 9.34) * mm, "end": v(-11.32, 9.65) * mm});
            skLineSegment(sketch, "E1313", {"start": v(-11.32, 9.65) * mm, "end": v(-11.8, 9.96) * mm});
            skLineSegment(sketch, "E1314", {"start": v(-11.8, 9.96) * mm, "end": v(-12.3, 10.24) * mm});
            skLineSegment(sketch, "E1315", {"start": v(-12.3, 10.24) * mm, "end": v(-12.8, 10.51) * mm});
            skLineSegment(sketch, "E1316", {"start": v(-12.8, 10.51) * mm, "end": v(-13.14, 10.7) * mm});
            skLineSegment(sketch, "E1317", {"start": v(-13.14, 10.7) * mm, "end": v(-13.26, 10.76) * mm});
            skLineSegment(sketch, "E1318", {"start": v(-13.26, 10.76) * mm, "end": v(-13.41, 10.84) * mm});
            skLineSegment(sketch, "E1319", {"start": v(-13.41, 10.84) * mm, "end": v(-13.9, 11.08) * mm});
            skLineSegment(sketch, "E1320", {"start": v(-13.9, 11.08) * mm, "end": v(-14.5, 11.35) * mm});
            skLineSegment(sketch, "E1321", {"start": v(-14.5, 11.35) * mm, "end": v(-15.06, 11.58) * mm});
            skLineSegment(sketch, "E1322", {"start": v(-15.06, 11.58) * mm, "end": v(-15.58, 11.78) * mm});
            skLineSegment(sketch, "E1323", {"start": v(-15.58, 11.78) * mm, "end": v(-16.07, 11.96) * mm});
            skLineSegment(sketch, "E1324", {"start": v(-16.07, 11.96) * mm, "end": v(-16.51, 12.12) * mm});
            skLineSegment(sketch, "E1325", {"start": v(-16.51, 12.12) * mm, "end": v(-16.9, 12.26) * mm});
            skLineSegment(sketch, "E1326", {"start": v(-16.9, 12.26) * mm, "end": v(-17.25, 12.4) * mm});
            skLineSegment(sketch, "E1327", {"start": v(-17.25, 12.4) * mm, "end": v(-17.54, 12.55) * mm});
            skLineSegment(sketch, "E1328", {"start": v(-17.54, 12.55) * mm, "end": v(-17.77, 12.7) * mm});
            skLineSegment(sketch, "E1329", {"start": v(-17.77, 12.7) * mm, "end": v(-17.95, 12.88) * mm});
            skLineSegment(sketch, "E1330", {"start": v(-17.95, 12.88) * mm, "end": v(-18.06, 13.08) * mm});
            skLineSegment(sketch, "E1331", {"start": v(-18.06, 13.08) * mm, "end": v(-18.1, 13.3) * mm});
            skLineSegment(sketch, "E1332", {"start": v(-18.1, 13.3) * mm, "end": v(-18.08, 13.57) * mm});
            skLineSegment(sketch, "E1333", {"start": v(-18.08, 13.57) * mm, "end": v(-17.99, 13.89) * mm});
            skLineSegment(sketch, "E1334", {"start": v(-17.99, 13.89) * mm, "end": v(-17.87, 14.16) * mm});
            skLineSegment(sketch, "E1335", {"start": v(-17.87, 14.16) * mm, "end": v(-17.82, 14.25) * mm});
            skLineSegment(sketch, "E1336", {"start": v(-17.82, 14.25) * mm, "end": v(-17.78, 14.32) * mm});
            skLineSegment(sketch, "E1337", {"start": v(-17.78, 14.32) * mm, "end": v(-17.66, 14.52) * mm});
            skLineSegment(sketch, "E1338", {"start": v(-17.66, 14.52) * mm, "end": v(-17.43, 14.86) * mm});
            skLineSegment(sketch, "E1339", {"start": v(-17.43, 14.86) * mm, "end": v(-17.14, 15.25) * mm});
            skLineSegment(sketch, "E1340", {"start": v(-17.14, 15.25) * mm, "end": v(-16.79, 15.68) * mm});
            skLineSegment(sketch, "E1341", {"start": v(-16.79, 15.68) * mm, "end": v(-16.38, 16.14) * mm});
            skLineSegment(sketch, "E1342", {"start": v(-16.38, 16.14) * mm, "end": v(-15.93, 16.62) * mm});
            skLineSegment(sketch, "E1343", {"start": v(-15.93, 16.62) * mm, "end": v(-15.42, 17.11) * mm});
            skLineSegment(sketch, "E1344", {"start": v(-15.42, 17.11) * mm, "end": v(-15.02, 17.48) * mm});
            skLineSegment(sketch, "E1345", {"start": v(-15.02, 17.48) * mm, "end": v(-14.88, 17.6) * mm});
            skLineSegment(sketch, "E1346", {"start": v(-14.88, 17.6) * mm, "end": v(-14.73, 17.73) * mm});
            skLineSegment(sketch, "E1347", {"start": v(-14.73, 17.73) * mm, "end": v(-14.28, 18.1) * mm});
            skLineSegment(sketch, "E1348", {"start": v(-14.28, 18.1) * mm, "end": v(-13.66, 18.59) * mm});
            skLineSegment(sketch, "E1349", {"start": v(-13.66, 18.59) * mm, "end": v(-13.02, 19.04) * mm});
            skLineSegment(sketch, "E1350", {"start": v(-13.02, 19.04) * mm, "end": v(-12.37, 19.46) * mm});
            skLineSegment(sketch, "E1351", {"start": v(-12.37, 19.46) * mm, "end": v(-11.73, 19.81) * mm});
            skLineSegment(sketch, "E1352", {"start": v(-11.73, 19.81) * mm, "end": v(-11.1, 20.1) * mm});
            skLineSegment(sketch, "E1353", {"start": v(-11.1, 20.1) * mm, "end": v(-10.5, 20.31) * mm});
            skLineSegment(sketch, "E1354", {"start": v(-10.5, 20.31) * mm, "end": v(-10.09, 20.41) * mm});
            skLineSegment(sketch, "E1355", {"start": v(-10.09, 20.41) * mm, "end": v(-9.95, 20.43) * mm});
            skLineSegment(sketch, "E1356", {"start": v(-9.95, 20.43) * mm, "end": v(-9.83, 20.44) * mm});
            skLineSegment(sketch, "E1357", {"start": v(-9.83, 20.44) * mm, "end": v(-9.46, 20.43) * mm});
            skLineSegment(sketch, "E1358", {"start": v(-9.46, 20.43) * mm, "end": v(-8.98, 20.36) * mm});
            skLineSegment(sketch, "E1359", {"start": v(-8.98, 20.36) * mm, "end": v(-8.5, 20.21) * mm});
            skLineSegment(sketch, "E1360", {"start": v(-8.5, 20.21) * mm, "end": v(-8.03, 20.01) * mm});
            skLineSegment(sketch, "E1361", {"start": v(-8.03, 20.01) * mm, "end": v(-7.57, 19.76) * mm});
            skLineSegment(sketch, "E1362", {"start": v(-7.57, 19.76) * mm, "end": v(-7.13, 19.47) * mm});
            skLineSegment(sketch, "E1363", {"start": v(-7.13, 19.47) * mm, "end": v(-6.71, 19.16) * mm});
            skLineSegment(sketch, "E1364", {"start": v(-6.71, 19.16) * mm, "end": v(-6.32, 18.83) * mm});
            skLineSegment(sketch, "E1365", {"start": v(-6.32, 18.83) * mm, "end": v(-5.95, 18.5) * mm});
            skLineSegment(sketch, "E1366", {"start": v(-5.95, 18.5) * mm, "end": v(-5.62, 18.19) * mm});
            skLineSegment(sketch, "E1367", {"start": v(-5.62, 18.19) * mm, "end": v(-5.33, 17.88) * mm});
            skLineSegment(sketch, "E1368", {"start": v(-5.33, 17.88) * mm, "end": v(-5.09, 17.61) * mm});
            skLineSegment(sketch, "E1369", {"start": v(-5.09, 17.61) * mm, "end": v(-4.89, 17.38) * mm});
            skLineSegment(sketch, "E1370", {"start": v(-4.89, 17.38) * mm, "end": v(-4.74, 17.2) * mm});
            skLineSegment(sketch, "E1371", {"start": v(-4.74, 17.2) * mm, "end": v(-4.65, 17.09) * mm});
            skLineSegment(sketch, "E1372", {"start": v(-4.65, 17.09) * mm, "end": v(-4.62, 17.05) * mm});
            skLineSegment(sketch, "E1373", {"start": v(-4.62, 17.05) * mm, "end": v(-1.34, 13.4) * mm});
            skLineSegment(sketch, "E1374", {"start": v(-1.34, 13.4) * mm, "end": v(-1.29, 13.37) * mm});
            skLineSegment(sketch, "E1375", {"start": v(-1.29, 13.37) * mm, "end": v(-1.12, 13.3) * mm});
            skLineSegment(sketch, "E1376", {"start": v(-1.12, 13.3) * mm, "end": v(-0.92, 13.26) * mm});
            skLineSegment(sketch, "E1377", {"start": v(-0.92, 13.26) * mm, "end": v(-0.75, 13.27) * mm});
            skLineSegment(sketch, "E1378", {"start": v(-0.75, 13.27) * mm, "end": v(-0.6, 13.32) * mm});
            skLineSegment(sketch, "E1379", {"start": v(-0.6, 13.32) * mm, "end": v(-0.48, 13.4) * mm});
            skLineSegment(sketch, "E1380", {"start": v(-0.48, 13.4) * mm, "end": v(-0.39, 13.5) * mm});
            skLineSegment(sketch, "E1381", {"start": v(-0.39, 13.5) * mm, "end": v(-0.32, 13.6) * mm});
            skLineSegment(sketch, "E1382", {"start": v(-0.32, 13.6) * mm, "end": v(-0.28, 13.67) * mm});
            skLineSegment(sketch, "E1383", {"start": v(-0.28, 13.67) * mm, "end": v(-0.28, 13.7) * mm});
            skLineSegment(sketch, "E1384", {"start": v(-0.28, 13.7) * mm, "end": v(-0.26, 13.75) * mm});
            skLineSegment(sketch, "E1385", {"start": v(-0.26, 13.75) * mm, "end": v(-0.24, 13.9) * mm});
            skLineSegment(sketch, "E1386", {"start": v(-0.24, 13.9) * mm, "end": v(-0.25, 14.11) * mm});
            skLineSegment(sketch, "E1387", {"start": v(-0.25, 14.11) * mm, "end": v(-0.3, 14.3) * mm});
            skLineSegment(sketch, "E1388", {"start": v(-0.3, 14.3) * mm, "end": v(-0.37, 14.48) * mm});
            skLineSegment(sketch, "E1389", {"start": v(-0.37, 14.48) * mm, "end": v(-0.45, 14.62) * mm});
            skLineSegment(sketch, "E1390", {"start": v(-0.45, 14.62) * mm, "end": v(-0.53, 14.74) * mm});
            skLineSegment(sketch, "E1391", {"start": v(-0.53, 14.74) * mm, "end": v(-0.58, 14.81) * mm});
            skLineSegment(sketch, "E1392", {"start": v(-0.58, 14.81) * mm, "end": v(-0.6, 14.84) * mm});
            skLineSegment(sketch, "E1393", {"start": v(-0.6, 14.84) * mm, "end": v(-0.67, 14.92) * mm});
            skLineSegment(sketch, "E1394", {"start": v(-0.67, 14.92) * mm, "end": v(-0.85, 15.14) * mm});
            skLineSegment(sketch, "E1395", {"start": v(-0.85, 15.14) * mm, "end": v(-1.13, 15.46) * mm});
            skLineSegment(sketch, "E1396", {"start": v(-1.13, 15.46) * mm, "end": v(-1.46, 15.86) * mm});
            skLineSegment(sketch, "E1397", {"start": v(-1.46, 15.86) * mm, "end": v(-1.83, 16.3) * mm});
            skLineSegment(sketch, "E1398", {"start": v(-1.83, 16.3) * mm, "end": v(-2.22, 16.73) * mm});
            skLineSegment(sketch, "E1399", {"start": v(-2.22, 16.73) * mm, "end": v(-2.6, 17.14) * mm});
            skLineSegment(sketch, "E1400", {"start": v(-2.6, 17.14) * mm, "end": v(-2.84, 17.4) * mm});
            skLineSegment(sketch, "E1401", {"start": v(-2.84, 17.4) * mm, "end": v(-2.92, 17.49) * mm});
            skLineSegment(sketch, "E1402", {"start": v(-2.92, 17.49) * mm, "end": v(-2.96, 17.53) * mm});
            skLineSegment(sketch, "E1403", {"start": v(-2.96, 17.53) * mm, "end": v(-3.09, 17.65) * mm});
            skLineSegment(sketch, "E1404", {"start": v(-3.09, 17.65) * mm, "end": v(-3.28, 17.85) * mm});
            skLineSegment(sketch, "E1405", {"start": v(-3.28, 17.85) * mm, "end": v(-3.5, 18.06) * mm});
            skLineSegment(sketch, "E1406", {"start": v(-3.5, 18.06) * mm, "end": v(-3.73, 18.3) * mm});
            skLineSegment(sketch, "E1407", {"start": v(-3.73, 18.3) * mm, "end": v(-3.97, 18.54) * mm});
            skLineSegment(sketch, "E1408", {"start": v(-3.97, 18.54) * mm, "end": v(-4.23, 18.79) * mm});
            skLineSegment(sketch, "E1409", {"start": v(-4.23, 18.79) * mm, "end": v(-4.49, 19.04) * mm});
            skLineSegment(sketch, "E1410", {"start": v(-4.49, 19.04) * mm, "end": v(-4.74, 19.28) * mm});
            skLineSegment(sketch, "E1411", {"start": v(-4.74, 19.28) * mm, "end": v(-4.98, 19.52) * mm});
            skLineSegment(sketch, "E1412", {"start": v(-4.98, 19.52) * mm, "end": v(-5.21, 19.74) * mm});
            skLineSegment(sketch, "E1413", {"start": v(-5.21, 19.74) * mm, "end": v(-5.42, 19.94) * mm});
            skLineSegment(sketch, "E1414", {"start": v(-5.42, 19.94) * mm, "end": v(-5.6, 20.11) * mm});
            skLineSegment(sketch, "E1415", {"start": v(-5.6, 20.11) * mm, "end": v(-5.76, 20.26) * mm});
            skLineSegment(sketch, "E1416", {"start": v(-5.76, 20.26) * mm, "end": v(-5.88, 20.37) * mm});
            skLineSegment(sketch, "E1417", {"start": v(-5.88, 20.37) * mm, "end": v(-5.95, 20.44) * mm});
            skLineSegment(sketch, "E1418", {"start": v(-5.95, 20.44) * mm, "end": v(-5.98, 20.47) * mm});
            skLineSegment(sketch, "E1419", {"start": v(-5.98, 20.47) * mm, "end": v(-6.05, 20.6) * mm});
            skLineSegment(sketch, "E1420", {"start": v(-6.05, 20.6) * mm, "end": v(-6.2, 21) * mm});
            skLineSegment(sketch, "E1421", {"start": v(-6.2, 21) * mm, "end": v(-6.21, 21.44) * mm});
            skLineSegment(sketch, "E1422", {"start": v(-6.21, 21.44) * mm, "end": v(-6.07, 21.8) * mm});
            skLineSegment(sketch, "E1423", {"start": v(-6.07, 21.8) * mm, "end": v(-5.8, 22.08) * mm});
            skLineSegment(sketch, "E1424", {"start": v(-5.8, 22.08) * mm, "end": v(-5.46, 22.3) * mm});
            skLineSegment(sketch, "E1425", {"start": v(-5.46, 22.3) * mm, "end": v(-5.06, 22.45) * mm});
            skLineSegment(sketch, "E1426", {"start": v(-5.06, 22.45) * mm, "end": v(-4.66, 22.56) * mm});
            skLineSegment(sketch, "E1427", {"start": v(-4.66, 22.56) * mm, "end": v(-4.38, 22.62) * mm});
            skLineSegment(sketch, "E1428", {"start": v(-4.38, 22.62) * mm, "end": v(-4.28, 22.64) * mm});
            skLineSegment(sketch, "E1429", {"start": v(-4.28, 22.64) * mm, "end": v(-4.14, 22.65) * mm});
            skLineSegment(sketch, "E1430", {"start": v(-4.14, 22.65) * mm, "end": v(-3.72, 22.7) * mm});
            skLineSegment(sketch, "E1431", {"start": v(-3.72, 22.7) * mm, "end": v(-3.16, 22.76) * mm});
            skLineSegment(sketch, "E1432", {"start": v(-3.16, 22.76) * mm, "end": v(-2.59, 22.83) * mm});
            skLineSegment(sketch, "E1433", {"start": v(-2.59, 22.83) * mm, "end": v(-2.01, 22.9) * mm});
            skLineSegment(sketch, "E1434", {"start": v(-2.01, 22.9) * mm, "end": v(-1.44, 22.94) * mm});
            skLineSegment(sketch, "E1435", {"start": v(-1.44, 22.94) * mm, "end": v(-0.87, 22.98) * mm});
            skLineSegment(sketch, "E1436", {"start": v(-0.87, 22.98) * mm, "end": v(-0.3, 22.99) * mm});
            skLineSegment(sketch, "E1437", {"start": v(-0.3, 22.99) * mm, "end": v(0.26, 22.97) * mm});
            skLineSegment(sketch, "E1438", {"start": v(0.26, 22.97) * mm, "end": v(0.82, 22.92) * mm});
            skLineSegment(sketch, "E1439", {"start": v(0.82, 22.92) * mm, "end": v(1.37, 22.82) * mm});
            skLineSegment(sketch, "E1440", {"start": v(1.37, 22.82) * mm, "end": v(1.9, 22.68) * mm});
            skLineSegment(sketch, "E1441", {"start": v(1.9, 22.68) * mm, "end": v(2.43, 22.5) * mm});
            skLineSegment(sketch, "E1442", {"start": v(2.43, 22.5) * mm, "end": v(2.95, 22.24) * mm});
            skLineSegment(sketch, "E1443", {"start": v(2.95, 22.24) * mm, "end": v(3.45, 21.93) * mm});
            skLineSegment(sketch, "E1444", {"start": v(3.45, 21.93) * mm, "end": v(3.93, 21.55) * mm});
            skLineSegment(sketch, "E1445", {"start": v(3.93, 21.55) * mm, "end": v(4.29, 21.21) * mm});
            skLineSegment(sketch, "E1446", {"start": v(4.29, 21.21) * mm, "end": v(4.4, 21.1) * mm});
            skLineSegment(sketch, "E1447", {"start": v(4.47, -8.73) * mm, "end": v(4.64, -8.73) * mm});
            skLineSegment(sketch, "E1448", {"start": v(4.64, -8.73) * mm, "end": v(5.17, -8.66) * mm});
            skLineSegment(sketch, "E1449", {"start": v(5.17, -8.66) * mm, "end": v(5.82, -8.46) * mm});
            skLineSegment(sketch, "E1450", {"start": v(5.82, -8.46) * mm, "end": v(6.4, -8.14) * mm});
            skLineSegment(sketch, "E1451", {"start": v(6.4, -8.14) * mm, "end": v(6.91, -7.72) * mm});
            skLineSegment(sketch, "E1452", {"start": v(6.91, -7.72) * mm, "end": v(7.34, -7.21) * mm});
            skLineSegment(sketch, "E1453", {"start": v(7.34, -7.21) * mm, "end": v(7.65, -6.62) * mm});
            skLineSegment(sketch, "E1454", {"start": v(7.65, -6.62) * mm, "end": v(7.86, -5.97) * mm});
            skLineSegment(sketch, "E1455", {"start": v(7.86, -5.97) * mm, "end": v(7.93, -5.45) * mm});
            skLineSegment(sketch, "E1456", {"start": v(7.93, -5.45) * mm, "end": v(7.93, -5.28) * mm});
            skLineSegment(sketch, "E1457", {"start": v(7.93, -5.28) * mm, "end": v(7.93, -5.1) * mm});
            skLineSegment(sketch, "E1458", {"start": v(7.93, -5.1) * mm, "end": v(7.86, -4.58) * mm});
            skLineSegment(sketch, "E1459", {"start": v(7.86, -4.58) * mm, "end": v(7.65, -3.92) * mm});
            skLineSegment(sketch, "E1460", {"start": v(7.65, -3.92) * mm, "end": v(7.34, -3.33) * mm});
            skLineSegment(sketch, "E1461", {"start": v(7.34, -3.33) * mm, "end": v(6.91, -2.81) * mm});
            skLineSegment(sketch, "E1462", {"start": v(6.91, -2.81) * mm, "end": v(6.4, -2.38) * mm});
            skLineSegment(sketch, "E1463", {"start": v(6.4, -2.38) * mm, "end": v(5.82, -2.06) * mm});
            skLineSegment(sketch, "E1464", {"start": v(5.82, -2.06) * mm, "end": v(5.17, -1.86) * mm});
            skLineSegment(sketch, "E1465", {"start": v(5.17, -1.86) * mm, "end": v(4.64, -1.78) * mm});
            skLineSegment(sketch, "E1466", {"start": v(4.64, -1.78) * mm, "end": v(4.47, -1.78) * mm});
            skLineSegment(sketch, "E1467", {"start": v(4.47, -1.78) * mm, "end": v(4.3, -1.78) * mm});
            skLineSegment(sketch, "E1468", {"start": v(4.3, -1.78) * mm, "end": v(3.77, -1.86) * mm});
            skLineSegment(sketch, "E1469", {"start": v(3.77, -1.86) * mm, "end": v(3.12, -2.06) * mm});
            skLineSegment(sketch, "E1470", {"start": v(3.12, -2.06) * mm, "end": v(2.53, -2.38) * mm});
            skLineSegment(sketch, "E1471", {"start": v(2.53, -2.38) * mm, "end": v(2.02, -2.81) * mm});
            skLineSegment(sketch, "E1472", {"start": v(2.02, -2.81) * mm, "end": v(1.6, -3.33) * mm});
            skLineSegment(sketch, "E1473", {"start": v(1.6, -3.33) * mm, "end": v(1.28, -3.92) * mm});
            skLineSegment(sketch, "E1474", {"start": v(1.28, -3.92) * mm, "end": v(1.08, -4.58) * mm});
            skLineSegment(sketch, "E1475", {"start": v(1.08, -4.58) * mm, "end": v(1.01, -5.1) * mm});
            skLineSegment(sketch, "E1476", {"start": v(1.01, -5.1) * mm, "end": v(1.01, -5.28) * mm});
            skLineSegment(sketch, "E1477", {"start": v(1.01, -5.28) * mm, "end": v(1.01, -5.45) * mm});
            skLineSegment(sketch, "E1478", {"start": v(1.01, -5.45) * mm, "end": v(1.08, -5.97) * mm});
            skLineSegment(sketch, "E1479", {"start": v(1.08, -5.97) * mm, "end": v(1.28, -6.62) * mm});
            skLineSegment(sketch, "E1480", {"start": v(1.28, -6.62) * mm, "end": v(1.6, -7.21) * mm});
            skLineSegment(sketch, "E1481", {"start": v(1.6, -7.21) * mm, "end": v(2.02, -7.72) * mm});
            skLineSegment(sketch, "E1482", {"start": v(2.02, -7.72) * mm, "end": v(2.53, -8.14) * mm});
            skLineSegment(sketch, "E1483", {"start": v(2.53, -8.14) * mm, "end": v(3.12, -8.46) * mm});
            skLineSegment(sketch, "E1484", {"start": v(3.12, -8.46) * mm, "end": v(3.77, -8.66) * mm});
            skLineSegment(sketch, "E1485", {"start": v(3.77, -8.66) * mm, "end": v(4.3, -8.73) * mm});
            skLineSegment(sketch, "E1486", {"start": v(4.3, -8.73) * mm, "end": v(4.47, -8.73) * mm});
            skLineSegment(sketch, "E1487", {"start": v(-15.35, 29.04) * mm, "end": v(-15.02, 28.83) * mm});
            skLineSegment(sketch, "E1488", {"start": v(-15.02, 28.83) * mm, "end": v(-13.96, 28.26) * mm});
            skLineSegment(sketch, "E1489", {"start": v(-13.96, 28.26) * mm, "end": v(-12.49, 27.55) * mm});
            skLineSegment(sketch, "E1490", {"start": v(-12.49, 27.55) * mm, "end": v(-11.01, 26.8) * mm});
            skLineSegment(sketch, "E1491", {"start": v(-11.01, 26.8) * mm, "end": v(-9.95, 26.18) * mm});
            skLineSegment(sketch, "E1492", {"start": v(-9.95, 26.18) * mm, "end": v(-9.62, 25.95) * mm});
            skLineSegment(sketch, "E1493", {"start": v(-9.62, 25.95) * mm, "end": v(-12.63, 24.51) * mm});
            skLineSegment(sketch, "E1494", {"start": v(-12.63, 24.51) * mm, "end": v(-17.93, 27.27) * mm});
            skLineSegment(sketch, "E1495", {"start": v(-17.93, 27.27) * mm, "end": v(-17.86, 32.9) * mm});
            skLineSegment(sketch, "E1496", {"start": v(-17.86, 32.9) * mm, "end": v(-15.13, 34.33) * mm});
            skLineSegment(sketch, "E1497", {"start": v(-15.13, 34.33) * mm, "end": v(-15.1, 34.19) * mm});
            skLineSegment(sketch, "E1498", {"start": v(-15.1, 34.19) * mm, "end": v(-15.06, 33.74) * mm});
            skLineSegment(sketch, "E1499", {"start": v(-15.06, 33.74) * mm, "end": v(-15.04, 33.1) * mm});
            skLineSegment(sketch, "E1500", {"start": v(-15.04, 33.1) * mm, "end": v(-15.06, 32.43) * mm});
            skLineSegment(sketch, "E1501", {"start": v(-15.06, 32.43) * mm, "end": v(-15.12, 31.74) * mm});
            skLineSegment(sketch, "E1502", {"start": v(-15.12, 31.74) * mm, "end": v(-15.2, 31.04) * mm});
            skLineSegment(sketch, "E1503", {"start": v(-15.2, 31.04) * mm, "end": v(-15.26, 30.35) * mm});
            skLineSegment(sketch, "E1504", {"start": v(-15.26, 30.35) * mm, "end": v(-15.32, 29.68) * mm});
            skLineSegment(sketch, "E1505", {"start": v(-15.32, 29.68) * mm, "end": v(-15.35, 29.2) * mm});
            skLineSegment(sketch, "E1506", {"start": v(-15.35, 29.2) * mm, "end": v(-15.35, 29.04) * mm});
            skLineSegment(sketch, "E1507", {"start": v(-17.49, 21.31) * mm, "end": v(-22.97, 29.51) * mm});
            skLineSegment(sketch, "E1508", {"start": v(-22.97, 29.51) * mm, "end": v(-20.69, 31.13) * mm});
            skLineSegment(sketch, "E1509", {"start": v(-20.69, 31.13) * mm, "end": v(-15.17, 23.04) * mm});
            skLineSegment(sketch, "E1510", {"start": v(-15.17, 23.04) * mm, "end": v(-17.49, 21.31) * mm});
            skSolve(sketch);
        }
        {
            var Q0;
            Q0=makeQuery(id+"F0.imprint","IMPRINT",FACE,{"disambiguationData":[TD([[makeQuery(id+"F0.imprint","IMPRINT",EDGE,{"derivedFrom":sQuery(id+"F0.wireOp",EDGE,"E0")}),1.0]])]});
            var Q1;
            Q1=makeQuery(id+"F0.imprint","IMPRINT",FACE,{"disambiguationData":[TD([[makeQuery(id+"F0.imprint","IMPRINT",EDGE,{"derivedFrom":sQuery(id+"F0.wireOp",EDGE,"E136")}),1.0]])]});
            var Q2;
            Q2=makeQuery(id+"F0.imprint","IMPRINT",FACE,{"disambiguationData":[TD([[makeQuery(id+"F0.imprint","IMPRINT",EDGE,{"derivedFrom":sQuery(id+"F0.wireOp",EDGE,"E733")}),-1.0]])]});
            var Q3;
            Q3=makeQuery(id+"F0.imprint","IMPRINT",FACE,{"disambiguationData":[TD([[makeQuery(id+"F0.imprint","IMPRINT",EDGE,{"derivedFrom":sQuery(id+"F0.wireOp",EDGE,"E844")}),-1.0]])]});
            var Q4;
            Q4=makeQuery(id+"F0.imprint","IMPRINT",FACE,{"disambiguationData":[TD([[makeQuery(id+"F0.imprint","IMPRINT",EDGE,{"derivedFrom":sQuery(id+"F0.wireOp",EDGE,"E1507")}),-1.0]])]});
            var Q5;
            Q5=makeQuery(id+"F0.imprint","IMPRINT",FACE,{"disambiguationData":[TD([[makeQuery(id+"F0.imprint","IMPRINT",EDGE,{"derivedFrom":sQuery(id+"F0.wireOp",EDGE,"E1487")}),-1.0]])]});
            var Q6;
            Q6=makeQuery(id+"F0.imprint","IMPRINT",FACE,{"disambiguationData":[TD([[makeQuery(id+"F0.imprint","IMPRINT",EDGE,{"derivedFrom":sQuery(id+"F0.wireOp",EDGE,"E544")}),-1.0]])]});
            var Q7;
            Q7=makeQuery(id+"F0.imprint","IMPRINT",FACE,{"disambiguationData":[TD([[makeQuery(id+"F0.imprint","IMPRINT",EDGE,{"derivedFrom":sQuery(id+"F0.wireOp",EDGE,"E654")}),-1.0]])]});
            var Q8;
            Q8=makeQuery(id+"F0.imprint","IMPRINT",FACE,{"disambiguationData":[TD([[makeQuery(id+"F0.imprint","IMPRINT",EDGE,{"derivedFrom":sQuery(id+"F0.wireOp",EDGE,"E867")}),-1.0]])]});
            var Q9;
            Q9=makeQuery(id+"F0.imprint","IMPRINT",FACE,{"disambiguationData":[TD([[makeQuery(id+"F0.imprint","IMPRINT",EDGE,{"derivedFrom":sQuery(id+"F0.wireOp",EDGE,"E408")}),1.0]])]});
            var Q10;
            Q10=makeQuery(id+"F0.imprint","IMPRINT",FACE,{"disambiguationData":[TD([[makeQuery(id+"F0.imprint","IMPRINT",EDGE,{"derivedFrom":sQuery(id+"F0.wireOp",EDGE,"E1447")}),1.0]])]});
            var Q11;
            Q11=makeQuery(id+"F0.imprint","IMPRINT",FACE,{"disambiguationData":[TD([[makeQuery(id+"F0.imprint","IMPRINT",EDGE,{"derivedFrom":sQuery(id+"F0.wireOp",EDGE,"E888")}),-1.0]])]});
            var Q12;
            Q12=makeQuery(id+"F0.imprint","IMPRINT",FACE,{"disambiguationData":[TD([[makeQuery(id+"F0.imprint","IMPRINT",EDGE,{"derivedFrom":sQuery(id+"F0.wireOp",EDGE,"E1057")}),-1.0]])]});
            var Q13;
            Q13=makeQuery(id+"F0.imprint","IMPRINT",FACE,{"disambiguationData":[TD([[makeQuery(id+"F0.imprint","IMPRINT",EDGE,{"derivedFrom":sQuery(id+"F0.wireOp",EDGE,"E991")}),-1.0]])]});
            var Q14;
            Q14=makeQuery(id+"F0.imprint","IMPRINT",FACE,{"disambiguationData":[TD([[makeQuery(id+"F0.imprint","IMPRINT",EDGE,{"derivedFrom":sQuery(id+"F0.wireOp",EDGE,"E878")}),-1.0]])]});
            extrude(context, id + "F1", {"entities" : qUnion([Q0, Q1, Q2, Q3, Q4, Q5, Q6, Q7, Q8, Q9, Q10, Q11, Q12, Q13, Q14]), "depth" : 4 * mm});
        }
        {
            var Q0;
            Q0=makeQuery(id+"F0.imprint","IMPRINT",FACE,{"disambiguationData":[TD([[makeQuery(id+"F0.imprint","IMPRINT",EDGE,{"derivedFrom":sQuery(id+"F0.wireOp",EDGE,"E272")}),1.0]])]});
            var Q1;
            Q1=makeQuery(id+"F0.imprint","IMPRINT",FACE,{"disambiguationData":[TD([[makeQuery(id+"F0.imprint","IMPRINT",EDGE,{"derivedFrom":sQuery(id+"F0.wireOp",EDGE,"E1065")}),-1.0]])]});
            var Q2;
            Q2=makeQuery(id+"F0.imprint","IMPRINT",FACE,{"disambiguationData":[TD([[makeQuery(id+"F0.imprint","IMPRINT",EDGE,{"derivedFrom":sQuery(id+"F0.wireOp",EDGE,"E948")}),-1.0]])]});
            var Q3;
            Q3=makeQuery(id+"F0.imprint","IMPRINT",FACE,{"disambiguationData":[TD([[makeQuery(id+"F0.imprint","IMPRINT",EDGE,{"derivedFrom":sQuery(id+"F0.wireOp",EDGE,"E951")}),-1.0]])]});
            var Q4;
            Q4=makeQuery(id+"F0.imprint","IMPRINT",FACE,{"disambiguationData":[TD([[makeQuery(id+"F0.imprint","IMPRINT",EDGE,{"derivedFrom":sQuery(id+"F0.wireOp",EDGE,"E875")}),-1.0]])]});
            var Q5;
            Q5=makeQuery(id+"F0.imprint","IMPRINT",FACE,{"disambiguationData":[TD([[makeQuery(id+"F0.imprint","IMPRINT",EDGE,{"derivedFrom":sQuery(id+"F0.wireOp",EDGE,"E695")}),-1.0]])]});
            var Q6;
            Q6=makeQuery(id+"F0.imprint","IMPRINT",FACE,{"disambiguationData":[TD([[makeQuery(id+"F0.imprint","IMPRINT",EDGE,{"derivedFrom":sQuery(id+"F0.wireOp",EDGE,"E604")}),-1.0]])]});
            extrude(context, id + "F2", {"entities" : qUnion([Q0, Q1, Q2, Q3, Q4, Q5, Q6]), "operationType" : NewBodyOperationType.ADD, "depth" : 2 * mm});
        }
    });
